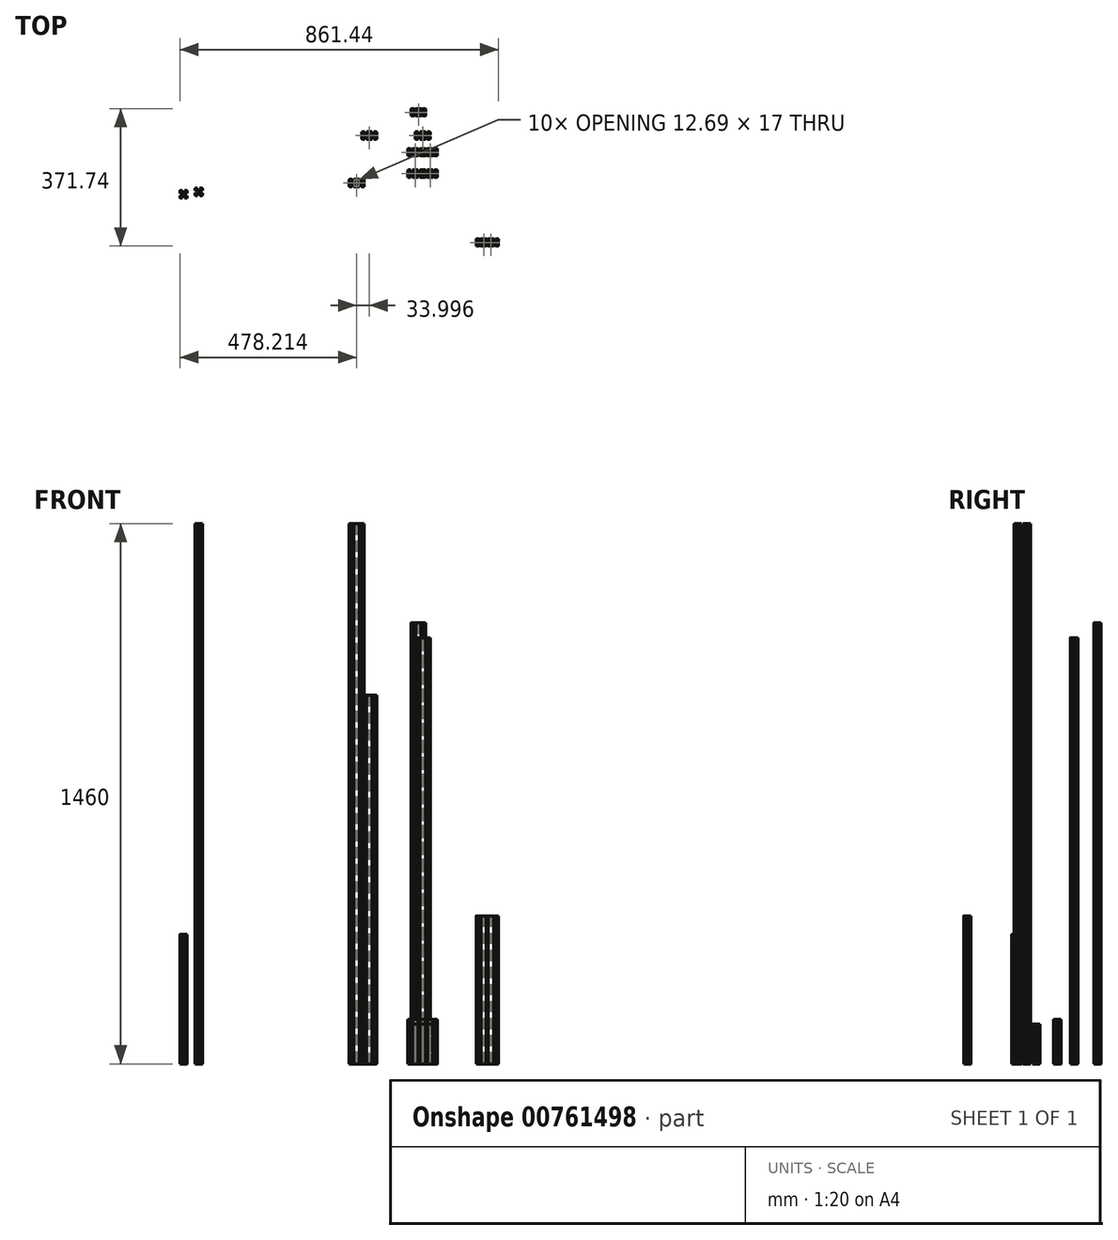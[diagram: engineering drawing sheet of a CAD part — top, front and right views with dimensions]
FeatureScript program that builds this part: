
annotation { "Feature Type Name" : "Feature", "Feature Type Description" : "" }
export const myFeature = defineFeature(function(context is Context, id is Id, definition is map)
    precondition{}
    {
        {
            var Q0;
            Q0=qCreatedBy(makeId("Top.planeOp"),FACE);
            var sketch = newSketch(context, id + "F0", { "sketchPlane" : qUnion([Q0])});
            skLineSegment(sketch, "E0", {"start": v(-5.25, 65.2) * mm, "end": v(-5.25, 60.44) * mm});
            skArc(sketch, "E1", {"start": v(-0.8, 64.75) * mm, "mid": v(-0.24, 65.32) * mm, "end": v(0.52, 65.12) * mm});
            skLineSegment(sketch, "E2", {"start": v(-19.48, 65.12) * mm, "end": v(-19.3, 64.94) * mm});
            skLineSegment(sketch, "E3", {"start": v(1.03, 53.81) * mm, "end": v(1.03, 53.33) * mm});
            skArc(sketch, "E4", {"start": v(-2.4, 64.75) * mm, "mid": v(-1.6, 64.91) * mm, "end": v(-0.8, 64.75) * mm});
            skArc(sketch, "E5", {"start": v(-3.72, 65.12) * mm, "mid": v(-2.96, 65.32) * mm, "end": v(-2.4, 64.75) * mm});
            skLineSegment(sketch, "E6", {"start": v(-3.72, 65.12) * mm, "end": v(-3.9, 64.94) * mm});
            skArc(sketch, "E7", {"start": v(-3.54, 63.62) * mm, "mid": v(-4.1, 64.18) * mm, "end": v(-3.9, 64.94) * mm});
            skArc(sketch, "E8", {"start": v(-3.54, 62.02) * mm, "mid": v(-3.7, 62.82) * mm, "end": v(-3.54, 63.62) * mm});
            skArc(sketch, "E9", {"start": v(-3.9, 60.7) * mm, "mid": v(-4.1, 61.46) * mm, "end": v(-3.54, 62.02) * mm});
            skLineSegment(sketch, "E10", {"start": v(-3.9, 60.7) * mm, "end": v(-3.72, 60.51) * mm});
            skArc(sketch, "E11", {"start": v(-2.4, 60.88) * mm, "mid": v(-2.96, 60.31) * mm, "end": v(-3.72, 60.51) * mm});
            skArc(sketch, "E12", {"start": v(-0.8, 60.88) * mm, "mid": v(-1.6, 60.72) * mm, "end": v(-2.4, 60.88) * mm});
            skArc(sketch, "E13", {"start": v(0.52, 60.51) * mm, "mid": v(-0.24, 60.31) * mm, "end": v(-0.8, 60.88) * mm});
            skLineSegment(sketch, "E14", {"start": v(0.52, 60.51) * mm, "end": v(0.7, 60.7) * mm});
            skArc(sketch, "E15", {"start": v(0.34, 62.02) * mm, "mid": v(0.9, 61.46) * mm, "end": v(0.7, 60.7) * mm});
            skArc(sketch, "E16", {"start": v(0.34, 63.62) * mm, "mid": v(0.5, 62.82) * mm, "end": v(0.34, 62.02) * mm});
            skArc(sketch, "E17", {"start": v(0.7, 64.94) * mm, "mid": v(0.9, 64.18) * mm, "end": v(0.34, 63.62) * mm});
            skLineSegment(sketch, "E18", {"start": v(0.7, 64.94) * mm, "end": v(0.52, 65.12) * mm});
            skArc(sketch, "E19", {"start": v(-19.48, 65.12) * mm, "mid": v(-20.24, 65.32) * mm, "end": v(-20.8, 64.75) * mm});
            skArc(sketch, "E20", {"start": v(-20.8, 64.75) * mm, "mid": v(-21.6, 64.91) * mm, "end": v(-22.4, 64.75) * mm});
            skArc(sketch, "E21", {"start": v(-22.4, 64.75) * mm, "mid": v(-22.96, 65.32) * mm, "end": v(-23.72, 65.12) * mm});
            skLineSegment(sketch, "E22", {"start": v(-23.9, 64.94) * mm, "end": v(-23.72, 65.12) * mm});
            skArc(sketch, "E23", {"start": v(-23.9, 64.94) * mm, "mid": v(-24.1, 64.18) * mm, "end": v(-23.54, 63.62) * mm});
            skArc(sketch, "E24", {"start": v(-23.54, 63.62) * mm, "mid": v(-23.7, 62.82) * mm, "end": v(-23.54, 62.02) * mm});
            skArc(sketch, "E25", {"start": v(-23.54, 62.02) * mm, "mid": v(-24.1, 61.46) * mm, "end": v(-23.9, 60.7) * mm});
            skLineSegment(sketch, "E26", {"start": v(-23.72, 60.51) * mm, "end": v(-23.9, 60.7) * mm});
            skArc(sketch, "E27", {"start": v(-23.72, 60.51) * mm, "mid": v(-22.96, 60.31) * mm, "end": v(-22.4, 60.88) * mm});
            skArc(sketch, "E28", {"start": v(-22.4, 60.88) * mm, "mid": v(-21.6, 60.72) * mm, "end": v(-20.8, 60.88) * mm});
            skArc(sketch, "E29", {"start": v(-20.8, 60.88) * mm, "mid": v(-20.24, 60.31) * mm, "end": v(-19.48, 60.51) * mm});
            skLineSegment(sketch, "E30", {"start": v(-19.3, 60.7) * mm, "end": v(-19.48, 60.51) * mm});
            skArc(sketch, "E31", {"start": v(-19.3, 60.7) * mm, "mid": v(-19.1, 61.46) * mm, "end": v(-19.66, 62.02) * mm});
            skArc(sketch, "E32", {"start": v(-19.66, 62.02) * mm, "mid": v(-19.5, 62.82) * mm, "end": v(-19.66, 63.62) * mm});
            skArc(sketch, "E33", {"start": v(-19.66, 63.62) * mm, "mid": v(-19.1, 64.18) * mm, "end": v(-19.3, 64.94) * mm});
            skArc(sketch, "E34", {"start": v(1.03, 53.81) * mm, "mid": v(1.18, 54.17) * mm, "end": v(1.54, 54.32) * mm});
            skLineSegment(sketch, "E35", {"start": v(1.54, 54.32) * mm, "end": v(3.89, 54.32) * mm});
            skArc(sketch, "E36", {"start": v(4.4, 54.83) * mm, "mid": v(4.25, 54.47) * mm, "end": v(3.89, 54.32) * mm});
            skLineSegment(sketch, "E37", {"start": v(4.4, 55.55) * mm, "end": v(4.4, 54.83) * mm});
            skArc(sketch, "E38", {"start": v(4.25, 55.91) * mm, "mid": v(4.36, 55.75) * mm, "end": v(4.4, 55.55) * mm});
            skLineSegment(sketch, "E39", {"start": v(4.25, 55.91) * mm, "end": v(1.14, 59.02) * mm});
            skArc(sketch, "E40", {"start": v(0.78, 59.16) * mm, "mid": v(0.98, 59.13) * mm, "end": v(1.14, 59.02) * mm});
            skLineSegment(sketch, "E41", {"start": v(0.78, 59.16) * mm, "end": v(-3.98, 59.16) * mm});
            skArc(sketch, "E42", {"start": v(-4.34, 59.02) * mm, "mid": v(-4.18, 59.13) * mm, "end": v(-3.98, 59.16) * mm});
            skLineSegment(sketch, "E43", {"start": v(-4.34, 59.02) * mm, "end": v(-7.45, 55.91) * mm});
            skArc(sketch, "E44", {"start": v(-7.6, 55.55) * mm, "mid": v(-7.56, 55.75) * mm, "end": v(-7.45, 55.91) * mm});
            skLineSegment(sketch, "E45", {"start": v(-7.6, 55.55) * mm, "end": v(-7.6, 54.83) * mm});
            skArc(sketch, "E46", {"start": v(-7.09, 54.32) * mm, "mid": v(-7.45, 54.47) * mm, "end": v(-7.6, 54.83) * mm});
            skLineSegment(sketch, "E47", {"start": v(-7.09, 54.32) * mm, "end": v(-4.74, 54.32) * mm});
            skArc(sketch, "E48", {"start": v(-4.74, 54.32) * mm, "mid": v(-4.38, 54.17) * mm, "end": v(-4.23, 53.81) * mm});
            skLineSegment(sketch, "E49", {"start": v(-4.23, 53.33) * mm, "end": v(-4.23, 53.81) * mm});
            skArc(sketch, "E50", {"start": v(-4.23, 53.33) * mm, "mid": v(-4.38, 52.97) * mm, "end": v(-4.74, 52.82) * mm});
            skLineSegment(sketch, "E51", {"start": v(-18.46, 52.82) * mm, "end": v(-4.74, 52.82) * mm});
            skArc(sketch, "E52", {"start": v(-18.97, 53.33) * mm, "mid": v(-18.82, 52.97) * mm, "end": v(-18.46, 52.82) * mm});
            skLineSegment(sketch, "E53", {"start": v(-18.97, 53.33) * mm, "end": v(-18.97, 53.81) * mm});
            skArc(sketch, "E54", {"start": v(-18.46, 54.32) * mm, "mid": v(-18.82, 54.17) * mm, "end": v(-18.97, 53.81) * mm});
            skLineSegment(sketch, "E55", {"start": v(-16.11, 54.32) * mm, "end": v(-18.46, 54.32) * mm});
            skArc(sketch, "E56", {"start": v(-16.11, 54.32) * mm, "mid": v(-15.75, 54.47) * mm, "end": v(-15.6, 54.83) * mm});
            skLineSegment(sketch, "E57", {"start": v(-15.6, 55.55) * mm, "end": v(-15.6, 54.83) * mm});
            skArc(sketch, "E58", {"start": v(-15.6, 55.55) * mm, "mid": v(-15.64, 55.75) * mm, "end": v(-15.75, 55.91) * mm});
            skLineSegment(sketch, "E59", {"start": v(-18.86, 59.02) * mm, "end": v(-15.75, 55.91) * mm});
            skArc(sketch, "E60", {"start": v(-18.86, 59.02) * mm, "mid": v(-19.02, 59.13) * mm, "end": v(-19.22, 59.16) * mm});
            skLineSegment(sketch, "E61", {"start": v(-23.98, 59.16) * mm, "end": v(-19.22, 59.16) * mm});
            skArc(sketch, "E62", {"start": v(-23.98, 59.16) * mm, "mid": v(-24.18, 59.13) * mm, "end": v(-24.34, 59.02) * mm});
            skLineSegment(sketch, "E63", {"start": v(-27.45, 55.91) * mm, "end": v(-24.34, 59.02) * mm});
            skArc(sketch, "E64", {"start": v(-27.45, 55.91) * mm, "mid": v(-27.56, 55.75) * mm, "end": v(-27.6, 55.55) * mm});
            skLineSegment(sketch, "E65", {"start": v(-27.6, 55.55) * mm, "end": v(-27.6, 54.83) * mm});
            skArc(sketch, "E66", {"start": v(-27.6, 54.83) * mm, "mid": v(-27.45, 54.47) * mm, "end": v(-27.09, 54.32) * mm});
            skLineSegment(sketch, "E67", {"start": v(-24.74, 54.32) * mm, "end": v(-27.09, 54.32) * mm});
            skArc(sketch, "E68", {"start": v(-24.23, 53.81) * mm, "mid": v(-24.38, 54.17) * mm, "end": v(-24.74, 54.32) * mm});
            skLineSegment(sketch, "E69", {"start": v(-24.23, 53.81) * mm, "end": v(-24.23, 53.33) * mm});
            skArc(sketch, "E70", {"start": v(-24.74, 52.82) * mm, "mid": v(-24.38, 52.97) * mm, "end": v(-24.23, 53.33) * mm});
            skLineSegment(sketch, "E71", {"start": v(-30.1, 52.82) * mm, "end": v(-24.74, 52.82) * mm});
            skArc(sketch, "E72", {"start": v(-31.6, 54.32) * mm, "mid": v(-31.16, 53.26) * mm, "end": v(-30.1, 52.82) * mm});
            skLineSegment(sketch, "E73", {"start": v(-31.6, 54.32) * mm, "end": v(-31.6, 59.68) * mm});
            skArc(sketch, "E74", {"start": v(-31.1, 60.19) * mm, "mid": v(-31.45, 60.04) * mm, "end": v(-31.6, 59.68) * mm});
            skLineSegment(sketch, "E75", {"start": v(-31.1, 60.19) * mm, "end": v(-30.6, 60.19) * mm});
            skArc(sketch, "E76", {"start": v(-30.1, 59.68) * mm, "mid": v(-30.25, 60.04) * mm, "end": v(-30.6, 60.19) * mm});
            skLineSegment(sketch, "E77", {"start": v(-30.1, 57.33) * mm, "end": v(-30.1, 59.68) * mm});
            skArc(sketch, "E78", {"start": v(-30.1, 57.33) * mm, "mid": v(-29.95, 56.97) * mm, "end": v(-29.6, 56.82) * mm});
            skLineSegment(sketch, "E79", {"start": v(-28.87, 56.82) * mm, "end": v(-29.6, 56.82) * mm});
            skArc(sketch, "E80", {"start": v(-28.87, 56.82) * mm, "mid": v(-28.67, 56.86) * mm, "end": v(-28.5, 56.97) * mm});
            skLineSegment(sketch, "E81", {"start": v(-25.4, 60.08) * mm, "end": v(-28.5, 56.97) * mm});
            skArc(sketch, "E82", {"start": v(-25.4, 60.08) * mm, "mid": v(-25.3, 60.24) * mm, "end": v(-25.25, 60.44) * mm});
            skLineSegment(sketch, "E83", {"start": v(-25.25, 65.2) * mm, "end": v(-25.25, 60.44) * mm});
            skArc(sketch, "E84", {"start": v(-25.25, 65.2) * mm, "mid": v(-25.3, 65.4) * mm, "end": v(-25.4, 65.56) * mm});
            skLineSegment(sketch, "E85", {"start": v(-25.4, 65.56) * mm, "end": v(-28.5, 68.67) * mm});
            skArc(sketch, "E86", {"start": v(-28.5, 68.67) * mm, "mid": v(-28.67, 68.78) * mm, "end": v(-28.87, 68.81) * mm});
            skLineSegment(sketch, "E87", {"start": v(-28.87, 68.81) * mm, "end": v(-29.6, 68.81) * mm});
            skArc(sketch, "E88", {"start": v(-29.6, 68.81) * mm, "mid": v(-29.95, 68.67) * mm, "end": v(-30.1, 68.3) * mm});
            skLineSegment(sketch, "E89", {"start": v(-30.1, 68.3) * mm, "end": v(-30.1, 65.96) * mm});
            skArc(sketch, "E90", {"start": v(-30.6, 65.45) * mm, "mid": v(-30.25, 65.6) * mm, "end": v(-30.1, 65.96) * mm});
            skLineSegment(sketch, "E91", {"start": v(-30.6, 65.45) * mm, "end": v(-31.1, 65.45) * mm});
            skArc(sketch, "E92", {"start": v(-31.6, 65.96) * mm, "mid": v(-31.45, 65.6) * mm, "end": v(-31.1, 65.45) * mm});
            skLineSegment(sketch, "E93", {"start": v(-31.6, 65.96) * mm, "end": v(-31.6, 71.32) * mm});
            skArc(sketch, "E94", {"start": v(-30.1, 72.82) * mm, "mid": v(-31.16, 72.38) * mm, "end": v(-31.6, 71.32) * mm});
            skLineSegment(sketch, "E95", {"start": v(-30.1, 72.82) * mm, "end": v(-24.74, 72.82) * mm});
            skArc(sketch, "E96", {"start": v(-24.23, 72.31) * mm, "mid": v(-24.38, 72.67) * mm, "end": v(-24.74, 72.82) * mm});
            skLineSegment(sketch, "E97", {"start": v(-24.23, 72.31) * mm, "end": v(-24.23, 71.83) * mm});
            skArc(sketch, "E98", {"start": v(-24.74, 71.32) * mm, "mid": v(-24.38, 71.47) * mm, "end": v(-24.23, 71.83) * mm});
            skLineSegment(sketch, "E99", {"start": v(-24.74, 71.32) * mm, "end": v(-27.09, 71.32) * mm});
            skArc(sketch, "E100", {"start": v(-27.09, 71.32) * mm, "mid": v(-27.45, 71.17) * mm, "end": v(-27.6, 70.81) * mm});
            skLineSegment(sketch, "E101", {"start": v(-27.6, 70.81) * mm, "end": v(-27.6, 70.09) * mm});
            skArc(sketch, "E102", {"start": v(-27.6, 70.09) * mm, "mid": v(-27.56, 69.9) * mm, "end": v(-27.45, 69.73) * mm});
            skLineSegment(sketch, "E103", {"start": v(-27.45, 69.73) * mm, "end": v(-24.34, 66.62) * mm});
            skArc(sketch, "E104", {"start": v(-24.34, 66.62) * mm, "mid": v(-24.18, 66.51) * mm, "end": v(-23.98, 66.47) * mm});
            skLineSegment(sketch, "E105", {"start": v(-23.98, 66.47) * mm, "end": v(-19.22, 66.47) * mm});
            skArc(sketch, "E106", {"start": v(-19.22, 66.47) * mm, "mid": v(-19.02, 66.51) * mm, "end": v(-18.86, 66.62) * mm});
            skLineSegment(sketch, "E107", {"start": v(-18.86, 66.62) * mm, "end": v(-15.75, 69.73) * mm});
            skArc(sketch, "E108", {"start": v(-15.75, 69.73) * mm, "mid": v(-15.64, 69.9) * mm, "end": v(-15.6, 70.09) * mm});
            skLineSegment(sketch, "E109", {"start": v(-15.6, 70.81) * mm, "end": v(-15.6, 70.09) * mm});
            skArc(sketch, "E110", {"start": v(-15.6, 70.81) * mm, "mid": v(-15.75, 71.17) * mm, "end": v(-16.11, 71.32) * mm});
            skLineSegment(sketch, "E111", {"start": v(-16.11, 71.32) * mm, "end": v(-18.46, 71.32) * mm});
            skArc(sketch, "E112", {"start": v(-18.97, 71.83) * mm, "mid": v(-18.82, 71.47) * mm, "end": v(-18.46, 71.32) * mm});
            skLineSegment(sketch, "E113", {"start": v(-18.97, 71.83) * mm, "end": v(-18.97, 72.31) * mm});
            skArc(sketch, "E114", {"start": v(-18.46, 72.82) * mm, "mid": v(-18.82, 72.67) * mm, "end": v(-18.97, 72.31) * mm});
            skLineSegment(sketch, "E115", {"start": v(-4.74, 72.82) * mm, "end": v(-18.46, 72.82) * mm});
            skArc(sketch, "E116", {"start": v(-4.74, 72.82) * mm, "mid": v(-4.38, 72.67) * mm, "end": v(-4.23, 72.31) * mm});
            skLineSegment(sketch, "E117", {"start": v(-4.23, 71.83) * mm, "end": v(-4.23, 72.31) * mm});
            skArc(sketch, "E118", {"start": v(-4.23, 71.83) * mm, "mid": v(-4.38, 71.47) * mm, "end": v(-4.74, 71.32) * mm});
            skLineSegment(sketch, "E119", {"start": v(-7.09, 71.32) * mm, "end": v(-4.74, 71.32) * mm});
            skArc(sketch, "E120", {"start": v(-7.6, 70.81) * mm, "mid": v(-7.45, 71.17) * mm, "end": v(-7.09, 71.32) * mm});
            skLineSegment(sketch, "E121", {"start": v(-7.6, 70.81) * mm, "end": v(-7.6, 70.09) * mm});
            skArc(sketch, "E122", {"start": v(-7.45, 69.73) * mm, "mid": v(-7.56, 69.9) * mm, "end": v(-7.6, 70.09) * mm});
            skLineSegment(sketch, "E123", {"start": v(-4.34, 66.62) * mm, "end": v(-7.45, 69.73) * mm});
            skArc(sketch, "E124", {"start": v(-3.98, 66.47) * mm, "mid": v(-4.18, 66.51) * mm, "end": v(-4.34, 66.62) * mm});
            skLineSegment(sketch, "E125", {"start": v(0.78, 66.47) * mm, "end": v(-3.98, 66.47) * mm});
            skArc(sketch, "E126", {"start": v(1.14, 66.62) * mm, "mid": v(0.98, 66.51) * mm, "end": v(0.78, 66.47) * mm});
            skLineSegment(sketch, "E127", {"start": v(4.25, 69.73) * mm, "end": v(1.14, 66.62) * mm});
            skArc(sketch, "E128", {"start": v(4.4, 70.09) * mm, "mid": v(4.36, 69.9) * mm, "end": v(4.25, 69.73) * mm});
            skLineSegment(sketch, "E129", {"start": v(4.4, 70.81) * mm, "end": v(4.4, 70.09) * mm});
            skArc(sketch, "E130", {"start": v(3.89, 71.32) * mm, "mid": v(4.25, 71.17) * mm, "end": v(4.4, 70.81) * mm});
            skLineSegment(sketch, "E131", {"start": v(1.54, 71.32) * mm, "end": v(3.89, 71.32) * mm});
            skArc(sketch, "E132", {"start": v(1.54, 71.32) * mm, "mid": v(1.18, 71.47) * mm, "end": v(1.03, 71.83) * mm});
            skLineSegment(sketch, "E133", {"start": v(1.03, 72.31) * mm, "end": v(1.03, 71.83) * mm});
            skArc(sketch, "E134", {"start": v(1.03, 72.31) * mm, "mid": v(1.18, 72.67) * mm, "end": v(1.54, 72.82) * mm});
            skLineSegment(sketch, "E135", {"start": v(6.9, 72.82) * mm, "end": v(1.54, 72.82) * mm});
            skArc(sketch, "E136", {"start": v(6.9, 72.82) * mm, "mid": v(7.96, 72.38) * mm, "end": v(8.4, 71.32) * mm});
            skLineSegment(sketch, "E137", {"start": v(8.4, 65.96) * mm, "end": v(8.4, 71.32) * mm});
            skArc(sketch, "E138", {"start": v(8.4, 65.96) * mm, "mid": v(8.25, 65.6) * mm, "end": v(7.9, 65.45) * mm});
            skLineSegment(sketch, "E139", {"start": v(7.4, 65.45) * mm, "end": v(7.9, 65.45) * mm});
            skArc(sketch, "E140", {"start": v(7.4, 65.45) * mm, "mid": v(7.05, 65.6) * mm, "end": v(6.9, 65.96) * mm});
            skLineSegment(sketch, "E141", {"start": v(6.9, 68.3) * mm, "end": v(6.9, 65.96) * mm});
            skArc(sketch, "E142", {"start": v(6.4, 68.81) * mm, "mid": v(6.75, 68.67) * mm, "end": v(6.9, 68.3) * mm});
            skLineSegment(sketch, "E143", {"start": v(5.67, 68.81) * mm, "end": v(6.4, 68.81) * mm});
            skArc(sketch, "E144", {"start": v(5.3, 68.67) * mm, "mid": v(5.47, 68.78) * mm, "end": v(5.67, 68.81) * mm});
            skLineSegment(sketch, "E145", {"start": v(2.2, 65.56) * mm, "end": v(5.3, 68.67) * mm});
            skArc(sketch, "E146", {"start": v(2.06, 65.2) * mm, "mid": v(2.1, 65.4) * mm, "end": v(2.2, 65.56) * mm});
            skLineSegment(sketch, "E147", {"start": v(2.06, 65.2) * mm, "end": v(2.06, 60.44) * mm});
            skArc(sketch, "E148", {"start": v(2.2, 60.08) * mm, "mid": v(2.1, 60.24) * mm, "end": v(2.06, 60.44) * mm});
            skLineSegment(sketch, "E149", {"start": v(2.2, 60.08) * mm, "end": v(5.3, 56.97) * mm});
            skArc(sketch, "E150", {"start": v(5.67, 56.82) * mm, "mid": v(5.47, 56.86) * mm, "end": v(5.3, 56.97) * mm});
            skLineSegment(sketch, "E151", {"start": v(5.67, 56.82) * mm, "end": v(6.4, 56.82) * mm});
            skArc(sketch, "E152", {"start": v(6.9, 57.33) * mm, "mid": v(6.75, 56.97) * mm, "end": v(6.4, 56.82) * mm});
            skLineSegment(sketch, "E153", {"start": v(6.9, 57.33) * mm, "end": v(6.9, 59.68) * mm});
            skArc(sketch, "E154", {"start": v(6.9, 59.68) * mm, "mid": v(7.05, 60.04) * mm, "end": v(7.4, 60.19) * mm});
            skLineSegment(sketch, "E155", {"start": v(7.9, 60.19) * mm, "end": v(7.4, 60.19) * mm});
            skArc(sketch, "E156", {"start": v(7.9, 60.19) * mm, "mid": v(8.25, 60.04) * mm, "end": v(8.4, 59.68) * mm});
            skLineSegment(sketch, "E157", {"start": v(8.4, 54.32) * mm, "end": v(8.4, 59.68) * mm});
            skArc(sketch, "E158", {"start": v(8.4, 54.32) * mm, "mid": v(7.96, 53.26) * mm, "end": v(6.9, 52.82) * mm});
            skLineSegment(sketch, "E159", {"start": v(6.9, 52.82) * mm, "end": v(1.54, 52.82) * mm});
            skArc(sketch, "E160", {"start": v(1.54, 52.82) * mm, "mid": v(1.18, 52.97) * mm, "end": v(1.03, 53.33) * mm});
            skArc(sketch, "E161", {"start": v(-5.25, 65.2) * mm, "mid": v(-5.3, 65.4) * mm, "end": v(-5.4, 65.56) * mm});
            skLineSegment(sketch, "E162", {"start": v(-5.4, 65.56) * mm, "end": v(-8.95, 69.1) * mm});
            skArc(sketch, "E163", {"start": v(-8.95, 69.1) * mm, "mid": v(-9.06, 69.27) * mm, "end": v(-9.1, 69.46) * mm});
            skLineSegment(sketch, "E164", {"start": v(-9.1, 70.81) * mm, "end": v(-9.1, 69.46) * mm});
            skArc(sketch, "E165", {"start": v(-9.6, 71.32) * mm, "mid": v(-9.24, 71.17) * mm, "end": v(-9.1, 70.81) * mm});
            skLineSegment(sketch, "E166", {"start": v(-13.6, 71.32) * mm, "end": v(-9.6, 71.32) * mm});
            skArc(sketch, "E167", {"start": v(-13.6, 71.32) * mm, "mid": v(-13.96, 71.17) * mm, "end": v(-14.1, 70.81) * mm});
            skLineSegment(sketch, "E168", {"start": v(-14.1, 70.81) * mm, "end": v(-14.1, 69.46) * mm});
            skArc(sketch, "E169", {"start": v(-14.25, 69.1) * mm, "mid": v(-14.14, 69.27) * mm, "end": v(-14.1, 69.46) * mm});
            skLineSegment(sketch, "E170", {"start": v(-17.8, 65.56) * mm, "end": v(-14.25, 69.1) * mm});
            skArc(sketch, "E171", {"start": v(-17.8, 65.56) * mm, "mid": v(-17.9, 65.4) * mm, "end": v(-17.94, 65.2) * mm});
            skLineSegment(sketch, "E172", {"start": v(-17.94, 65.2) * mm, "end": v(-17.94, 60.44) * mm});
            skArc(sketch, "E173", {"start": v(-17.94, 60.44) * mm, "mid": v(-17.9, 60.24) * mm, "end": v(-17.8, 60.08) * mm});
            skLineSegment(sketch, "E174", {"start": v(-17.8, 60.08) * mm, "end": v(-14.25, 56.53) * mm});
            skArc(sketch, "E175", {"start": v(-14.1, 56.17) * mm, "mid": v(-14.14, 56.37) * mm, "end": v(-14.25, 56.53) * mm});
            skLineSegment(sketch, "E176", {"start": v(-14.1, 56.17) * mm, "end": v(-14.1, 54.83) * mm});
            skArc(sketch, "E177", {"start": v(-14.1, 54.83) * mm, "mid": v(-13.96, 54.47) * mm, "end": v(-13.6, 54.32) * mm});
            skLineSegment(sketch, "E178", {"start": v(-13.6, 54.32) * mm, "end": v(-9.6, 54.32) * mm});
            skArc(sketch, "E179", {"start": v(-9.1, 54.83) * mm, "mid": v(-9.24, 54.47) * mm, "end": v(-9.6, 54.32) * mm});
            skLineSegment(sketch, "E180", {"start": v(-9.1, 56.17) * mm, "end": v(-9.1, 54.83) * mm});
            skArc(sketch, "E181", {"start": v(-9.1, 56.17) * mm, "mid": v(-9.06, 56.37) * mm, "end": v(-8.95, 56.53) * mm});
            skLineSegment(sketch, "E182", {"start": v(-5.4, 60.08) * mm, "end": v(-8.95, 56.53) * mm});
            skArc(sketch, "E183", {"start": v(-5.25, 60.44) * mm, "mid": v(-5.3, 60.24) * mm, "end": v(-5.4, 60.08) * mm});
            skSolve(sketch);
        }
        {
            var Q0;
            Q0 = qSketchRegion(id + "F0", true);
            extrude(context, id + "F1", {"entities" : qUnion([Q0]), "depth" : 1192 * mm, "offsetDistance" : 25 * mm});
        }
        {
            var Q0;
            Q0=qCreatedBy(makeId("Top.planeOp"),FACE);
            var sketch = newSketch(context, id + "F2", { "sketchPlane" : qUnion([Q0])});
            skLineSegment(sketch, "E184", {"start": v(6.35, 2.38) * mm, "end": v(6.35, -2.38) * mm});
            skArc(sketch, "E185", {"start": v(10.8, 1.94) * mm, "mid": v(11.36, 2.5) * mm, "end": v(12.12, 2.3) * mm});
            skLineSegment(sketch, "E186", {"start": v(-7.88, 2.3) * mm, "end": v(-7.7, 2.12) * mm});
            skLineSegment(sketch, "E187", {"start": v(12.63, -9) * mm, "end": v(12.63, -9.5) * mm});
            skArc(sketch, "E188", {"start": v(9.2, 1.94) * mm, "mid": v(10, 2.1) * mm, "end": v(10.8, 1.94) * mm});
            skArc(sketch, "E189", {"start": v(7.88, 2.3) * mm, "mid": v(8.64, 2.5) * mm, "end": v(9.2, 1.94) * mm});
            skLineSegment(sketch, "E190", {"start": v(7.88, 2.3) * mm, "end": v(7.7, 2.12) * mm});
            skArc(sketch, "E191", {"start": v(8.06, 0.8) * mm, "mid": v(7.5, 1.36) * mm, "end": v(7.7, 2.12) * mm});
            skArc(sketch, "E192", {"start": v(8.06, -0.8) * mm, "mid": v(7.9, 0) * mm, "end": v(8.06, 0.8) * mm});
            skArc(sketch, "E193", {"start": v(7.7, -2.12) * mm, "mid": v(7.5, -1.36) * mm, "end": v(8.06, -0.8) * mm});
            skLineSegment(sketch, "E194", {"start": v(7.7, -2.12) * mm, "end": v(7.88, -2.3) * mm});
            skArc(sketch, "E195", {"start": v(9.2, -1.94) * mm, "mid": v(8.64, -2.5) * mm, "end": v(7.88, -2.3) * mm});
            skArc(sketch, "E196", {"start": v(10.8, -1.94) * mm, "mid": v(10, -2.1) * mm, "end": v(9.2, -1.94) * mm});
            skArc(sketch, "E197", {"start": v(12.12, -2.3) * mm, "mid": v(11.36, -2.5) * mm, "end": v(10.8, -1.94) * mm});
            skLineSegment(sketch, "E198", {"start": v(12.12, -2.3) * mm, "end": v(12.3, -2.12) * mm});
            skArc(sketch, "E199", {"start": v(11.94, -0.8) * mm, "mid": v(12.5, -1.36) * mm, "end": v(12.3, -2.12) * mm});
            skArc(sketch, "E200", {"start": v(11.94, 0.8) * mm, "mid": v(12.1, 0) * mm, "end": v(11.94, -0.8) * mm});
            skArc(sketch, "E201", {"start": v(12.3, 2.12) * mm, "mid": v(12.5, 1.36) * mm, "end": v(11.94, 0.8) * mm});
            skLineSegment(sketch, "E202", {"start": v(12.3, 2.12) * mm, "end": v(12.12, 2.3) * mm});
            skArc(sketch, "E203", {"start": v(-7.88, 2.3) * mm, "mid": v(-8.64, 2.5) * mm, "end": v(-9.2, 1.94) * mm});
            skArc(sketch, "E204", {"start": v(-9.2, 1.94) * mm, "mid": v(-10, 2.1) * mm, "end": v(-10.8, 1.94) * mm});
            skArc(sketch, "E205", {"start": v(-10.8, 1.94) * mm, "mid": v(-11.36, 2.5) * mm, "end": v(-12.12, 2.3) * mm});
            skLineSegment(sketch, "E206", {"start": v(-12.3, 2.12) * mm, "end": v(-12.12, 2.3) * mm});
            skArc(sketch, "E207", {"start": v(-12.3, 2.12) * mm, "mid": v(-12.5, 1.36) * mm, "end": v(-11.94, 0.8) * mm});
            skArc(sketch, "E208", {"start": v(-11.94, 0.8) * mm, "mid": v(-12.1, 0) * mm, "end": v(-11.94, -0.8) * mm});
            skArc(sketch, "E209", {"start": v(-11.94, -0.8) * mm, "mid": v(-12.5, -1.36) * mm, "end": v(-12.3, -2.12) * mm});
            skLineSegment(sketch, "E210", {"start": v(-12.12, -2.3) * mm, "end": v(-12.3, -2.12) * mm});
            skArc(sketch, "E211", {"start": v(-12.12, -2.3) * mm, "mid": v(-11.36, -2.5) * mm, "end": v(-10.8, -1.94) * mm});
            skArc(sketch, "E212", {"start": v(-10.8, -1.94) * mm, "mid": v(-10, -2.1) * mm, "end": v(-9.2, -1.94) * mm});
            skArc(sketch, "E213", {"start": v(-9.2, -1.94) * mm, "mid": v(-8.64, -2.5) * mm, "end": v(-7.88, -2.3) * mm});
            skLineSegment(sketch, "E214", {"start": v(-7.7, -2.12) * mm, "end": v(-7.88, -2.3) * mm});
            skArc(sketch, "E215", {"start": v(-7.7, -2.12) * mm, "mid": v(-7.5, -1.36) * mm, "end": v(-8.06, -0.8) * mm});
            skArc(sketch, "E216", {"start": v(-8.06, -0.8) * mm, "mid": v(-7.9, 0) * mm, "end": v(-8.06, 0.8) * mm});
            skArc(sketch, "E217", {"start": v(-8.06, 0.8) * mm, "mid": v(-7.5, 1.36) * mm, "end": v(-7.7, 2.12) * mm});
            skArc(sketch, "E218", {"start": v(12.63, -9) * mm, "mid": v(12.78, -8.65) * mm, "end": v(13.14, -8.5) * mm});
            skLineSegment(sketch, "E219", {"start": v(13.14, -8.5) * mm, "end": v(15.49, -8.5) * mm});
            skArc(sketch, "E220", {"start": v(16, -8) * mm, "mid": v(15.85, -8.35) * mm, "end": v(15.49, -8.5) * mm});
            skLineSegment(sketch, "E221", {"start": v(16, -7.27) * mm, "end": v(16, -8) * mm});
            skArc(sketch, "E222", {"start": v(15.85, -6.9) * mm, "mid": v(15.96, -7.07) * mm, "end": v(16, -7.27) * mm});
            skLineSegment(sketch, "E223", {"start": v(15.85, -6.9) * mm, "end": v(12.74, -3.8) * mm});
            skArc(sketch, "E224", {"start": v(12.38, -3.66) * mm, "mid": v(12.58, -3.7) * mm, "end": v(12.74, -3.8) * mm});
            skLineSegment(sketch, "E225", {"start": v(12.38, -3.65) * mm, "end": v(7.62, -3.65) * mm});
            skArc(sketch, "E226", {"start": v(7.26, -3.8) * mm, "mid": v(7.42, -3.7) * mm, "end": v(7.62, -3.66) * mm});
            skLineSegment(sketch, "E227", {"start": v(7.26, -3.8) * mm, "end": v(4.15, -6.9) * mm});
            skArc(sketch, "E228", {"start": v(4, -7.27) * mm, "mid": v(4.04, -7.07) * mm, "end": v(4.15, -6.9) * mm});
            skLineSegment(sketch, "E229", {"start": v(4, -7.27) * mm, "end": v(4, -8) * mm});
            skArc(sketch, "E230", {"start": v(4.51, -8.5) * mm, "mid": v(4.15, -8.35) * mm, "end": v(4, -8) * mm});
            skLineSegment(sketch, "E231", {"start": v(4.51, -8.5) * mm, "end": v(6.86, -8.5) * mm});
            skArc(sketch, "E232", {"start": v(6.86, -8.5) * mm, "mid": v(7.22, -8.65) * mm, "end": v(7.37, -9) * mm});
            skLineSegment(sketch, "E233", {"start": v(7.37, -9.5) * mm, "end": v(7.37, -9) * mm});
            skArc(sketch, "E234", {"start": v(7.37, -9.5) * mm, "mid": v(7.22, -9.85) * mm, "end": v(6.86, -10) * mm});
            skLineSegment(sketch, "E235", {"start": v(-6.86, -10) * mm, "end": v(6.86, -10) * mm});
            skArc(sketch, "E236", {"start": v(-7.37, -9.5) * mm, "mid": v(-7.22, -9.85) * mm, "end": v(-6.86, -10) * mm});
            skLineSegment(sketch, "E237", {"start": v(-7.37, -9.5) * mm, "end": v(-7.37, -9) * mm});
            skArc(sketch, "E238", {"start": v(-6.86, -8.5) * mm, "mid": v(-7.22, -8.65) * mm, "end": v(-7.37, -9) * mm});
            skLineSegment(sketch, "E239", {"start": v(-4.51, -8.5) * mm, "end": v(-6.86, -8.5) * mm});
            skArc(sketch, "E240", {"start": v(-4.51, -8.5) * mm, "mid": v(-4.15, -8.35) * mm, "end": v(-4, -8) * mm});
            skLineSegment(sketch, "E241", {"start": v(-4, -7.27) * mm, "end": v(-4, -8) * mm});
            skArc(sketch, "E242", {"start": v(-4, -7.27) * mm, "mid": v(-4.04, -7.07) * mm, "end": v(-4.15, -6.9) * mm});
            skLineSegment(sketch, "E243", {"start": v(-7.26, -3.8) * mm, "end": v(-4.15, -6.9) * mm});
            skArc(sketch, "E244", {"start": v(-7.26, -3.8) * mm, "mid": v(-7.42, -3.7) * mm, "end": v(-7.62, -3.66) * mm});
            skLineSegment(sketch, "E245", {"start": v(-12.38, -3.65) * mm, "end": v(-7.62, -3.65) * mm});
            skArc(sketch, "E246", {"start": v(-12.38, -3.66) * mm, "mid": v(-12.58, -3.7) * mm, "end": v(-12.74, -3.8) * mm});
            skLineSegment(sketch, "E247", {"start": v(-15.85, -6.9) * mm, "end": v(-12.74, -3.8) * mm});
            skArc(sketch, "E248", {"start": v(-15.85, -6.9) * mm, "mid": v(-15.96, -7.07) * mm, "end": v(-16, -7.27) * mm});
            skLineSegment(sketch, "E249", {"start": v(-16, -7.27) * mm, "end": v(-16, -8) * mm});
            skArc(sketch, "E250", {"start": v(-16, -8) * mm, "mid": v(-15.85, -8.35) * mm, "end": v(-15.49, -8.5) * mm});
            skLineSegment(sketch, "E251", {"start": v(-13.14, -8.5) * mm, "end": v(-15.49, -8.5) * mm});
            skArc(sketch, "E252", {"start": v(-12.63, -9) * mm, "mid": v(-12.78, -8.65) * mm, "end": v(-13.14, -8.5) * mm});
            skLineSegment(sketch, "E253", {"start": v(-12.63, -9) * mm, "end": v(-12.63, -9.5) * mm});
            skArc(sketch, "E254", {"start": v(-13.14, -10) * mm, "mid": v(-12.78, -9.85) * mm, "end": v(-12.63, -9.5) * mm});
            skLineSegment(sketch, "E255", {"start": v(-18.5, -10) * mm, "end": v(-13.14, -10) * mm});
            skArc(sketch, "E256", {"start": v(-20, -8.5) * mm, "mid": v(-19.56, -9.56) * mm, "end": v(-18.5, -10) * mm});
            skLineSegment(sketch, "E257", {"start": v(-20, -8.5) * mm, "end": v(-20, -3.14) * mm});
            skArc(sketch, "E258", {"start": v(-19.5, -2.63) * mm, "mid": v(-19.85, -2.78) * mm, "end": v(-20, -3.14) * mm});
            skLineSegment(sketch, "E259", {"start": v(-19.5, -2.63) * mm, "end": v(-19, -2.63) * mm});
            skArc(sketch, "E260", {"start": v(-18.5, -3.14) * mm, "mid": v(-18.65, -2.78) * mm, "end": v(-19, -2.63) * mm});
            skLineSegment(sketch, "E261", {"start": v(-18.5, -5.49) * mm, "end": v(-18.5, -3.14) * mm});
            skArc(sketch, "E262", {"start": v(-18.5, -5.49) * mm, "mid": v(-18.35, -5.85) * mm, "end": v(-18, -6) * mm});
            skLineSegment(sketch, "E263", {"start": v(-17.27, -6) * mm, "end": v(-18, -6) * mm});
            skArc(sketch, "E264", {"start": v(-17.27, -6) * mm, "mid": v(-17.07, -5.96) * mm, "end": v(-16.9, -5.85) * mm});
            skLineSegment(sketch, "E265", {"start": v(-13.8, -2.74) * mm, "end": v(-16.9, -5.85) * mm});
            skArc(sketch, "E266", {"start": v(-13.8, -2.74) * mm, "mid": v(-13.7, -2.58) * mm, "end": v(-13.65, -2.38) * mm});
            skLineSegment(sketch, "E267", {"start": v(-13.65, 2.38) * mm, "end": v(-13.65, -2.38) * mm});
            skArc(sketch, "E268", {"start": v(-13.65, 2.38) * mm, "mid": v(-13.7, 2.58) * mm, "end": v(-13.8, 2.74) * mm});
            skLineSegment(sketch, "E269", {"start": v(-13.8, 2.74) * mm, "end": v(-16.9, 5.85) * mm});
            skArc(sketch, "E270", {"start": v(-16.9, 5.85) * mm, "mid": v(-17.07, 5.96) * mm, "end": v(-17.27, 6) * mm});
            skLineSegment(sketch, "E271", {"start": v(-17.27, 6) * mm, "end": v(-18, 6) * mm});
            skArc(sketch, "E272", {"start": v(-18, 6) * mm, "mid": v(-18.35, 5.85) * mm, "end": v(-18.5, 5.49) * mm});
            skLineSegment(sketch, "E273", {"start": v(-18.5, 5.49) * mm, "end": v(-18.5, 3.14) * mm});
            skArc(sketch, "E274", {"start": v(-19, 2.63) * mm, "mid": v(-18.65, 2.78) * mm, "end": v(-18.5, 3.14) * mm});
            skLineSegment(sketch, "E275", {"start": v(-19, 2.63) * mm, "end": v(-19.5, 2.63) * mm});
            skArc(sketch, "E276", {"start": v(-20, 3.14) * mm, "mid": v(-19.85, 2.78) * mm, "end": v(-19.5, 2.63) * mm});
            skLineSegment(sketch, "E277", {"start": v(-20, 3.14) * mm, "end": v(-20, 8.5) * mm});
            skArc(sketch, "E278", {"start": v(-18.5, 10) * mm, "mid": v(-19.56, 9.56) * mm, "end": v(-20, 8.5) * mm});
            skLineSegment(sketch, "E279", {"start": v(-18.5, 10) * mm, "end": v(-13.14, 10) * mm});
            skArc(sketch, "E280", {"start": v(-12.63, 9.5) * mm, "mid": v(-12.78, 9.85) * mm, "end": v(-13.14, 10) * mm});
            skLineSegment(sketch, "E281", {"start": v(-12.63, 9.5) * mm, "end": v(-12.63, 9) * mm});
            skArc(sketch, "E282", {"start": v(-13.14, 8.5) * mm, "mid": v(-12.78, 8.65) * mm, "end": v(-12.63, 9) * mm});
            skLineSegment(sketch, "E283", {"start": v(-13.14, 8.5) * mm, "end": v(-15.49, 8.5) * mm});
            skArc(sketch, "E284", {"start": v(-15.49, 8.5) * mm, "mid": v(-15.85, 8.35) * mm, "end": v(-16, 8) * mm});
            skLineSegment(sketch, "E285", {"start": v(-16, 8) * mm, "end": v(-16, 7.27) * mm});
            skArc(sketch, "E286", {"start": v(-16, 7.27) * mm, "mid": v(-15.96, 7.07) * mm, "end": v(-15.85, 6.9) * mm});
            skLineSegment(sketch, "E287", {"start": v(-15.85, 6.9) * mm, "end": v(-12.74, 3.8) * mm});
            skArc(sketch, "E288", {"start": v(-12.74, 3.8) * mm, "mid": v(-12.58, 3.7) * mm, "end": v(-12.38, 3.66) * mm});
            skLineSegment(sketch, "E289", {"start": v(-12.38, 3.65) * mm, "end": v(-7.62, 3.65) * mm});
            skArc(sketch, "E290", {"start": v(-7.62, 3.66) * mm, "mid": v(-7.42, 3.7) * mm, "end": v(-7.26, 3.8) * mm});
            skLineSegment(sketch, "E291", {"start": v(-7.26, 3.8) * mm, "end": v(-4.15, 6.9) * mm});
            skArc(sketch, "E292", {"start": v(-4.15, 6.9) * mm, "mid": v(-4.04, 7.07) * mm, "end": v(-4, 7.27) * mm});
            skLineSegment(sketch, "E293", {"start": v(-4, 8) * mm, "end": v(-4, 7.27) * mm});
            skArc(sketch, "E294", {"start": v(-4, 8) * mm, "mid": v(-4.15, 8.35) * mm, "end": v(-4.51, 8.5) * mm});
            skLineSegment(sketch, "E295", {"start": v(-4.51, 8.5) * mm, "end": v(-6.86, 8.5) * mm});
            skArc(sketch, "E296", {"start": v(-7.37, 9) * mm, "mid": v(-7.22, 8.65) * mm, "end": v(-6.86, 8.5) * mm});
            skLineSegment(sketch, "E297", {"start": v(-7.37, 9) * mm, "end": v(-7.37, 9.5) * mm});
            skArc(sketch, "E298", {"start": v(-6.86, 10) * mm, "mid": v(-7.22, 9.85) * mm, "end": v(-7.37, 9.5) * mm});
            skLineSegment(sketch, "E299", {"start": v(6.86, 10) * mm, "end": v(-6.86, 10) * mm});
            skArc(sketch, "E300", {"start": v(6.86, 10) * mm, "mid": v(7.22, 9.85) * mm, "end": v(7.37, 9.5) * mm});
            skLineSegment(sketch, "E301", {"start": v(7.37, 9) * mm, "end": v(7.37, 9.5) * mm});
            skArc(sketch, "E302", {"start": v(7.37, 9) * mm, "mid": v(7.22, 8.65) * mm, "end": v(6.86, 8.5) * mm});
            skLineSegment(sketch, "E303", {"start": v(4.51, 8.5) * mm, "end": v(6.86, 8.5) * mm});
            skArc(sketch, "E304", {"start": v(4, 8) * mm, "mid": v(4.15, 8.35) * mm, "end": v(4.51, 8.5) * mm});
            skLineSegment(sketch, "E305", {"start": v(4, 8) * mm, "end": v(4, 7.27) * mm});
            skArc(sketch, "E306", {"start": v(4.15, 6.9) * mm, "mid": v(4.04, 7.07) * mm, "end": v(4, 7.27) * mm});
            skLineSegment(sketch, "E307", {"start": v(7.26, 3.8) * mm, "end": v(4.15, 6.9) * mm});
            skArc(sketch, "E308", {"start": v(7.62, 3.66) * mm, "mid": v(7.42, 3.7) * mm, "end": v(7.26, 3.8) * mm});
            skLineSegment(sketch, "E309", {"start": v(12.38, 3.65) * mm, "end": v(7.62, 3.65) * mm});
            skArc(sketch, "E310", {"start": v(12.74, 3.8) * mm, "mid": v(12.58, 3.7) * mm, "end": v(12.38, 3.66) * mm});
            skLineSegment(sketch, "E311", {"start": v(15.85, 6.9) * mm, "end": v(12.74, 3.8) * mm});
            skArc(sketch, "E312", {"start": v(16, 7.27) * mm, "mid": v(15.96, 7.07) * mm, "end": v(15.85, 6.9) * mm});
            skLineSegment(sketch, "E313", {"start": v(16, 8) * mm, "end": v(16, 7.27) * mm});
            skArc(sketch, "E314", {"start": v(15.49, 8.5) * mm, "mid": v(15.85, 8.35) * mm, "end": v(16, 8) * mm});
            skLineSegment(sketch, "E315", {"start": v(13.14, 8.5) * mm, "end": v(15.49, 8.5) * mm});
            skArc(sketch, "E316", {"start": v(13.14, 8.5) * mm, "mid": v(12.78, 8.65) * mm, "end": v(12.63, 9) * mm});
            skLineSegment(sketch, "E317", {"start": v(12.63, 9.5) * mm, "end": v(12.63, 9) * mm});
            skArc(sketch, "E318", {"start": v(12.63, 9.5) * mm, "mid": v(12.78, 9.85) * mm, "end": v(13.14, 10) * mm});
            skLineSegment(sketch, "E319", {"start": v(18.5, 10) * mm, "end": v(13.14, 10) * mm});
            skArc(sketch, "E320", {"start": v(18.5, 10) * mm, "mid": v(19.56, 9.56) * mm, "end": v(20, 8.5) * mm});
            skLineSegment(sketch, "E321", {"start": v(20, 3.14) * mm, "end": v(20, 8.5) * mm});
            skArc(sketch, "E322", {"start": v(20, 3.14) * mm, "mid": v(19.85, 2.78) * mm, "end": v(19.5, 2.63) * mm});
            skLineSegment(sketch, "E323", {"start": v(19, 2.63) * mm, "end": v(19.5, 2.63) * mm});
            skArc(sketch, "E324", {"start": v(19, 2.63) * mm, "mid": v(18.65, 2.78) * mm, "end": v(18.5, 3.14) * mm});
            skLineSegment(sketch, "E325", {"start": v(18.5, 5.49) * mm, "end": v(18.5, 3.14) * mm});
            skArc(sketch, "E326", {"start": v(18, 6) * mm, "mid": v(18.35, 5.85) * mm, "end": v(18.5, 5.49) * mm});
            skLineSegment(sketch, "E327", {"start": v(17.27, 6) * mm, "end": v(18, 6) * mm});
            skArc(sketch, "E328", {"start": v(16.9, 5.85) * mm, "mid": v(17.07, 5.96) * mm, "end": v(17.27, 6) * mm});
            skLineSegment(sketch, "E329", {"start": v(13.8, 2.74) * mm, "end": v(16.9, 5.85) * mm});
            skArc(sketch, "E330", {"start": v(13.66, 2.38) * mm, "mid": v(13.7, 2.58) * mm, "end": v(13.8, 2.74) * mm});
            skLineSegment(sketch, "E331", {"start": v(13.66, 2.38) * mm, "end": v(13.66, -2.38) * mm});
            skArc(sketch, "E332", {"start": v(13.8, -2.74) * mm, "mid": v(13.7, -2.58) * mm, "end": v(13.66, -2.38) * mm});
            skLineSegment(sketch, "E333", {"start": v(13.8, -2.74) * mm, "end": v(16.9, -5.85) * mm});
            skArc(sketch, "E334", {"start": v(17.27, -6) * mm, "mid": v(17.07, -5.96) * mm, "end": v(16.9, -5.85) * mm});
            skLineSegment(sketch, "E335", {"start": v(17.27, -6) * mm, "end": v(18, -6) * mm});
            skArc(sketch, "E336", {"start": v(18.5, -5.49) * mm, "mid": v(18.35, -5.85) * mm, "end": v(18, -6) * mm});
            skLineSegment(sketch, "E337", {"start": v(18.5, -5.49) * mm, "end": v(18.5, -3.14) * mm});
            skArc(sketch, "E338", {"start": v(18.5, -3.14) * mm, "mid": v(18.65, -2.78) * mm, "end": v(19, -2.63) * mm});
            skLineSegment(sketch, "E339", {"start": v(19.5, -2.63) * mm, "end": v(19, -2.63) * mm});
            skArc(sketch, "E340", {"start": v(19.5, -2.63) * mm, "mid": v(19.85, -2.78) * mm, "end": v(20, -3.14) * mm});
            skLineSegment(sketch, "E341", {"start": v(20, -8.5) * mm, "end": v(20, -3.14) * mm});
            skArc(sketch, "E342", {"start": v(20, -8.5) * mm, "mid": v(19.56, -9.56) * mm, "end": v(18.5, -10) * mm});
            skLineSegment(sketch, "E343", {"start": v(18.5, -10) * mm, "end": v(13.14, -10) * mm});
            skArc(sketch, "E344", {"start": v(13.14, -10) * mm, "mid": v(12.78, -9.85) * mm, "end": v(12.63, -9.5) * mm});
            skArc(sketch, "E345", {"start": v(6.35, 2.38) * mm, "mid": v(6.3, 2.58) * mm, "end": v(6.2, 2.74) * mm});
            skLineSegment(sketch, "E346", {"start": v(6.2, 2.74) * mm, "end": v(2.65, 6.29) * mm});
            skArc(sketch, "E347", {"start": v(2.65, 6.29) * mm, "mid": v(2.54, 6.45) * mm, "end": v(2.5, 6.64) * mm});
            skLineSegment(sketch, "E348", {"start": v(2.5, 8) * mm, "end": v(2.5, 6.64) * mm});
            skArc(sketch, "E349", {"start": v(2, 8.5) * mm, "mid": v(2.36, 8.35) * mm, "end": v(2.5, 8) * mm});
            skLineSegment(sketch, "E350", {"start": v(-2, 8.5) * mm, "end": v(2, 8.5) * mm});
            skArc(sketch, "E351", {"start": v(-2, 8.5) * mm, "mid": v(-2.36, 8.35) * mm, "end": v(-2.5, 8) * mm});
            skLineSegment(sketch, "E352", {"start": v(-2.5, 8) * mm, "end": v(-2.5, 6.64) * mm});
            skArc(sketch, "E353", {"start": v(-2.65, 6.29) * mm, "mid": v(-2.54, 6.45) * mm, "end": v(-2.5, 6.64) * mm});
            skLineSegment(sketch, "E354", {"start": v(-6.2, 2.74) * mm, "end": v(-2.65, 6.29) * mm});
            skArc(sketch, "E355", {"start": v(-6.2, 2.74) * mm, "mid": v(-6.3, 2.58) * mm, "end": v(-6.34, 2.38) * mm});
            skLineSegment(sketch, "E356", {"start": v(-6.34, 2.38) * mm, "end": v(-6.34, -2.38) * mm});
            skArc(sketch, "E357", {"start": v(-6.34, -2.38) * mm, "mid": v(-6.3, -2.58) * mm, "end": v(-6.2, -2.74) * mm});
            skLineSegment(sketch, "E358", {"start": v(-6.2, -2.74) * mm, "end": v(-2.65, -6.29) * mm});
            skArc(sketch, "E359", {"start": v(-2.5, -6.64) * mm, "mid": v(-2.54, -6.45) * mm, "end": v(-2.65, -6.29) * mm});
            skLineSegment(sketch, "E360", {"start": v(-2.5, -6.64) * mm, "end": v(-2.5, -8) * mm});
            skArc(sketch, "E361", {"start": v(-2.5, -8) * mm, "mid": v(-2.36, -8.35) * mm, "end": v(-2, -8.5) * mm});
            skLineSegment(sketch, "E362", {"start": v(-2, -8.5) * mm, "end": v(2, -8.5) * mm});
            skArc(sketch, "E363", {"start": v(2.5, -8) * mm, "mid": v(2.36, -8.35) * mm, "end": v(2, -8.5) * mm});
            skLineSegment(sketch, "E364", {"start": v(2.5, -6.64) * mm, "end": v(2.5, -8) * mm});
            skArc(sketch, "E365", {"start": v(2.5, -6.64) * mm, "mid": v(2.54, -6.45) * mm, "end": v(2.65, -6.29) * mm});
            skLineSegment(sketch, "E366", {"start": v(6.2, -2.74) * mm, "end": v(2.65, -6.29) * mm});
            skArc(sketch, "E367", {"start": v(6.35, -2.38) * mm, "mid": v(6.3, -2.58) * mm, "end": v(6.2, -2.74) * mm});
            skSolve(sketch);
        }
        {
            var Q0;
            Q0 = qSketchRegion(id + "F2", true);
            extrude(context, id + "F3", {"entities" : qUnion([Q0]), "depth" : 1152 * mm, "offsetDistance" : 25 * mm});
        }
        {
            var Q0;
            Q0=qCreatedBy(makeId("Top.planeOp"),FACE);
            var sketch = newSketch(context, id + "F4", { "sketchPlane" : qUnion([Q0])});
            skLineSegment(sketch, "E368", {"start": v(-13.66, -42.72) * mm, "end": v(-13.66, -47.48) * mm});
            skArc(sketch, "E369", {"start": v(-9.2, -43.16) * mm, "mid": v(-8.64, -42.6) * mm, "end": v(-7.88, -42.8) * mm});
            skLineSegment(sketch, "E370", {"start": v(-27.88, -42.8) * mm, "end": v(-27.7, -42.98) * mm});
            skLineSegment(sketch, "E371", {"start": v(-7.37, -54.1) * mm, "end": v(-7.37, -54.6) * mm});
            skArc(sketch, "E372", {"start": v(-10.8, -43.16) * mm, "mid": v(-10, -43) * mm, "end": v(-9.2, -43.16) * mm});
            skArc(sketch, "E373", {"start": v(-12.12, -42.8) * mm, "mid": v(-11.36, -42.6) * mm, "end": v(-10.8, -43.16) * mm});
            skLineSegment(sketch, "E374", {"start": v(-12.12, -42.8) * mm, "end": v(-12.3, -42.98) * mm});
            skArc(sketch, "E375", {"start": v(-11.94, -44.3) * mm, "mid": v(-12.5, -43.74) * mm, "end": v(-12.3, -42.98) * mm});
            skArc(sketch, "E376", {"start": v(-11.94, -45.9) * mm, "mid": v(-12.1, -45.1) * mm, "end": v(-11.94, -44.3) * mm});
            skArc(sketch, "E377", {"start": v(-12.3, -47.22) * mm, "mid": v(-12.5, -46.46) * mm, "end": v(-11.94, -45.9) * mm});
            skLineSegment(sketch, "E378", {"start": v(-12.3, -47.22) * mm, "end": v(-12.12, -47.4) * mm});
            skArc(sketch, "E379", {"start": v(-10.8, -47.04) * mm, "mid": v(-11.36, -47.6) * mm, "end": v(-12.12, -47.4) * mm});
            skArc(sketch, "E380", {"start": v(-9.2, -47.04) * mm, "mid": v(-10, -47.2) * mm, "end": v(-10.8, -47.04) * mm});
            skArc(sketch, "E381", {"start": v(-7.88, -47.4) * mm, "mid": v(-8.64, -47.6) * mm, "end": v(-9.2, -47.04) * mm});
            skLineSegment(sketch, "E382", {"start": v(-7.88, -47.4) * mm, "end": v(-7.7, -47.22) * mm});
            skArc(sketch, "E383", {"start": v(-8.06, -45.9) * mm, "mid": v(-7.5, -46.46) * mm, "end": v(-7.7, -47.22) * mm});
            skArc(sketch, "E384", {"start": v(-8.06, -44.3) * mm, "mid": v(-7.9, -45.1) * mm, "end": v(-8.06, -45.9) * mm});
            skArc(sketch, "E385", {"start": v(-7.7, -42.98) * mm, "mid": v(-7.5, -43.74) * mm, "end": v(-8.06, -44.3) * mm});
            skLineSegment(sketch, "E386", {"start": v(-7.7, -42.98) * mm, "end": v(-7.88, -42.8) * mm});
            skArc(sketch, "E387", {"start": v(-27.88, -42.8) * mm, "mid": v(-28.64, -42.6) * mm, "end": v(-29.2, -43.16) * mm});
            skArc(sketch, "E388", {"start": v(-29.2, -43.16) * mm, "mid": v(-30, -43) * mm, "end": v(-30.8, -43.16) * mm});
            skArc(sketch, "E389", {"start": v(-30.8, -43.16) * mm, "mid": v(-31.36, -42.6) * mm, "end": v(-32.12, -42.8) * mm});
            skLineSegment(sketch, "E390", {"start": v(-32.3, -42.98) * mm, "end": v(-32.12, -42.8) * mm});
            skArc(sketch, "E391", {"start": v(-32.3, -42.98) * mm, "mid": v(-32.5, -43.74) * mm, "end": v(-31.94, -44.3) * mm});
            skArc(sketch, "E392", {"start": v(-31.94, -44.3) * mm, "mid": v(-32.1, -45.1) * mm, "end": v(-31.94, -45.9) * mm});
            skArc(sketch, "E393", {"start": v(-31.94, -45.9) * mm, "mid": v(-32.5, -46.46) * mm, "end": v(-32.3, -47.22) * mm});
            skLineSegment(sketch, "E394", {"start": v(-32.12, -47.4) * mm, "end": v(-32.3, -47.22) * mm});
            skArc(sketch, "E395", {"start": v(-32.12, -47.4) * mm, "mid": v(-31.36, -47.6) * mm, "end": v(-30.8, -47.04) * mm});
            skArc(sketch, "E396", {"start": v(-30.8, -47.04) * mm, "mid": v(-30, -47.2) * mm, "end": v(-29.2, -47.04) * mm});
            skArc(sketch, "E397", {"start": v(-29.2, -47.04) * mm, "mid": v(-28.64, -47.6) * mm, "end": v(-27.88, -47.4) * mm});
            skLineSegment(sketch, "E398", {"start": v(-27.7, -47.22) * mm, "end": v(-27.88, -47.4) * mm});
            skArc(sketch, "E399", {"start": v(-27.7, -47.22) * mm, "mid": v(-27.5, -46.46) * mm, "end": v(-28.06, -45.9) * mm});
            skArc(sketch, "E400", {"start": v(-28.06, -45.9) * mm, "mid": v(-27.9, -45.1) * mm, "end": v(-28.06, -44.3) * mm});
            skArc(sketch, "E401", {"start": v(-28.06, -44.3) * mm, "mid": v(-27.5, -43.74) * mm, "end": v(-27.7, -42.98) * mm});
            skArc(sketch, "E402", {"start": v(-7.37, -54.1) * mm, "mid": v(-7.22, -53.75) * mm, "end": v(-6.86, -53.6) * mm});
            skLineSegment(sketch, "E403", {"start": v(-6.86, -53.6) * mm, "end": v(-4.51, -53.6) * mm});
            skArc(sketch, "E404", {"start": v(-4, -53.1) * mm, "mid": v(-4.15, -53.45) * mm, "end": v(-4.51, -53.6) * mm});
            skLineSegment(sketch, "E405", {"start": v(-4, -52.37) * mm, "end": v(-4, -53.1) * mm});
            skArc(sketch, "E406", {"start": v(-4.15, -52) * mm, "mid": v(-4.04, -52.17) * mm, "end": v(-4, -52.37) * mm});
            skLineSegment(sketch, "E407", {"start": v(-4.15, -52) * mm, "end": v(-7.26, -48.9) * mm});
            skArc(sketch, "E408", {"start": v(-7.62, -48.76) * mm, "mid": v(-7.42, -48.8) * mm, "end": v(-7.26, -48.9) * mm});
            skLineSegment(sketch, "E409", {"start": v(-7.62, -48.75) * mm, "end": v(-12.38, -48.75) * mm});
            skArc(sketch, "E410", {"start": v(-12.74, -48.9) * mm, "mid": v(-12.58, -48.8) * mm, "end": v(-12.38, -48.76) * mm});
            skLineSegment(sketch, "E411", {"start": v(-12.74, -48.9) * mm, "end": v(-15.85, -52) * mm});
            skArc(sketch, "E412", {"start": v(-16, -52.37) * mm, "mid": v(-15.96, -52.17) * mm, "end": v(-15.85, -52) * mm});
            skLineSegment(sketch, "E413", {"start": v(-16, -52.37) * mm, "end": v(-16, -53.1) * mm});
            skArc(sketch, "E414", {"start": v(-15.49, -53.6) * mm, "mid": v(-15.85, -53.45) * mm, "end": v(-16, -53.1) * mm});
            skLineSegment(sketch, "E415", {"start": v(-15.49, -53.6) * mm, "end": v(-13.14, -53.6) * mm});
            skArc(sketch, "E416", {"start": v(-13.14, -53.6) * mm, "mid": v(-12.78, -53.75) * mm, "end": v(-12.63, -54.1) * mm});
            skLineSegment(sketch, "E417", {"start": v(-12.63, -54.6) * mm, "end": v(-12.63, -54.1) * mm});
            skArc(sketch, "E418", {"start": v(-12.63, -54.6) * mm, "mid": v(-12.78, -54.95) * mm, "end": v(-13.14, -55.1) * mm});
            skLineSegment(sketch, "E419", {"start": v(-26.86, -55.1) * mm, "end": v(-13.14, -55.1) * mm});
            skArc(sketch, "E420", {"start": v(-27.37, -54.6) * mm, "mid": v(-27.22, -54.95) * mm, "end": v(-26.86, -55.1) * mm});
            skLineSegment(sketch, "E421", {"start": v(-27.37, -54.6) * mm, "end": v(-27.37, -54.1) * mm});
            skArc(sketch, "E422", {"start": v(-26.86, -53.6) * mm, "mid": v(-27.22, -53.75) * mm, "end": v(-27.37, -54.1) * mm});
            skLineSegment(sketch, "E423", {"start": v(-24.51, -53.6) * mm, "end": v(-26.86, -53.6) * mm});
            skArc(sketch, "E424", {"start": v(-24.51, -53.6) * mm, "mid": v(-24.15, -53.45) * mm, "end": v(-24, -53.1) * mm});
            skLineSegment(sketch, "E425", {"start": v(-24, -52.37) * mm, "end": v(-24, -53.1) * mm});
            skArc(sketch, "E426", {"start": v(-24, -52.37) * mm, "mid": v(-24.04, -52.17) * mm, "end": v(-24.15, -52) * mm});
            skLineSegment(sketch, "E427", {"start": v(-27.26, -48.9) * mm, "end": v(-24.15, -52) * mm});
            skArc(sketch, "E428", {"start": v(-27.26, -48.9) * mm, "mid": v(-27.42, -48.8) * mm, "end": v(-27.62, -48.76) * mm});
            skLineSegment(sketch, "E429", {"start": v(-32.38, -48.75) * mm, "end": v(-27.62, -48.75) * mm});
            skArc(sketch, "E430", {"start": v(-32.38, -48.76) * mm, "mid": v(-32.58, -48.8) * mm, "end": v(-32.74, -48.9) * mm});
            skLineSegment(sketch, "E431", {"start": v(-35.85, -52) * mm, "end": v(-32.74, -48.9) * mm});
            skArc(sketch, "E432", {"start": v(-35.85, -52) * mm, "mid": v(-35.96, -52.17) * mm, "end": v(-36, -52.37) * mm});
            skLineSegment(sketch, "E433", {"start": v(-36, -52.37) * mm, "end": v(-36, -53.1) * mm});
            skArc(sketch, "E434", {"start": v(-36, -53.1) * mm, "mid": v(-35.85, -53.45) * mm, "end": v(-35.49, -53.6) * mm});
            skLineSegment(sketch, "E435", {"start": v(-33.14, -53.6) * mm, "end": v(-35.49, -53.6) * mm});
            skArc(sketch, "E436", {"start": v(-32.63, -54.1) * mm, "mid": v(-32.78, -53.75) * mm, "end": v(-33.14, -53.6) * mm});
            skLineSegment(sketch, "E437", {"start": v(-32.63, -54.1) * mm, "end": v(-32.63, -54.6) * mm});
            skArc(sketch, "E438", {"start": v(-33.14, -55.1) * mm, "mid": v(-32.78, -54.95) * mm, "end": v(-32.63, -54.6) * mm});
            skLineSegment(sketch, "E439", {"start": v(-38.5, -55.1) * mm, "end": v(-33.14, -55.1) * mm});
            skArc(sketch, "E440", {"start": v(-40, -53.6) * mm, "mid": v(-39.56, -54.66) * mm, "end": v(-38.5, -55.1) * mm});
            skLineSegment(sketch, "E441", {"start": v(-40, -53.6) * mm, "end": v(-40, -48.24) * mm});
            skArc(sketch, "E442", {"start": v(-39.5, -47.73) * mm, "mid": v(-39.85, -47.88) * mm, "end": v(-40, -48.24) * mm});
            skLineSegment(sketch, "E443", {"start": v(-39.5, -47.73) * mm, "end": v(-39, -47.73) * mm});
            skArc(sketch, "E444", {"start": v(-38.5, -48.24) * mm, "mid": v(-38.65, -47.88) * mm, "end": v(-39, -47.73) * mm});
            skLineSegment(sketch, "E445", {"start": v(-38.5, -50.59) * mm, "end": v(-38.5, -48.24) * mm});
            skArc(sketch, "E446", {"start": v(-38.5, -50.59) * mm, "mid": v(-38.35, -50.95) * mm, "end": v(-38, -51.1) * mm});
            skLineSegment(sketch, "E447", {"start": v(-37.27, -51.1) * mm, "end": v(-38, -51.1) * mm});
            skArc(sketch, "E448", {"start": v(-37.27, -51.1) * mm, "mid": v(-37.07, -51.06) * mm, "end": v(-36.9, -50.95) * mm});
            skLineSegment(sketch, "E449", {"start": v(-33.8, -47.84) * mm, "end": v(-36.9, -50.95) * mm});
            skArc(sketch, "E450", {"start": v(-33.8, -47.84) * mm, "mid": v(-33.7, -47.68) * mm, "end": v(-33.66, -47.48) * mm});
            skLineSegment(sketch, "E451", {"start": v(-33.66, -42.72) * mm, "end": v(-33.66, -47.48) * mm});
            skArc(sketch, "E452", {"start": v(-33.66, -42.72) * mm, "mid": v(-33.7, -42.52) * mm, "end": v(-33.8, -42.36) * mm});
            skLineSegment(sketch, "E453", {"start": v(-33.8, -42.36) * mm, "end": v(-36.9, -39.25) * mm});
            skArc(sketch, "E454", {"start": v(-36.9, -39.25) * mm, "mid": v(-37.07, -39.14) * mm, "end": v(-37.27, -39.1) * mm});
            skLineSegment(sketch, "E455", {"start": v(-37.27, -39.1) * mm, "end": v(-38, -39.1) * mm});
            skArc(sketch, "E456", {"start": v(-38, -39.1) * mm, "mid": v(-38.35, -39.25) * mm, "end": v(-38.5, -39.61) * mm});
            skLineSegment(sketch, "E457", {"start": v(-38.5, -39.61) * mm, "end": v(-38.5, -41.96) * mm});
            skArc(sketch, "E458", {"start": v(-39, -42.47) * mm, "mid": v(-38.65, -42.32) * mm, "end": v(-38.5, -41.96) * mm});
            skLineSegment(sketch, "E459", {"start": v(-39, -42.47) * mm, "end": v(-39.5, -42.47) * mm});
            skArc(sketch, "E460", {"start": v(-40, -41.96) * mm, "mid": v(-39.85, -42.32) * mm, "end": v(-39.5, -42.47) * mm});
            skLineSegment(sketch, "E461", {"start": v(-40, -41.96) * mm, "end": v(-40, -36.6) * mm});
            skArc(sketch, "E462", {"start": v(-38.5, -35.1) * mm, "mid": v(-39.56, -35.54) * mm, "end": v(-40, -36.6) * mm});
            skLineSegment(sketch, "E463", {"start": v(-38.5, -35.1) * mm, "end": v(-33.14, -35.1) * mm});
            skArc(sketch, "E464", {"start": v(-32.63, -35.6) * mm, "mid": v(-32.78, -35.25) * mm, "end": v(-33.14, -35.1) * mm});
            skLineSegment(sketch, "E465", {"start": v(-32.63, -35.6) * mm, "end": v(-32.63, -36.1) * mm});
            skArc(sketch, "E466", {"start": v(-33.14, -36.6) * mm, "mid": v(-32.78, -36.45) * mm, "end": v(-32.63, -36.1) * mm});
            skLineSegment(sketch, "E467", {"start": v(-33.14, -36.6) * mm, "end": v(-35.49, -36.6) * mm});
            skArc(sketch, "E468", {"start": v(-35.49, -36.6) * mm, "mid": v(-35.85, -36.75) * mm, "end": v(-36, -37.1) * mm});
            skLineSegment(sketch, "E469", {"start": v(-36, -37.1) * mm, "end": v(-36, -37.83) * mm});
            skArc(sketch, "E470", {"start": v(-36, -37.83) * mm, "mid": v(-35.96, -38.03) * mm, "end": v(-35.85, -38.2) * mm});
            skLineSegment(sketch, "E471", {"start": v(-35.85, -38.2) * mm, "end": v(-32.74, -41.3) * mm});
            skArc(sketch, "E472", {"start": v(-32.74, -41.3) * mm, "mid": v(-32.58, -41.4) * mm, "end": v(-32.38, -41.44) * mm});
            skLineSegment(sketch, "E473", {"start": v(-32.38, -41.44) * mm, "end": v(-27.62, -41.44) * mm});
            skArc(sketch, "E474", {"start": v(-27.62, -41.44) * mm, "mid": v(-27.42, -41.4) * mm, "end": v(-27.26, -41.3) * mm});
            skLineSegment(sketch, "E475", {"start": v(-27.26, -41.3) * mm, "end": v(-24.15, -38.2) * mm});
            skArc(sketch, "E476", {"start": v(-24.15, -38.2) * mm, "mid": v(-24.04, -38.03) * mm, "end": v(-24, -37.83) * mm});
            skLineSegment(sketch, "E477", {"start": v(-24, -37.1) * mm, "end": v(-24, -37.83) * mm});
            skArc(sketch, "E478", {"start": v(-24, -37.1) * mm, "mid": v(-24.15, -36.75) * mm, "end": v(-24.51, -36.6) * mm});
            skLineSegment(sketch, "E479", {"start": v(-24.51, -36.6) * mm, "end": v(-26.86, -36.6) * mm});
            skArc(sketch, "E480", {"start": v(-27.37, -36.1) * mm, "mid": v(-27.22, -36.45) * mm, "end": v(-26.86, -36.6) * mm});
            skLineSegment(sketch, "E481", {"start": v(-27.37, -36.1) * mm, "end": v(-27.37, -35.6) * mm});
            skArc(sketch, "E482", {"start": v(-26.86, -35.1) * mm, "mid": v(-27.22, -35.25) * mm, "end": v(-27.37, -35.6) * mm});
            skLineSegment(sketch, "E483", {"start": v(-13.14, -35.1) * mm, "end": v(-26.86, -35.1) * mm});
            skArc(sketch, "E484", {"start": v(-13.14, -35.1) * mm, "mid": v(-12.78, -35.25) * mm, "end": v(-12.63, -35.6) * mm});
            skLineSegment(sketch, "E485", {"start": v(-12.63, -36.1) * mm, "end": v(-12.63, -35.6) * mm});
            skArc(sketch, "E486", {"start": v(-12.63, -36.1) * mm, "mid": v(-12.78, -36.45) * mm, "end": v(-13.14, -36.6) * mm});
            skLineSegment(sketch, "E487", {"start": v(-15.49, -36.6) * mm, "end": v(-13.14, -36.6) * mm});
            skArc(sketch, "E488", {"start": v(-16, -37.1) * mm, "mid": v(-15.85, -36.75) * mm, "end": v(-15.49, -36.6) * mm});
            skLineSegment(sketch, "E489", {"start": v(-16, -37.1) * mm, "end": v(-16, -37.83) * mm});
            skArc(sketch, "E490", {"start": v(-15.85, -38.2) * mm, "mid": v(-15.96, -38.03) * mm, "end": v(-16, -37.83) * mm});
            skLineSegment(sketch, "E491", {"start": v(-12.74, -41.3) * mm, "end": v(-15.85, -38.2) * mm});
            skArc(sketch, "E492", {"start": v(-12.38, -41.44) * mm, "mid": v(-12.58, -41.4) * mm, "end": v(-12.74, -41.3) * mm});
            skLineSegment(sketch, "E493", {"start": v(-7.62, -41.44) * mm, "end": v(-12.38, -41.44) * mm});
            skArc(sketch, "E494", {"start": v(-7.26, -41.3) * mm, "mid": v(-7.42, -41.4) * mm, "end": v(-7.62, -41.44) * mm});
            skLineSegment(sketch, "E495", {"start": v(-4.15, -38.2) * mm, "end": v(-7.26, -41.3) * mm});
            skArc(sketch, "E496", {"start": v(-4, -37.83) * mm, "mid": v(-4.04, -38.03) * mm, "end": v(-4.15, -38.2) * mm});
            skLineSegment(sketch, "E497", {"start": v(-4, -37.1) * mm, "end": v(-4, -37.83) * mm});
            skArc(sketch, "E498", {"start": v(-4.51, -36.6) * mm, "mid": v(-4.15, -36.75) * mm, "end": v(-4, -37.1) * mm});
            skLineSegment(sketch, "E499", {"start": v(-6.86, -36.6) * mm, "end": v(-4.51, -36.6) * mm});
            skArc(sketch, "E500", {"start": v(-6.86, -36.6) * mm, "mid": v(-7.22, -36.45) * mm, "end": v(-7.37, -36.1) * mm});
            skLineSegment(sketch, "E501", {"start": v(-7.37, -35.6) * mm, "end": v(-7.37, -36.1) * mm});
            skArc(sketch, "E502", {"start": v(-7.37, -35.6) * mm, "mid": v(-7.22, -35.25) * mm, "end": v(-6.86, -35.1) * mm});
            skLineSegment(sketch, "E503", {"start": v(1.5, -35.1) * mm, "end": v(-6.86, -35.1) * mm});
            skArc(sketch, "E504", {"start": v(-1, -42.47) * mm, "mid": v(-1.35, -42.32) * mm, "end": v(-1.5, -41.96) * mm});
            skLineSegment(sketch, "E505", {"start": v(-1.5, -39.61) * mm, "end": v(-1.5, -41.96) * mm});
            skArc(sketch, "E506", {"start": v(-2, -39.1) * mm, "mid": v(-1.65, -39.25) * mm, "end": v(-1.5, -39.61) * mm});
            skLineSegment(sketch, "E507", {"start": v(-2.73, -39.1) * mm, "end": v(-2, -39.1) * mm});
            skArc(sketch, "E508", {"start": v(-3.1, -39.25) * mm, "mid": v(-2.93, -39.14) * mm, "end": v(-2.73, -39.1) * mm});
            skLineSegment(sketch, "E509", {"start": v(-6.2, -42.36) * mm, "end": v(-3.1, -39.25) * mm});
            skArc(sketch, "E510", {"start": v(-6.35, -42.72) * mm, "mid": v(-6.3, -42.52) * mm, "end": v(-6.2, -42.36) * mm});
            skLineSegment(sketch, "E511", {"start": v(-6.35, -42.72) * mm, "end": v(-6.35, -47.48) * mm});
            skArc(sketch, "E512", {"start": v(-6.2, -47.84) * mm, "mid": v(-6.3, -47.68) * mm, "end": v(-6.35, -47.48) * mm});
            skLineSegment(sketch, "E513", {"start": v(-6.2, -47.84) * mm, "end": v(-3.1, -50.95) * mm});
            skArc(sketch, "E514", {"start": v(-2.73, -51.1) * mm, "mid": v(-2.93, -51.06) * mm, "end": v(-3.1, -50.95) * mm});
            skLineSegment(sketch, "E515", {"start": v(-2.73, -51.1) * mm, "end": v(-2, -51.1) * mm});
            skArc(sketch, "E516", {"start": v(-1.5, -50.59) * mm, "mid": v(-1.65, -50.95) * mm, "end": v(-2, -51.1) * mm});
            skLineSegment(sketch, "E517", {"start": v(-1.5, -50.59) * mm, "end": v(-1.5, -48.24) * mm});
            skArc(sketch, "E518", {"start": v(-1.5, -48.24) * mm, "mid": v(-1.35, -47.88) * mm, "end": v(-1, -47.73) * mm});
            skLineSegment(sketch, "E519", {"start": v(-0.5, -47.73) * mm, "end": v(-1, -47.73) * mm});
            skLineSegment(sketch, "E520", {"start": v(-1.5, -55.1) * mm, "end": v(-6.86, -55.1) * mm});
            skArc(sketch, "E521", {"start": v(-6.86, -55.1) * mm, "mid": v(-7.22, -54.95) * mm, "end": v(-7.37, -54.6) * mm});
            skArc(sketch, "E522", {"start": v(-13.66, -42.72) * mm, "mid": v(-13.7, -42.52) * mm, "end": v(-13.8, -42.36) * mm});
            skLineSegment(sketch, "E523", {"start": v(-13.8, -42.36) * mm, "end": v(-17.35, -38.81) * mm});
            skArc(sketch, "E524", {"start": v(-17.35, -38.81) * mm, "mid": v(-17.46, -38.65) * mm, "end": v(-17.5, -38.46) * mm});
            skLineSegment(sketch, "E525", {"start": v(-17.5, -37.1) * mm, "end": v(-17.5, -38.46) * mm});
            skArc(sketch, "E526", {"start": v(-18, -36.6) * mm, "mid": v(-17.64, -36.75) * mm, "end": v(-17.5, -37.1) * mm});
            skLineSegment(sketch, "E527", {"start": v(-22, -36.6) * mm, "end": v(-18, -36.6) * mm});
            skArc(sketch, "E528", {"start": v(-22, -36.6) * mm, "mid": v(-22.36, -36.75) * mm, "end": v(-22.5, -37.1) * mm});
            skLineSegment(sketch, "E529", {"start": v(-22.5, -37.1) * mm, "end": v(-22.5, -38.46) * mm});
            skArc(sketch, "E530", {"start": v(-22.65, -38.81) * mm, "mid": v(-22.54, -38.65) * mm, "end": v(-22.5, -38.46) * mm});
            skLineSegment(sketch, "E531", {"start": v(-26.2, -42.36) * mm, "end": v(-22.65, -38.81) * mm});
            skArc(sketch, "E532", {"start": v(-26.2, -42.36) * mm, "mid": v(-26.3, -42.52) * mm, "end": v(-26.35, -42.72) * mm});
            skLineSegment(sketch, "E533", {"start": v(-26.35, -42.72) * mm, "end": v(-26.35, -47.48) * mm});
            skArc(sketch, "E534", {"start": v(-26.35, -47.48) * mm, "mid": v(-26.3, -47.68) * mm, "end": v(-26.2, -47.84) * mm});
            skLineSegment(sketch, "E535", {"start": v(-26.2, -47.84) * mm, "end": v(-22.65, -51.39) * mm});
            skArc(sketch, "E536", {"start": v(-22.5, -51.74) * mm, "mid": v(-22.54, -51.55) * mm, "end": v(-22.65, -51.39) * mm});
            skLineSegment(sketch, "E537", {"start": v(-22.5, -51.74) * mm, "end": v(-22.5, -53.1) * mm});
            skArc(sketch, "E538", {"start": v(-22.5, -53.1) * mm, "mid": v(-22.36, -53.45) * mm, "end": v(-22, -53.6) * mm});
            skLineSegment(sketch, "E539", {"start": v(-22, -53.6) * mm, "end": v(-18, -53.6) * mm});
            skArc(sketch, "E540", {"start": v(-17.5, -53.1) * mm, "mid": v(-17.64, -53.45) * mm, "end": v(-18, -53.6) * mm});
            skLineSegment(sketch, "E541", {"start": v(-17.5, -51.74) * mm, "end": v(-17.5, -53.1) * mm});
            skArc(sketch, "E542", {"start": v(-17.5, -51.74) * mm, "mid": v(-17.46, -51.55) * mm, "end": v(-17.35, -51.39) * mm});
            skLineSegment(sketch, "E543", {"start": v(-13.8, -47.84) * mm, "end": v(-17.35, -51.39) * mm});
            skArc(sketch, "E544", {"start": v(-13.66, -47.48) * mm, "mid": v(-13.7, -47.68) * mm, "end": v(-13.8, -47.84) * mm});
            skLineSegment(sketch, "E545", {"start": v(13.66, -42.72) * mm, "end": v(13.66, -47.48) * mm});
            skArc(sketch, "E546", {"start": v(7.88, -42.8) * mm, "mid": v(8.64, -42.6) * mm, "end": v(9.2, -43.16) * mm});
            skLineSegment(sketch, "E547", {"start": v(27.88, -42.8) * mm, "end": v(27.7, -42.98) * mm});
            skLineSegment(sketch, "E548", {"start": v(7.37, -54.1) * mm, "end": v(7.37, -54.6) * mm});
            skArc(sketch, "E549", {"start": v(9.2, -43.16) * mm, "mid": v(10, -43) * mm, "end": v(10.8, -43.16) * mm});
            skArc(sketch, "E550", {"start": v(10.8, -43.16) * mm, "mid": v(11.36, -42.6) * mm, "end": v(12.12, -42.8) * mm});
            skLineSegment(sketch, "E551", {"start": v(12.12, -42.8) * mm, "end": v(12.3, -42.98) * mm});
            skArc(sketch, "E552", {"start": v(12.3, -42.98) * mm, "mid": v(12.5, -43.74) * mm, "end": v(11.94, -44.3) * mm});
            skArc(sketch, "E553", {"start": v(11.94, -44.3) * mm, "mid": v(12.1, -45.1) * mm, "end": v(11.94, -45.9) * mm});
            skArc(sketch, "E554", {"start": v(11.94, -45.9) * mm, "mid": v(12.5, -46.46) * mm, "end": v(12.3, -47.22) * mm});
            skLineSegment(sketch, "E555", {"start": v(12.3, -47.22) * mm, "end": v(12.12, -47.4) * mm});
            skArc(sketch, "E556", {"start": v(12.12, -47.4) * mm, "mid": v(11.36, -47.6) * mm, "end": v(10.8, -47.04) * mm});
            skArc(sketch, "E557", {"start": v(10.8, -47.04) * mm, "mid": v(10, -47.2) * mm, "end": v(9.2, -47.04) * mm});
            skArc(sketch, "E558", {"start": v(9.2, -47.04) * mm, "mid": v(8.64, -47.6) * mm, "end": v(7.88, -47.4) * mm});
            skLineSegment(sketch, "E559", {"start": v(7.88, -47.4) * mm, "end": v(7.7, -47.22) * mm});
            skArc(sketch, "E560", {"start": v(7.7, -47.22) * mm, "mid": v(7.5, -46.46) * mm, "end": v(8.06, -45.9) * mm});
            skArc(sketch, "E561", {"start": v(8.06, -45.9) * mm, "mid": v(7.9, -45.1) * mm, "end": v(8.06, -44.3) * mm});
            skArc(sketch, "E562", {"start": v(8.06, -44.3) * mm, "mid": v(7.5, -43.74) * mm, "end": v(7.7, -42.98) * mm});
            skLineSegment(sketch, "E563", {"start": v(7.7, -42.98) * mm, "end": v(7.88, -42.8) * mm});
            skArc(sketch, "E564", {"start": v(29.2, -43.16) * mm, "mid": v(28.64, -42.6) * mm, "end": v(27.88, -42.8) * mm});
            skArc(sketch, "E565", {"start": v(30.8, -43.16) * mm, "mid": v(30, -43) * mm, "end": v(29.2, -43.16) * mm});
            skArc(sketch, "E566", {"start": v(32.12, -42.8) * mm, "mid": v(31.36, -42.6) * mm, "end": v(30.8, -43.16) * mm});
            skLineSegment(sketch, "E567", {"start": v(32.3, -42.98) * mm, "end": v(32.12, -42.8) * mm});
            skArc(sketch, "E568", {"start": v(31.94, -44.3) * mm, "mid": v(32.5, -43.74) * mm, "end": v(32.3, -42.98) * mm});
            skArc(sketch, "E569", {"start": v(31.94, -45.9) * mm, "mid": v(32.1, -45.1) * mm, "end": v(31.94, -44.3) * mm});
            skArc(sketch, "E570", {"start": v(32.3, -47.22) * mm, "mid": v(32.5, -46.46) * mm, "end": v(31.94, -45.9) * mm});
            skLineSegment(sketch, "E571", {"start": v(32.12, -47.4) * mm, "end": v(32.3, -47.22) * mm});
            skArc(sketch, "E572", {"start": v(30.8, -47.04) * mm, "mid": v(31.36, -47.6) * mm, "end": v(32.12, -47.4) * mm});
            skArc(sketch, "E573", {"start": v(29.2, -47.04) * mm, "mid": v(30, -47.2) * mm, "end": v(30.8, -47.04) * mm});
            skArc(sketch, "E574", {"start": v(27.88, -47.4) * mm, "mid": v(28.64, -47.6) * mm, "end": v(29.2, -47.04) * mm});
            skLineSegment(sketch, "E575", {"start": v(27.7, -47.22) * mm, "end": v(27.88, -47.4) * mm});
            skArc(sketch, "E576", {"start": v(28.06, -45.9) * mm, "mid": v(27.5, -46.46) * mm, "end": v(27.7, -47.22) * mm});
            skArc(sketch, "E577", {"start": v(28.06, -44.3) * mm, "mid": v(27.9, -45.1) * mm, "end": v(28.06, -45.9) * mm});
            skArc(sketch, "E578", {"start": v(27.7, -42.98) * mm, "mid": v(27.5, -43.74) * mm, "end": v(28.06, -44.3) * mm});
            skArc(sketch, "E579", {"start": v(6.86, -53.6) * mm, "mid": v(7.22, -53.75) * mm, "end": v(7.37, -54.1) * mm});
            skLineSegment(sketch, "E580", {"start": v(6.86, -53.6) * mm, "end": v(4.51, -53.6) * mm});
            skArc(sketch, "E581", {"start": v(4.51, -53.6) * mm, "mid": v(4.15, -53.45) * mm, "end": v(4, -53.1) * mm});
            skLineSegment(sketch, "E582", {"start": v(4, -52.37) * mm, "end": v(4, -53.1) * mm});
            skArc(sketch, "E583", {"start": v(4, -52.37) * mm, "mid": v(4.04, -52.17) * mm, "end": v(4.15, -52) * mm});
            skLineSegment(sketch, "E584", {"start": v(4.15, -52) * mm, "end": v(7.26, -48.9) * mm});
            skArc(sketch, "E585", {"start": v(7.26, -48.9) * mm, "mid": v(7.42, -48.8) * mm, "end": v(7.62, -48.76) * mm});
            skLineSegment(sketch, "E586", {"start": v(7.62, -48.75) * mm, "end": v(12.38, -48.75) * mm});
            skArc(sketch, "E587", {"start": v(12.38, -48.76) * mm, "mid": v(12.58, -48.8) * mm, "end": v(12.74, -48.9) * mm});
            skLineSegment(sketch, "E588", {"start": v(12.74, -48.9) * mm, "end": v(15.85, -52) * mm});
            skArc(sketch, "E589", {"start": v(15.85, -52) * mm, "mid": v(15.96, -52.17) * mm, "end": v(16, -52.37) * mm});
            skLineSegment(sketch, "E590", {"start": v(16, -52.37) * mm, "end": v(16, -53.1) * mm});
            skArc(sketch, "E591", {"start": v(16, -53.1) * mm, "mid": v(15.85, -53.45) * mm, "end": v(15.49, -53.6) * mm});
            skLineSegment(sketch, "E592", {"start": v(15.49, -53.6) * mm, "end": v(13.14, -53.6) * mm});
            skArc(sketch, "E593", {"start": v(12.63, -54.1) * mm, "mid": v(12.78, -53.75) * mm, "end": v(13.14, -53.6) * mm});
            skLineSegment(sketch, "E594", {"start": v(12.63, -54.6) * mm, "end": v(12.63, -54.1) * mm});
            skArc(sketch, "E595", {"start": v(13.14, -55.1) * mm, "mid": v(12.78, -54.95) * mm, "end": v(12.63, -54.6) * mm});
            skLineSegment(sketch, "E596", {"start": v(26.86, -55.1) * mm, "end": v(13.14, -55.1) * mm});
            skArc(sketch, "E597", {"start": v(26.86, -55.1) * mm, "mid": v(27.22, -54.95) * mm, "end": v(27.37, -54.6) * mm});
            skLineSegment(sketch, "E598", {"start": v(27.37, -54.6) * mm, "end": v(27.37, -54.1) * mm});
            skArc(sketch, "E599", {"start": v(27.37, -54.1) * mm, "mid": v(27.22, -53.75) * mm, "end": v(26.86, -53.6) * mm});
            skLineSegment(sketch, "E600", {"start": v(24.51, -53.6) * mm, "end": v(26.86, -53.6) * mm});
            skArc(sketch, "E601", {"start": v(24, -53.1) * mm, "mid": v(24.15, -53.45) * mm, "end": v(24.51, -53.6) * mm});
            skLineSegment(sketch, "E602", {"start": v(24, -52.37) * mm, "end": v(24, -53.1) * mm});
            skArc(sketch, "E603", {"start": v(24.15, -52) * mm, "mid": v(24.04, -52.17) * mm, "end": v(24, -52.37) * mm});
            skLineSegment(sketch, "E604", {"start": v(27.26, -48.9) * mm, "end": v(24.15, -52) * mm});
            skArc(sketch, "E605", {"start": v(27.62, -48.76) * mm, "mid": v(27.42, -48.8) * mm, "end": v(27.26, -48.9) * mm});
            skLineSegment(sketch, "E606", {"start": v(32.38, -48.75) * mm, "end": v(27.62, -48.75) * mm});
            skArc(sketch, "E607", {"start": v(32.74, -48.9) * mm, "mid": v(32.58, -48.8) * mm, "end": v(32.38, -48.76) * mm});
            skLineSegment(sketch, "E608", {"start": v(35.85, -52) * mm, "end": v(32.74, -48.9) * mm});
            skArc(sketch, "E609", {"start": v(36, -52.37) * mm, "mid": v(35.96, -52.17) * mm, "end": v(35.85, -52) * mm});
            skLineSegment(sketch, "E610", {"start": v(36, -52.37) * mm, "end": v(36, -53.1) * mm});
            skArc(sketch, "E611", {"start": v(35.49, -53.6) * mm, "mid": v(35.85, -53.45) * mm, "end": v(36, -53.1) * mm});
            skLineSegment(sketch, "E612", {"start": v(33.14, -53.6) * mm, "end": v(35.49, -53.6) * mm});
            skArc(sketch, "E613", {"start": v(33.14, -53.6) * mm, "mid": v(32.78, -53.75) * mm, "end": v(32.63, -54.1) * mm});
            skLineSegment(sketch, "E614", {"start": v(32.63, -54.1) * mm, "end": v(32.63, -54.6) * mm});
            skArc(sketch, "E615", {"start": v(32.63, -54.6) * mm, "mid": v(32.78, -54.95) * mm, "end": v(33.14, -55.1) * mm});
            skLineSegment(sketch, "E616", {"start": v(38.5, -55.1) * mm, "end": v(33.14, -55.1) * mm});
            skArc(sketch, "E617", {"start": v(38.5, -55.1) * mm, "mid": v(39.56, -54.66) * mm, "end": v(40, -53.6) * mm});
            skLineSegment(sketch, "E618", {"start": v(40, -53.6) * mm, "end": v(40, -48.24) * mm});
            skArc(sketch, "E619", {"start": v(40, -48.24) * mm, "mid": v(39.85, -47.88) * mm, "end": v(39.5, -47.73) * mm});
            skLineSegment(sketch, "E620", {"start": v(39.5, -47.73) * mm, "end": v(39, -47.73) * mm});
            skArc(sketch, "E621", {"start": v(39, -47.73) * mm, "mid": v(38.65, -47.88) * mm, "end": v(38.5, -48.24) * mm});
            skLineSegment(sketch, "E622", {"start": v(38.5, -50.59) * mm, "end": v(38.5, -48.24) * mm});
            skArc(sketch, "E623", {"start": v(38, -51.1) * mm, "mid": v(38.35, -50.95) * mm, "end": v(38.5, -50.59) * mm});
            skLineSegment(sketch, "E624", {"start": v(37.27, -51.1) * mm, "end": v(38, -51.1) * mm});
            skArc(sketch, "E625", {"start": v(36.9, -50.95) * mm, "mid": v(37.07, -51.06) * mm, "end": v(37.27, -51.1) * mm});
            skLineSegment(sketch, "E626", {"start": v(33.8, -47.84) * mm, "end": v(36.9, -50.95) * mm});
            skArc(sketch, "E627", {"start": v(33.66, -47.48) * mm, "mid": v(33.7, -47.68) * mm, "end": v(33.8, -47.84) * mm});
            skLineSegment(sketch, "E628", {"start": v(33.66, -42.72) * mm, "end": v(33.66, -47.48) * mm});
            skArc(sketch, "E629", {"start": v(33.8, -42.36) * mm, "mid": v(33.7, -42.52) * mm, "end": v(33.66, -42.72) * mm});
            skLineSegment(sketch, "E630", {"start": v(33.8, -42.36) * mm, "end": v(36.9, -39.25) * mm});
            skArc(sketch, "E631", {"start": v(37.27, -39.1) * mm, "mid": v(37.07, -39.14) * mm, "end": v(36.9, -39.25) * mm});
            skLineSegment(sketch, "E632", {"start": v(37.27, -39.1) * mm, "end": v(38, -39.1) * mm});
            skArc(sketch, "E633", {"start": v(38.5, -39.61) * mm, "mid": v(38.35, -39.25) * mm, "end": v(38, -39.1) * mm});
            skLineSegment(sketch, "E634", {"start": v(38.5, -39.61) * mm, "end": v(38.5, -41.96) * mm});
            skArc(sketch, "E635", {"start": v(38.5, -41.96) * mm, "mid": v(38.65, -42.32) * mm, "end": v(39, -42.47) * mm});
            skLineSegment(sketch, "E636", {"start": v(39, -42.47) * mm, "end": v(39.5, -42.47) * mm});
            skArc(sketch, "E637", {"start": v(39.5, -42.47) * mm, "mid": v(39.85, -42.32) * mm, "end": v(40, -41.96) * mm});
            skLineSegment(sketch, "E638", {"start": v(40, -41.96) * mm, "end": v(40, -36.6) * mm});
            skArc(sketch, "E639", {"start": v(40, -36.6) * mm, "mid": v(39.56, -35.54) * mm, "end": v(38.5, -35.1) * mm});
            skLineSegment(sketch, "E640", {"start": v(38.5, -35.1) * mm, "end": v(33.14, -35.1) * mm});
            skArc(sketch, "E641", {"start": v(33.14, -35.1) * mm, "mid": v(32.78, -35.25) * mm, "end": v(32.63, -35.6) * mm});
            skLineSegment(sketch, "E642", {"start": v(32.63, -35.6) * mm, "end": v(32.63, -36.1) * mm});
            skArc(sketch, "E643", {"start": v(32.63, -36.1) * mm, "mid": v(32.78, -36.45) * mm, "end": v(33.14, -36.6) * mm});
            skLineSegment(sketch, "E644", {"start": v(33.14, -36.6) * mm, "end": v(35.49, -36.6) * mm});
            skArc(sketch, "E645", {"start": v(36, -37.1) * mm, "mid": v(35.85, -36.75) * mm, "end": v(35.49, -36.6) * mm});
            skLineSegment(sketch, "E646", {"start": v(36, -37.1) * mm, "end": v(36, -37.83) * mm});
            skArc(sketch, "E647", {"start": v(35.85, -38.2) * mm, "mid": v(35.96, -38.03) * mm, "end": v(36, -37.83) * mm});
            skLineSegment(sketch, "E648", {"start": v(35.85, -38.2) * mm, "end": v(32.74, -41.3) * mm});
            skArc(sketch, "E649", {"start": v(32.38, -41.44) * mm, "mid": v(32.58, -41.4) * mm, "end": v(32.74, -41.3) * mm});
            skLineSegment(sketch, "E650", {"start": v(32.38, -41.44) * mm, "end": v(27.62, -41.44) * mm});
            skArc(sketch, "E651", {"start": v(27.26, -41.3) * mm, "mid": v(27.42, -41.4) * mm, "end": v(27.62, -41.44) * mm});
            skLineSegment(sketch, "E652", {"start": v(27.26, -41.3) * mm, "end": v(24.15, -38.2) * mm});
            skArc(sketch, "E653", {"start": v(24, -37.83) * mm, "mid": v(24.04, -38.03) * mm, "end": v(24.15, -38.2) * mm});
            skLineSegment(sketch, "E654", {"start": v(24, -37.1) * mm, "end": v(24, -37.83) * mm});
            skArc(sketch, "E655", {"start": v(24.51, -36.6) * mm, "mid": v(24.15, -36.75) * mm, "end": v(24, -37.1) * mm});
            skLineSegment(sketch, "E656", {"start": v(24.51, -36.6) * mm, "end": v(26.86, -36.6) * mm});
            skArc(sketch, "E657", {"start": v(26.86, -36.6) * mm, "mid": v(27.22, -36.45) * mm, "end": v(27.37, -36.1) * mm});
            skLineSegment(sketch, "E658", {"start": v(27.37, -36.1) * mm, "end": v(27.37, -35.6) * mm});
            skArc(sketch, "E659", {"start": v(27.37, -35.6) * mm, "mid": v(27.22, -35.25) * mm, "end": v(26.86, -35.1) * mm});
            skLineSegment(sketch, "E660", {"start": v(13.14, -35.1) * mm, "end": v(26.86, -35.1) * mm});
            skArc(sketch, "E661", {"start": v(12.63, -35.6) * mm, "mid": v(12.78, -35.25) * mm, "end": v(13.14, -35.1) * mm});
            skLineSegment(sketch, "E662", {"start": v(12.63, -36.1) * mm, "end": v(12.63, -35.6) * mm});
            skArc(sketch, "E663", {"start": v(13.14, -36.6) * mm, "mid": v(12.78, -36.45) * mm, "end": v(12.63, -36.1) * mm});
            skLineSegment(sketch, "E664", {"start": v(15.49, -36.6) * mm, "end": v(13.14, -36.6) * mm});
            skArc(sketch, "E665", {"start": v(15.49, -36.6) * mm, "mid": v(15.85, -36.75) * mm, "end": v(16, -37.1) * mm});
            skLineSegment(sketch, "E666", {"start": v(16, -37.1) * mm, "end": v(16, -37.83) * mm});
            skArc(sketch, "E667", {"start": v(16, -37.83) * mm, "mid": v(15.96, -38.03) * mm, "end": v(15.85, -38.2) * mm});
            skLineSegment(sketch, "E668", {"start": v(12.74, -41.3) * mm, "end": v(15.85, -38.2) * mm});
            skArc(sketch, "E669", {"start": v(12.74, -41.3) * mm, "mid": v(12.58, -41.4) * mm, "end": v(12.38, -41.44) * mm});
            skLineSegment(sketch, "E670", {"start": v(7.62, -41.44) * mm, "end": v(12.38, -41.44) * mm});
            skArc(sketch, "E671", {"start": v(7.62, -41.44) * mm, "mid": v(7.42, -41.4) * mm, "end": v(7.26, -41.3) * mm});
            skLineSegment(sketch, "E672", {"start": v(4.15, -38.2) * mm, "end": v(7.26, -41.3) * mm});
            skArc(sketch, "E673", {"start": v(4.15, -38.2) * mm, "mid": v(4.04, -38.03) * mm, "end": v(4, -37.83) * mm});
            skLineSegment(sketch, "E674", {"start": v(4, -37.1) * mm, "end": v(4, -37.83) * mm});
            skArc(sketch, "E675", {"start": v(4, -37.1) * mm, "mid": v(4.15, -36.75) * mm, "end": v(4.51, -36.6) * mm});
            skLineSegment(sketch, "E676", {"start": v(6.86, -36.6) * mm, "end": v(4.51, -36.6) * mm});
            skArc(sketch, "E677", {"start": v(7.37, -36.1) * mm, "mid": v(7.22, -36.45) * mm, "end": v(6.86, -36.6) * mm});
            skLineSegment(sketch, "E678", {"start": v(7.37, -35.6) * mm, "end": v(7.37, -36.1) * mm});
            skArc(sketch, "E679", {"start": v(6.86, -35.1) * mm, "mid": v(7.22, -35.25) * mm, "end": v(7.37, -35.6) * mm});
            skLineSegment(sketch, "E680", {"start": v(1.5, -35.1) * mm, "end": v(6.86, -35.1) * mm});
            skArc(sketch, "E681", {"start": v(1.5, -41.96) * mm, "mid": v(1.35, -42.32) * mm, "end": v(1, -42.47) * mm});
            skLineSegment(sketch, "E682", {"start": v(1.5, -39.61) * mm, "end": v(1.5, -41.96) * mm});
            skArc(sketch, "E683", {"start": v(1.5, -39.61) * mm, "mid": v(1.65, -39.25) * mm, "end": v(2, -39.1) * mm});
            skLineSegment(sketch, "E684", {"start": v(2.73, -39.1) * mm, "end": v(2, -39.1) * mm});
            skArc(sketch, "E685", {"start": v(2.73, -39.1) * mm, "mid": v(2.93, -39.14) * mm, "end": v(3.1, -39.25) * mm});
            skLineSegment(sketch, "E686", {"start": v(6.2, -42.36) * mm, "end": v(3.1, -39.25) * mm});
            skArc(sketch, "E687", {"start": v(6.2, -42.36) * mm, "mid": v(6.3, -42.52) * mm, "end": v(6.34, -42.72) * mm});
            skLineSegment(sketch, "E688", {"start": v(6.34, -42.72) * mm, "end": v(6.34, -47.48) * mm});
            skArc(sketch, "E689", {"start": v(6.34, -47.48) * mm, "mid": v(6.3, -47.68) * mm, "end": v(6.2, -47.84) * mm});
            skLineSegment(sketch, "E690", {"start": v(6.2, -47.84) * mm, "end": v(3.1, -50.95) * mm});
            skArc(sketch, "E691", {"start": v(3.1, -50.95) * mm, "mid": v(2.93, -51.06) * mm, "end": v(2.73, -51.1) * mm});
            skLineSegment(sketch, "E692", {"start": v(2.73, -51.1) * mm, "end": v(2, -51.1) * mm});
            skArc(sketch, "E693", {"start": v(2, -51.1) * mm, "mid": v(1.65, -50.95) * mm, "end": v(1.5, -50.59) * mm});
            skLineSegment(sketch, "E694", {"start": v(1.5, -50.59) * mm, "end": v(1.5, -48.24) * mm});
            skArc(sketch, "E695", {"start": v(1, -47.73) * mm, "mid": v(1.35, -47.88) * mm, "end": v(1.5, -48.24) * mm});
            skLineSegment(sketch, "E696", {"start": v(0.5, -47.73) * mm, "end": v(1, -47.73) * mm});
            skLineSegment(sketch, "E697", {"start": v(-1.5, -55.1) * mm, "end": v(6.86, -55.1) * mm});
            skArc(sketch, "E698", {"start": v(7.37, -54.6) * mm, "mid": v(7.22, -54.95) * mm, "end": v(6.86, -55.1) * mm});
            skArc(sketch, "E699", {"start": v(13.8, -42.36) * mm, "mid": v(13.7, -42.52) * mm, "end": v(13.66, -42.72) * mm});
            skLineSegment(sketch, "E700", {"start": v(13.8, -42.36) * mm, "end": v(17.35, -38.81) * mm});
            skArc(sketch, "E701", {"start": v(17.5, -38.46) * mm, "mid": v(17.46, -38.65) * mm, "end": v(17.35, -38.81) * mm});
            skLineSegment(sketch, "E702", {"start": v(17.5, -37.1) * mm, "end": v(17.5, -38.46) * mm});
            skArc(sketch, "E703", {"start": v(17.5, -37.1) * mm, "mid": v(17.64, -36.75) * mm, "end": v(18, -36.6) * mm});
            skLineSegment(sketch, "E704", {"start": v(22, -36.6) * mm, "end": v(18, -36.6) * mm});
            skArc(sketch, "E705", {"start": v(22.5, -37.1) * mm, "mid": v(22.36, -36.75) * mm, "end": v(22, -36.6) * mm});
            skLineSegment(sketch, "E706", {"start": v(22.5, -37.1) * mm, "end": v(22.5, -38.46) * mm});
            skArc(sketch, "E707", {"start": v(22.5, -38.46) * mm, "mid": v(22.54, -38.65) * mm, "end": v(22.65, -38.81) * mm});
            skLineSegment(sketch, "E708", {"start": v(26.2, -42.36) * mm, "end": v(22.65, -38.81) * mm});
            skArc(sketch, "E709", {"start": v(26.34, -42.72) * mm, "mid": v(26.3, -42.52) * mm, "end": v(26.2, -42.36) * mm});
            skLineSegment(sketch, "E710", {"start": v(26.35, -42.72) * mm, "end": v(26.35, -47.48) * mm});
            skArc(sketch, "E711", {"start": v(26.2, -47.84) * mm, "mid": v(26.3, -47.68) * mm, "end": v(26.34, -47.48) * mm});
            skLineSegment(sketch, "E712", {"start": v(26.2, -47.84) * mm, "end": v(22.65, -51.39) * mm});
            skArc(sketch, "E713", {"start": v(22.65, -51.39) * mm, "mid": v(22.54, -51.55) * mm, "end": v(22.5, -51.74) * mm});
            skLineSegment(sketch, "E714", {"start": v(22.5, -51.74) * mm, "end": v(22.5, -53.1) * mm});
            skArc(sketch, "E715", {"start": v(22, -53.6) * mm, "mid": v(22.36, -53.45) * mm, "end": v(22.5, -53.1) * mm});
            skLineSegment(sketch, "E716", {"start": v(22, -53.6) * mm, "end": v(18, -53.6) * mm});
            skArc(sketch, "E717", {"start": v(18, -53.6) * mm, "mid": v(17.64, -53.45) * mm, "end": v(17.5, -53.1) * mm});
            skLineSegment(sketch, "E718", {"start": v(17.5, -51.74) * mm, "end": v(17.5, -53.1) * mm});
            skArc(sketch, "E719", {"start": v(17.35, -51.39) * mm, "mid": v(17.46, -51.55) * mm, "end": v(17.5, -51.74) * mm});
            skLineSegment(sketch, "E720", {"start": v(13.8, -47.84) * mm, "end": v(17.35, -51.39) * mm});
            skArc(sketch, "E721", {"start": v(13.8, -47.84) * mm, "mid": v(13.7, -47.68) * mm, "end": v(13.66, -47.48) * mm});
            skLineSegment(sketch, "E722", {"start": v(0.5, -47.73) * mm, "end": v(-0.5, -47.73) * mm});
            skLineSegment(sketch, "E723", {"start": v(1, -42.47) * mm, "end": v(-1, -42.47) * mm});
            skSolve(sketch);
        }
        {
            var Q0;
            Q0 = qSketchRegion(id + "F4", true);
            extrude(context, id + "F5", {"entities" : qUnion([Q0]), "depth" : 120 * mm, "offsetDistance" : 25 * mm});
        }
        {
            var Q0;
            Q0=qCreatedBy(makeId("Top.planeOp"),FACE);
            var sketch = newSketch(context, id + "F6", { "sketchPlane" : qUnion([Q0])});
            skLineSegment(sketch, "E724", {"start": v(-172.15, -125.87) * mm, "end": v(-172.15, -130.63) * mm});
            skArc(sketch, "E725", {"start": v(-167.7, -126.32) * mm, "mid": v(-167.14, -125.74) * mm, "end": v(-166.37, -125.95) * mm});
            skLineSegment(sketch, "E726", {"start": v(-186.37, -125.95) * mm, "end": v(-186.2, -126.13) * mm});
            skLineSegment(sketch, "E727", {"start": v(-165.87, -137.26) * mm, "end": v(-165.87, -137.74) * mm});
            skArc(sketch, "E728", {"start": v(-169.3, -126.32) * mm, "mid": v(-168.5, -126.15) * mm, "end": v(-167.7, -126.32) * mm});
            skArc(sketch, "E729", {"start": v(-170.62, -125.95) * mm, "mid": v(-169.85, -125.74) * mm, "end": v(-169.3, -126.32) * mm});
            skLineSegment(sketch, "E730", {"start": v(-170.62, -125.95) * mm, "end": v(-170.8, -126.13) * mm});
            skArc(sketch, "E731", {"start": v(-170.43, -127.45) * mm, "mid": v(-171, -126.9) * mm, "end": v(-170.8, -126.13) * mm});
            skArc(sketch, "E732", {"start": v(-170.43, -129.05) * mm, "mid": v(-170.6, -128.25) * mm, "end": v(-170.43, -127.45) * mm});
            skArc(sketch, "E733", {"start": v(-170.8, -130.38) * mm, "mid": v(-171, -129.6) * mm, "end": v(-170.43, -129.05) * mm});
            skLineSegment(sketch, "E734", {"start": v(-170.8, -130.38) * mm, "end": v(-170.62, -130.55) * mm});
            skArc(sketch, "E735", {"start": v(-169.3, -130.19) * mm, "mid": v(-169.85, -130.76) * mm, "end": v(-170.62, -130.55) * mm});
            skArc(sketch, "E736", {"start": v(-167.7, -130.19) * mm, "mid": v(-168.5, -130.35) * mm, "end": v(-169.3, -130.19) * mm});
            skArc(sketch, "E737", {"start": v(-166.37, -130.55) * mm, "mid": v(-167.14, -130.76) * mm, "end": v(-167.7, -130.19) * mm});
            skLineSegment(sketch, "E738", {"start": v(-166.37, -130.55) * mm, "end": v(-166.2, -130.38) * mm});
            skArc(sketch, "E739", {"start": v(-166.56, -129.05) * mm, "mid": v(-166, -129.6) * mm, "end": v(-166.2, -130.38) * mm});
            skArc(sketch, "E740", {"start": v(-166.56, -127.45) * mm, "mid": v(-166.4, -128.25) * mm, "end": v(-166.56, -129.05) * mm});
            skArc(sketch, "E741", {"start": v(-166.2, -126.13) * mm, "mid": v(-166, -126.9) * mm, "end": v(-166.56, -127.45) * mm});
            skLineSegment(sketch, "E742", {"start": v(-166.2, -126.13) * mm, "end": v(-166.37, -125.95) * mm});
            skArc(sketch, "E743", {"start": v(-186.37, -125.95) * mm, "mid": v(-187.14, -125.74) * mm, "end": v(-187.7, -126.32) * mm});
            skArc(sketch, "E744", {"start": v(-187.7, -126.32) * mm, "mid": v(-188.5, -126.15) * mm, "end": v(-189.3, -126.32) * mm});
            skArc(sketch, "E745", {"start": v(-189.3, -126.32) * mm, "mid": v(-189.85, -125.74) * mm, "end": v(-190.62, -125.95) * mm});
            skLineSegment(sketch, "E746", {"start": v(-190.8, -126.13) * mm, "end": v(-190.62, -125.95) * mm});
            skArc(sketch, "E747", {"start": v(-190.8, -126.13) * mm, "mid": v(-191, -126.9) * mm, "end": v(-190.43, -127.45) * mm});
            skArc(sketch, "E748", {"start": v(-190.43, -127.45) * mm, "mid": v(-190.6, -128.25) * mm, "end": v(-190.43, -129.05) * mm});
            skArc(sketch, "E749", {"start": v(-190.43, -129.05) * mm, "mid": v(-191, -129.6) * mm, "end": v(-190.8, -130.38) * mm});
            skLineSegment(sketch, "E750", {"start": v(-190.62, -130.55) * mm, "end": v(-190.8, -130.38) * mm});
            skArc(sketch, "E751", {"start": v(-190.62, -130.55) * mm, "mid": v(-189.85, -130.76) * mm, "end": v(-189.3, -130.19) * mm});
            skArc(sketch, "E752", {"start": v(-189.3, -130.19) * mm, "mid": v(-188.5, -130.35) * mm, "end": v(-187.7, -130.19) * mm});
            skArc(sketch, "E753", {"start": v(-187.7, -130.19) * mm, "mid": v(-187.14, -130.76) * mm, "end": v(-186.37, -130.55) * mm});
            skLineSegment(sketch, "E754", {"start": v(-186.2, -130.38) * mm, "end": v(-186.37, -130.55) * mm});
            skArc(sketch, "E755", {"start": v(-186.2, -130.38) * mm, "mid": v(-186, -129.6) * mm, "end": v(-186.56, -129.05) * mm});
            skArc(sketch, "E756", {"start": v(-186.56, -129.05) * mm, "mid": v(-186.4, -128.25) * mm, "end": v(-186.56, -127.45) * mm});
            skArc(sketch, "E757", {"start": v(-186.56, -127.45) * mm, "mid": v(-186, -126.9) * mm, "end": v(-186.2, -126.13) * mm});
            skArc(sketch, "E758", {"start": v(-165.87, -137.26) * mm, "mid": v(-165.72, -136.9) * mm, "end": v(-165.36, -136.75) * mm});
            skLineSegment(sketch, "E759", {"start": v(-165.36, -136.75) * mm, "end": v(-163, -136.75) * mm});
            skArc(sketch, "E760", {"start": v(-162.5, -136.24) * mm, "mid": v(-162.65, -136.6) * mm, "end": v(-163, -136.75) * mm});
            skLineSegment(sketch, "E761", {"start": v(-162.5, -135.52) * mm, "end": v(-162.5, -136.24) * mm});
            skArc(sketch, "E762", {"start": v(-162.65, -135.16) * mm, "mid": v(-162.54, -135.32) * mm, "end": v(-162.5, -135.52) * mm});
            skLineSegment(sketch, "E763", {"start": v(-162.65, -135.16) * mm, "end": v(-165.75, -132.05) * mm});
            skArc(sketch, "E764", {"start": v(-166.11, -131.9) * mm, "mid": v(-165.92, -131.94) * mm, "end": v(-165.75, -132.05) * mm});
            skLineSegment(sketch, "E765", {"start": v(-166.11, -131.9) * mm, "end": v(-170.88, -131.9) * mm});
            skArc(sketch, "E766", {"start": v(-171.24, -132.05) * mm, "mid": v(-171.07, -131.94) * mm, "end": v(-170.88, -131.9) * mm});
            skLineSegment(sketch, "E767", {"start": v(-171.24, -132.05) * mm, "end": v(-174.34, -135.16) * mm});
            skArc(sketch, "E768", {"start": v(-174.5, -135.52) * mm, "mid": v(-174.45, -135.32) * mm, "end": v(-174.34, -135.16) * mm});
            skLineSegment(sketch, "E769", {"start": v(-174.5, -135.52) * mm, "end": v(-174.5, -136.24) * mm});
            skArc(sketch, "E770", {"start": v(-173.98, -136.75) * mm, "mid": v(-174.34, -136.6) * mm, "end": v(-174.5, -136.24) * mm});
            skLineSegment(sketch, "E771", {"start": v(-173.98, -136.75) * mm, "end": v(-171.63, -136.75) * mm});
            skArc(sketch, "E772", {"start": v(-171.63, -136.75) * mm, "mid": v(-171.27, -136.9) * mm, "end": v(-171.13, -137.26) * mm});
            skLineSegment(sketch, "E773", {"start": v(-171.13, -137.74) * mm, "end": v(-171.13, -137.26) * mm});
            skArc(sketch, "E774", {"start": v(-171.13, -137.74) * mm, "mid": v(-171.27, -138.1) * mm, "end": v(-171.63, -138.25) * mm});
            skLineSegment(sketch, "E775", {"start": v(-185.36, -138.25) * mm, "end": v(-171.63, -138.25) * mm});
            skArc(sketch, "E776", {"start": v(-185.87, -137.74) * mm, "mid": v(-185.72, -138.1) * mm, "end": v(-185.36, -138.25) * mm});
            skLineSegment(sketch, "E777", {"start": v(-185.87, -137.74) * mm, "end": v(-185.87, -137.26) * mm});
            skArc(sketch, "E778", {"start": v(-185.36, -136.75) * mm, "mid": v(-185.72, -136.9) * mm, "end": v(-185.87, -137.26) * mm});
            skLineSegment(sketch, "E779", {"start": v(-183, -136.75) * mm, "end": v(-185.36, -136.75) * mm});
            skArc(sketch, "E780", {"start": v(-183, -136.75) * mm, "mid": v(-182.65, -136.6) * mm, "end": v(-182.5, -136.24) * mm});
            skLineSegment(sketch, "E781", {"start": v(-182.5, -135.52) * mm, "end": v(-182.5, -136.24) * mm});
            skArc(sketch, "E782", {"start": v(-182.5, -135.52) * mm, "mid": v(-182.54, -135.32) * mm, "end": v(-182.65, -135.16) * mm});
            skLineSegment(sketch, "E783", {"start": v(-185.75, -132.05) * mm, "end": v(-182.65, -135.16) * mm});
            skArc(sketch, "E784", {"start": v(-185.75, -132.05) * mm, "mid": v(-185.92, -131.94) * mm, "end": v(-186.11, -131.9) * mm});
            skLineSegment(sketch, "E785", {"start": v(-190.88, -131.9) * mm, "end": v(-186.11, -131.9) * mm});
            skArc(sketch, "E786", {"start": v(-190.88, -131.9) * mm, "mid": v(-191.07, -131.94) * mm, "end": v(-191.24, -132.05) * mm});
            skLineSegment(sketch, "E787", {"start": v(-194.34, -135.16) * mm, "end": v(-191.24, -132.05) * mm});
            skArc(sketch, "E788", {"start": v(-194.34, -135.16) * mm, "mid": v(-194.45, -135.32) * mm, "end": v(-194.5, -135.52) * mm});
            skLineSegment(sketch, "E789", {"start": v(-194.5, -135.52) * mm, "end": v(-194.5, -136.24) * mm});
            skArc(sketch, "E790", {"start": v(-194.5, -136.24) * mm, "mid": v(-194.34, -136.6) * mm, "end": v(-193.98, -136.75) * mm});
            skLineSegment(sketch, "E791", {"start": v(-191.63, -136.75) * mm, "end": v(-193.98, -136.75) * mm});
            skArc(sketch, "E792", {"start": v(-191.13, -137.26) * mm, "mid": v(-191.27, -136.9) * mm, "end": v(-191.63, -136.75) * mm});
            skLineSegment(sketch, "E793", {"start": v(-191.13, -137.26) * mm, "end": v(-191.13, -137.74) * mm});
            skArc(sketch, "E794", {"start": v(-191.63, -138.25) * mm, "mid": v(-191.27, -138.1) * mm, "end": v(-191.13, -137.74) * mm});
            skLineSegment(sketch, "E795", {"start": v(-197, -138.25) * mm, "end": v(-191.63, -138.25) * mm});
            skArc(sketch, "E796", {"start": v(-198.5, -136.75) * mm, "mid": v(-198.06, -137.81) * mm, "end": v(-197, -138.25) * mm});
            skLineSegment(sketch, "E797", {"start": v(-198.5, -136.75) * mm, "end": v(-198.5, -131.39) * mm});
            skArc(sketch, "E798", {"start": v(-197.99, -130.88) * mm, "mid": v(-198.35, -131.03) * mm, "end": v(-198.5, -131.39) * mm});
            skLineSegment(sketch, "E799", {"start": v(-197.99, -130.88) * mm, "end": v(-197.5, -130.88) * mm});
            skArc(sketch, "E800", {"start": v(-197, -131.39) * mm, "mid": v(-197.14, -131.03) * mm, "end": v(-197.5, -130.88) * mm});
            skLineSegment(sketch, "E801", {"start": v(-197, -133.74) * mm, "end": v(-197, -131.39) * mm});
            skArc(sketch, "E802", {"start": v(-197, -133.74) * mm, "mid": v(-196.85, -134.1) * mm, "end": v(-196.49, -134.25) * mm});
            skLineSegment(sketch, "E803", {"start": v(-195.76, -134.25) * mm, "end": v(-196.49, -134.25) * mm});
            skArc(sketch, "E804", {"start": v(-195.76, -134.25) * mm, "mid": v(-195.57, -134.2) * mm, "end": v(-195.4, -134.1) * mm});
            skLineSegment(sketch, "E805", {"start": v(-192.3, -131) * mm, "end": v(-195.4, -134.1) * mm});
            skArc(sketch, "E806", {"start": v(-192.3, -131) * mm, "mid": v(-192.19, -130.83) * mm, "end": v(-192.15, -130.63) * mm});
            skLineSegment(sketch, "E807", {"start": v(-192.15, -125.87) * mm, "end": v(-192.15, -130.63) * mm});
            skArc(sketch, "E808", {"start": v(-192.15, -125.87) * mm, "mid": v(-192.19, -125.67) * mm, "end": v(-192.3, -125.5) * mm});
            skLineSegment(sketch, "E809", {"start": v(-192.3, -125.5) * mm, "end": v(-195.4, -122.4) * mm});
            skArc(sketch, "E810", {"start": v(-195.4, -122.4) * mm, "mid": v(-195.57, -122.3) * mm, "end": v(-195.76, -122.26) * mm});
            skLineSegment(sketch, "E811", {"start": v(-195.76, -122.26) * mm, "end": v(-196.49, -122.26) * mm});
            skArc(sketch, "E812", {"start": v(-196.49, -122.26) * mm, "mid": v(-196.85, -122.4) * mm, "end": v(-197, -122.76) * mm});
            skLineSegment(sketch, "E813", {"start": v(-197, -122.76) * mm, "end": v(-197, -125.11) * mm});
            skArc(sketch, "E814", {"start": v(-197.5, -125.62) * mm, "mid": v(-197.14, -125.47) * mm, "end": v(-197, -125.11) * mm});
            skLineSegment(sketch, "E815", {"start": v(-197.5, -125.62) * mm, "end": v(-197.99, -125.62) * mm});
            skArc(sketch, "E816", {"start": v(-198.5, -125.11) * mm, "mid": v(-198.35, -125.47) * mm, "end": v(-197.99, -125.62) * mm});
            skLineSegment(sketch, "E817", {"start": v(-198.5, -125.11) * mm, "end": v(-198.5, -119.75) * mm});
            skArc(sketch, "E818", {"start": v(-197, -118.25) * mm, "mid": v(-198.06, -118.69) * mm, "end": v(-198.5, -119.75) * mm});
            skLineSegment(sketch, "E819", {"start": v(-197, -118.25) * mm, "end": v(-191.63, -118.25) * mm});
            skArc(sketch, "E820", {"start": v(-191.13, -118.76) * mm, "mid": v(-191.27, -118.4) * mm, "end": v(-191.63, -118.25) * mm});
            skLineSegment(sketch, "E821", {"start": v(-191.13, -118.76) * mm, "end": v(-191.13, -119.24) * mm});
            skArc(sketch, "E822", {"start": v(-191.63, -119.75) * mm, "mid": v(-191.27, -119.6) * mm, "end": v(-191.13, -119.24) * mm});
            skLineSegment(sketch, "E823", {"start": v(-191.63, -119.75) * mm, "end": v(-193.98, -119.75) * mm});
            skArc(sketch, "E824", {"start": v(-193.98, -119.75) * mm, "mid": v(-194.34, -119.9) * mm, "end": v(-194.5, -120.26) * mm});
            skLineSegment(sketch, "E825", {"start": v(-194.5, -120.26) * mm, "end": v(-194.5, -120.98) * mm});
            skArc(sketch, "E826", {"start": v(-194.5, -120.98) * mm, "mid": v(-194.45, -121.18) * mm, "end": v(-194.34, -121.34) * mm});
            skLineSegment(sketch, "E827", {"start": v(-194.34, -121.34) * mm, "end": v(-191.24, -124.45) * mm});
            skArc(sketch, "E828", {"start": v(-191.24, -124.45) * mm, "mid": v(-191.07, -124.56) * mm, "end": v(-190.88, -124.6) * mm});
            skLineSegment(sketch, "E829", {"start": v(-190.88, -124.6) * mm, "end": v(-186.11, -124.6) * mm});
            skArc(sketch, "E830", {"start": v(-186.11, -124.6) * mm, "mid": v(-185.92, -124.56) * mm, "end": v(-185.75, -124.45) * mm});
            skLineSegment(sketch, "E831", {"start": v(-185.75, -124.45) * mm, "end": v(-182.65, -121.34) * mm});
            skArc(sketch, "E832", {"start": v(-182.65, -121.34) * mm, "mid": v(-182.54, -121.18) * mm, "end": v(-182.5, -120.98) * mm});
            skLineSegment(sketch, "E833", {"start": v(-182.5, -120.26) * mm, "end": v(-182.5, -120.98) * mm});
            skArc(sketch, "E834", {"start": v(-182.5, -120.26) * mm, "mid": v(-182.65, -119.9) * mm, "end": v(-183, -119.75) * mm});
            skLineSegment(sketch, "E835", {"start": v(-183, -119.75) * mm, "end": v(-185.36, -119.75) * mm});
            skArc(sketch, "E836", {"start": v(-185.87, -119.24) * mm, "mid": v(-185.72, -119.6) * mm, "end": v(-185.36, -119.75) * mm});
            skLineSegment(sketch, "E837", {"start": v(-185.87, -119.24) * mm, "end": v(-185.87, -118.76) * mm});
            skArc(sketch, "E838", {"start": v(-185.36, -118.25) * mm, "mid": v(-185.72, -118.4) * mm, "end": v(-185.87, -118.76) * mm});
            skLineSegment(sketch, "E839", {"start": v(-171.63, -118.25) * mm, "end": v(-185.36, -118.25) * mm});
            skArc(sketch, "E840", {"start": v(-171.63, -118.25) * mm, "mid": v(-171.27, -118.4) * mm, "end": v(-171.13, -118.76) * mm});
            skLineSegment(sketch, "E841", {"start": v(-171.13, -119.24) * mm, "end": v(-171.13, -118.76) * mm});
            skArc(sketch, "E842", {"start": v(-171.13, -119.24) * mm, "mid": v(-171.27, -119.6) * mm, "end": v(-171.63, -119.75) * mm});
            skLineSegment(sketch, "E843", {"start": v(-173.98, -119.75) * mm, "end": v(-171.63, -119.75) * mm});
            skArc(sketch, "E844", {"start": v(-174.5, -120.26) * mm, "mid": v(-174.34, -119.9) * mm, "end": v(-173.98, -119.75) * mm});
            skLineSegment(sketch, "E845", {"start": v(-174.5, -120.26) * mm, "end": v(-174.5, -120.98) * mm});
            skArc(sketch, "E846", {"start": v(-174.34, -121.34) * mm, "mid": v(-174.45, -121.18) * mm, "end": v(-174.5, -120.98) * mm});
            skLineSegment(sketch, "E847", {"start": v(-171.24, -124.45) * mm, "end": v(-174.34, -121.34) * mm});
            skArc(sketch, "E848", {"start": v(-170.88, -124.6) * mm, "mid": v(-171.07, -124.56) * mm, "end": v(-171.24, -124.45) * mm});
            skLineSegment(sketch, "E849", {"start": v(-166.11, -124.6) * mm, "end": v(-170.88, -124.6) * mm});
            skArc(sketch, "E850", {"start": v(-165.75, -124.45) * mm, "mid": v(-165.92, -124.56) * mm, "end": v(-166.11, -124.6) * mm});
            skLineSegment(sketch, "E851", {"start": v(-162.65, -121.34) * mm, "end": v(-165.75, -124.45) * mm});
            skArc(sketch, "E852", {"start": v(-162.5, -120.98) * mm, "mid": v(-162.54, -121.18) * mm, "end": v(-162.65, -121.34) * mm});
            skLineSegment(sketch, "E853", {"start": v(-162.5, -120.26) * mm, "end": v(-162.5, -120.98) * mm});
            skArc(sketch, "E854", {"start": v(-163, -119.75) * mm, "mid": v(-162.65, -119.9) * mm, "end": v(-162.5, -120.26) * mm});
            skLineSegment(sketch, "E855", {"start": v(-165.36, -119.75) * mm, "end": v(-163, -119.75) * mm});
            skArc(sketch, "E856", {"start": v(-165.36, -119.75) * mm, "mid": v(-165.72, -119.6) * mm, "end": v(-165.87, -119.24) * mm});
            skLineSegment(sketch, "E857", {"start": v(-165.87, -118.76) * mm, "end": v(-165.87, -119.24) * mm});
            skArc(sketch, "E858", {"start": v(-165.87, -118.76) * mm, "mid": v(-165.72, -118.4) * mm, "end": v(-165.36, -118.25) * mm});
            skLineSegment(sketch, "E859", {"start": v(-160, -118.25) * mm, "end": v(-165.36, -118.25) * mm});
            skArc(sketch, "E860", {"start": v(-160, -118.25) * mm, "mid": v(-158.94, -118.69) * mm, "end": v(-158.5, -119.75) * mm});
            skLineSegment(sketch, "E861", {"start": v(-158.5, -125.11) * mm, "end": v(-158.5, -119.75) * mm});
            skArc(sketch, "E862", {"start": v(-158.5, -125.11) * mm, "mid": v(-158.64, -125.47) * mm, "end": v(-159, -125.62) * mm});
            skLineSegment(sketch, "E863", {"start": v(-159.49, -125.62) * mm, "end": v(-159, -125.62) * mm});
            skArc(sketch, "E864", {"start": v(-159.49, -125.62) * mm, "mid": v(-159.85, -125.47) * mm, "end": v(-160, -125.11) * mm});
            skLineSegment(sketch, "E865", {"start": v(-160, -122.76) * mm, "end": v(-160, -125.11) * mm});
            skArc(sketch, "E866", {"start": v(-160.5, -122.26) * mm, "mid": v(-160.14, -122.4) * mm, "end": v(-160, -122.76) * mm});
            skLineSegment(sketch, "E867", {"start": v(-161.23, -122.26) * mm, "end": v(-160.5, -122.26) * mm});
            skArc(sketch, "E868", {"start": v(-161.59, -122.4) * mm, "mid": v(-161.42, -122.3) * mm, "end": v(-161.23, -122.26) * mm});
            skLineSegment(sketch, "E869", {"start": v(-164.7, -125.5) * mm, "end": v(-161.59, -122.4) * mm});
            skArc(sketch, "E870", {"start": v(-164.84, -125.87) * mm, "mid": v(-164.8, -125.67) * mm, "end": v(-164.7, -125.5) * mm});
            skLineSegment(sketch, "E871", {"start": v(-164.84, -125.87) * mm, "end": v(-164.84, -130.63) * mm});
            skArc(sketch, "E872", {"start": v(-164.7, -131) * mm, "mid": v(-164.8, -130.83) * mm, "end": v(-164.84, -130.63) * mm});
            skLineSegment(sketch, "E873", {"start": v(-164.7, -131) * mm, "end": v(-161.59, -134.1) * mm});
            skArc(sketch, "E874", {"start": v(-161.23, -134.25) * mm, "mid": v(-161.42, -134.2) * mm, "end": v(-161.59, -134.1) * mm});
            skLineSegment(sketch, "E875", {"start": v(-161.23, -134.25) * mm, "end": v(-160.5, -134.25) * mm});
            skArc(sketch, "E876", {"start": v(-160, -133.74) * mm, "mid": v(-160.14, -134.1) * mm, "end": v(-160.5, -134.25) * mm});
            skLineSegment(sketch, "E877", {"start": v(-160, -133.74) * mm, "end": v(-160, -131.39) * mm});
            skArc(sketch, "E878", {"start": v(-160, -131.39) * mm, "mid": v(-159.85, -131.03) * mm, "end": v(-159.49, -130.88) * mm});
            skLineSegment(sketch, "E879", {"start": v(-159, -130.88) * mm, "end": v(-159.49, -130.88) * mm});
            skArc(sketch, "E880", {"start": v(-159, -130.88) * mm, "mid": v(-158.64, -131.03) * mm, "end": v(-158.5, -131.39) * mm});
            skLineSegment(sketch, "E881", {"start": v(-158.5, -136.75) * mm, "end": v(-158.5, -131.39) * mm});
            skArc(sketch, "E882", {"start": v(-158.5, -136.75) * mm, "mid": v(-158.94, -137.81) * mm, "end": v(-160, -138.25) * mm});
            skLineSegment(sketch, "E883", {"start": v(-160, -138.25) * mm, "end": v(-165.36, -138.25) * mm});
            skArc(sketch, "E884", {"start": v(-165.36, -138.25) * mm, "mid": v(-165.72, -138.1) * mm, "end": v(-165.87, -137.74) * mm});
            skArc(sketch, "E885", {"start": v(-172.15, -125.87) * mm, "mid": v(-172.19, -125.67) * mm, "end": v(-172.3, -125.5) * mm});
            skLineSegment(sketch, "E886", {"start": v(-172.3, -125.5) * mm, "end": v(-175.84, -121.96) * mm});
            skArc(sketch, "E887", {"start": v(-175.84, -121.96) * mm, "mid": v(-175.95, -121.8) * mm, "end": v(-176, -121.6) * mm});
            skLineSegment(sketch, "E888", {"start": v(-176, -120.26) * mm, "end": v(-176, -121.6) * mm});
            skArc(sketch, "E889", {"start": v(-176.5, -119.75) * mm, "mid": v(-176.14, -119.9) * mm, "end": v(-176, -120.26) * mm});
            skLineSegment(sketch, "E890", {"start": v(-180.5, -119.75) * mm, "end": v(-176.5, -119.75) * mm});
            skArc(sketch, "E891", {"start": v(-180.5, -119.75) * mm, "mid": v(-180.85, -119.9) * mm, "end": v(-181, -120.26) * mm});
            skLineSegment(sketch, "E892", {"start": v(-181, -120.26) * mm, "end": v(-181, -121.6) * mm});
            skArc(sketch, "E893", {"start": v(-181.15, -121.96) * mm, "mid": v(-181.04, -121.8) * mm, "end": v(-181, -121.6) * mm});
            skLineSegment(sketch, "E894", {"start": v(-184.7, -125.5) * mm, "end": v(-181.15, -121.96) * mm});
            skArc(sketch, "E895", {"start": v(-184.7, -125.5) * mm, "mid": v(-184.8, -125.67) * mm, "end": v(-184.84, -125.87) * mm});
            skLineSegment(sketch, "E896", {"start": v(-184.84, -125.87) * mm, "end": v(-184.84, -130.63) * mm});
            skArc(sketch, "E897", {"start": v(-184.84, -130.63) * mm, "mid": v(-184.8, -130.83) * mm, "end": v(-184.7, -131) * mm});
            skLineSegment(sketch, "E898", {"start": v(-184.7, -131) * mm, "end": v(-181.15, -134.54) * mm});
            skArc(sketch, "E899", {"start": v(-181, -134.9) * mm, "mid": v(-181.04, -134.7) * mm, "end": v(-181.15, -134.54) * mm});
            skLineSegment(sketch, "E900", {"start": v(-181, -134.9) * mm, "end": v(-181, -136.24) * mm});
            skArc(sketch, "E901", {"start": v(-181, -136.24) * mm, "mid": v(-180.85, -136.6) * mm, "end": v(-180.5, -136.75) * mm});
            skLineSegment(sketch, "E902", {"start": v(-180.5, -136.75) * mm, "end": v(-176.5, -136.75) * mm});
            skArc(sketch, "E903", {"start": v(-176, -136.24) * mm, "mid": v(-176.14, -136.6) * mm, "end": v(-176.5, -136.75) * mm});
            skLineSegment(sketch, "E904", {"start": v(-176, -134.9) * mm, "end": v(-176, -136.24) * mm});
            skArc(sketch, "E905", {"start": v(-176, -134.9) * mm, "mid": v(-175.95, -134.7) * mm, "end": v(-175.84, -134.54) * mm});
            skLineSegment(sketch, "E906", {"start": v(-172.3, -131) * mm, "end": v(-175.84, -134.54) * mm});
            skArc(sketch, "E907", {"start": v(-172.15, -130.63) * mm, "mid": v(-172.19, -130.83) * mm, "end": v(-172.3, -131) * mm});
            skSolve(sketch);
        }
        {
            var Q0;
            Q0 = qSketchRegion(id + "F6", true);
            extrude(context, id + "F7", {"entities" : qUnion([Q0]), "depth" : (1500 - 40) * mm, "offsetDistance" : 25 * mm});
        }
        {
            var Q0;
            Q0=qCreatedBy(makeId("Top.planeOp"),FACE);
            var sketch = newSketch(context, id + "F8", { "sketchPlane" : qUnion([Q0])});
            skLineSegment(sketch, "E908", {"start": v(-13.66, -100.62) * mm, "end": v(-13.66, -105.38) * mm});
            skArc(sketch, "E909", {"start": v(-9.2, -101.06) * mm, "mid": v(-8.64, -100.5) * mm, "end": v(-7.88, -100.7) * mm});
            skLineSegment(sketch, "E910", {"start": v(-27.88, -100.7) * mm, "end": v(-27.7, -100.88) * mm});
            skLineSegment(sketch, "E911", {"start": v(-7.37, -112) * mm, "end": v(-7.37, -112.5) * mm});
            skArc(sketch, "E912", {"start": v(-10.8, -101.06) * mm, "mid": v(-10, -100.9) * mm, "end": v(-9.2, -101.06) * mm});
            skArc(sketch, "E913", {"start": v(-12.12, -100.7) * mm, "mid": v(-11.36, -100.5) * mm, "end": v(-10.8, -101.06) * mm});
            skLineSegment(sketch, "E914", {"start": v(-12.12, -100.7) * mm, "end": v(-12.3, -100.88) * mm});
            skArc(sketch, "E915", {"start": v(-11.94, -102.2) * mm, "mid": v(-12.5, -101.64) * mm, "end": v(-12.3, -100.88) * mm});
            skArc(sketch, "E916", {"start": v(-11.94, -103.8) * mm, "mid": v(-12.1, -103) * mm, "end": v(-11.94, -102.2) * mm});
            skArc(sketch, "E917", {"start": v(-12.3, -105.12) * mm, "mid": v(-12.5, -104.36) * mm, "end": v(-11.94, -103.8) * mm});
            skLineSegment(sketch, "E918", {"start": v(-12.3, -105.12) * mm, "end": v(-12.12, -105.3) * mm});
            skArc(sketch, "E919", {"start": v(-10.8, -104.94) * mm, "mid": v(-11.36, -105.5) * mm, "end": v(-12.12, -105.3) * mm});
            skArc(sketch, "E920", {"start": v(-9.2, -104.94) * mm, "mid": v(-10, -105.1) * mm, "end": v(-10.8, -104.94) * mm});
            skArc(sketch, "E921", {"start": v(-7.88, -105.3) * mm, "mid": v(-8.64, -105.5) * mm, "end": v(-9.2, -104.94) * mm});
            skLineSegment(sketch, "E922", {"start": v(-7.88, -105.3) * mm, "end": v(-7.7, -105.12) * mm});
            skArc(sketch, "E923", {"start": v(-8.06, -103.8) * mm, "mid": v(-7.5, -104.36) * mm, "end": v(-7.7, -105.12) * mm});
            skArc(sketch, "E924", {"start": v(-8.06, -102.2) * mm, "mid": v(-7.9, -103) * mm, "end": v(-8.06, -103.8) * mm});
            skArc(sketch, "E925", {"start": v(-7.7, -100.88) * mm, "mid": v(-7.5, -101.64) * mm, "end": v(-8.06, -102.2) * mm});
            skLineSegment(sketch, "E926", {"start": v(-7.7, -100.88) * mm, "end": v(-7.88, -100.7) * mm});
            skArc(sketch, "E927", {"start": v(-27.88, -100.7) * mm, "mid": v(-28.64, -100.5) * mm, "end": v(-29.2, -101.06) * mm});
            skArc(sketch, "E928", {"start": v(-29.2, -101.06) * mm, "mid": v(-30, -100.9) * mm, "end": v(-30.8, -101.06) * mm});
            skArc(sketch, "E929", {"start": v(-30.8, -101.06) * mm, "mid": v(-31.36, -100.5) * mm, "end": v(-32.12, -100.7) * mm});
            skLineSegment(sketch, "E930", {"start": v(-32.3, -100.88) * mm, "end": v(-32.12, -100.7) * mm});
            skArc(sketch, "E931", {"start": v(-32.3, -100.88) * mm, "mid": v(-32.5, -101.64) * mm, "end": v(-31.94, -102.2) * mm});
            skArc(sketch, "E932", {"start": v(-31.94, -102.2) * mm, "mid": v(-32.1, -103) * mm, "end": v(-31.94, -103.8) * mm});
            skArc(sketch, "E933", {"start": v(-31.94, -103.8) * mm, "mid": v(-32.5, -104.36) * mm, "end": v(-32.3, -105.12) * mm});
            skLineSegment(sketch, "E934", {"start": v(-32.12, -105.3) * mm, "end": v(-32.3, -105.12) * mm});
            skArc(sketch, "E935", {"start": v(-32.12, -105.3) * mm, "mid": v(-31.36, -105.5) * mm, "end": v(-30.8, -104.94) * mm});
            skArc(sketch, "E936", {"start": v(-30.8, -104.94) * mm, "mid": v(-30, -105.1) * mm, "end": v(-29.2, -104.94) * mm});
            skArc(sketch, "E937", {"start": v(-29.2, -104.94) * mm, "mid": v(-28.64, -105.5) * mm, "end": v(-27.88, -105.3) * mm});
            skLineSegment(sketch, "E938", {"start": v(-27.7, -105.12) * mm, "end": v(-27.88, -105.3) * mm});
            skArc(sketch, "E939", {"start": v(-27.7, -105.12) * mm, "mid": v(-27.5, -104.36) * mm, "end": v(-28.06, -103.8) * mm});
            skArc(sketch, "E940", {"start": v(-28.06, -103.8) * mm, "mid": v(-27.9, -103) * mm, "end": v(-28.06, -102.2) * mm});
            skArc(sketch, "E941", {"start": v(-28.06, -102.2) * mm, "mid": v(-27.5, -101.64) * mm, "end": v(-27.7, -100.88) * mm});
            skArc(sketch, "E942", {"start": v(-7.37, -112) * mm, "mid": v(-7.22, -111.65) * mm, "end": v(-6.86, -111.5) * mm});
            skLineSegment(sketch, "E943", {"start": v(-6.86, -111.5) * mm, "end": v(-4.51, -111.5) * mm});
            skArc(sketch, "E944", {"start": v(-4, -111) * mm, "mid": v(-4.15, -111.35) * mm, "end": v(-4.51, -111.5) * mm});
            skLineSegment(sketch, "E945", {"start": v(-4, -110.27) * mm, "end": v(-4, -111) * mm});
            skArc(sketch, "E946", {"start": v(-4.15, -109.9) * mm, "mid": v(-4.04, -110.07) * mm, "end": v(-4, -110.27) * mm});
            skLineSegment(sketch, "E947", {"start": v(-4.15, -109.9) * mm, "end": v(-7.26, -106.8) * mm});
            skArc(sketch, "E948", {"start": v(-7.62, -106.66) * mm, "mid": v(-7.42, -106.7) * mm, "end": v(-7.26, -106.8) * mm});
            skLineSegment(sketch, "E949", {"start": v(-7.62, -106.65) * mm, "end": v(-12.38, -106.65) * mm});
            skArc(sketch, "E950", {"start": v(-12.74, -106.8) * mm, "mid": v(-12.58, -106.7) * mm, "end": v(-12.38, -106.66) * mm});
            skLineSegment(sketch, "E951", {"start": v(-12.74, -106.8) * mm, "end": v(-15.85, -109.9) * mm});
            skArc(sketch, "E952", {"start": v(-16, -110.27) * mm, "mid": v(-15.96, -110.07) * mm, "end": v(-15.85, -109.9) * mm});
            skLineSegment(sketch, "E953", {"start": v(-16, -110.27) * mm, "end": v(-16, -111) * mm});
            skArc(sketch, "E954", {"start": v(-15.49, -111.5) * mm, "mid": v(-15.85, -111.35) * mm, "end": v(-16, -111) * mm});
            skLineSegment(sketch, "E955", {"start": v(-15.49, -111.5) * mm, "end": v(-13.14, -111.5) * mm});
            skArc(sketch, "E956", {"start": v(-13.14, -111.5) * mm, "mid": v(-12.78, -111.65) * mm, "end": v(-12.63, -112) * mm});
            skLineSegment(sketch, "E957", {"start": v(-12.63, -112.5) * mm, "end": v(-12.63, -112) * mm});
            skArc(sketch, "E958", {"start": v(-12.63, -112.5) * mm, "mid": v(-12.78, -112.85) * mm, "end": v(-13.14, -113) * mm});
            skLineSegment(sketch, "E959", {"start": v(-26.86, -113) * mm, "end": v(-13.14, -113) * mm});
            skArc(sketch, "E960", {"start": v(-27.37, -112.5) * mm, "mid": v(-27.22, -112.85) * mm, "end": v(-26.86, -113) * mm});
            skLineSegment(sketch, "E961", {"start": v(-27.37, -112.5) * mm, "end": v(-27.37, -112) * mm});
            skArc(sketch, "E962", {"start": v(-26.86, -111.5) * mm, "mid": v(-27.22, -111.65) * mm, "end": v(-27.37, -112) * mm});
            skLineSegment(sketch, "E963", {"start": v(-24.51, -111.5) * mm, "end": v(-26.86, -111.5) * mm});
            skArc(sketch, "E964", {"start": v(-24.51, -111.5) * mm, "mid": v(-24.15, -111.35) * mm, "end": v(-24, -111) * mm});
            skLineSegment(sketch, "E965", {"start": v(-24, -110.27) * mm, "end": v(-24, -111) * mm});
            skArc(sketch, "E966", {"start": v(-24, -110.27) * mm, "mid": v(-24.04, -110.07) * mm, "end": v(-24.15, -109.9) * mm});
            skLineSegment(sketch, "E967", {"start": v(-27.26, -106.8) * mm, "end": v(-24.15, -109.9) * mm});
            skArc(sketch, "E968", {"start": v(-27.26, -106.8) * mm, "mid": v(-27.42, -106.7) * mm, "end": v(-27.62, -106.66) * mm});
            skLineSegment(sketch, "E969", {"start": v(-32.38, -106.65) * mm, "end": v(-27.62, -106.65) * mm});
            skArc(sketch, "E970", {"start": v(-32.38, -106.66) * mm, "mid": v(-32.58, -106.7) * mm, "end": v(-32.74, -106.8) * mm});
            skLineSegment(sketch, "E971", {"start": v(-35.85, -109.9) * mm, "end": v(-32.74, -106.8) * mm});
            skArc(sketch, "E972", {"start": v(-35.85, -109.9) * mm, "mid": v(-35.96, -110.07) * mm, "end": v(-36, -110.27) * mm});
            skLineSegment(sketch, "E973", {"start": v(-36, -110.27) * mm, "end": v(-36, -111) * mm});
            skArc(sketch, "E974", {"start": v(-36, -111) * mm, "mid": v(-35.85, -111.35) * mm, "end": v(-35.49, -111.5) * mm});
            skLineSegment(sketch, "E975", {"start": v(-33.14, -111.5) * mm, "end": v(-35.49, -111.5) * mm});
            skArc(sketch, "E976", {"start": v(-32.63, -112) * mm, "mid": v(-32.78, -111.65) * mm, "end": v(-33.14, -111.5) * mm});
            skLineSegment(sketch, "E977", {"start": v(-32.63, -112) * mm, "end": v(-32.63, -112.5) * mm});
            skArc(sketch, "E978", {"start": v(-33.14, -113) * mm, "mid": v(-32.78, -112.85) * mm, "end": v(-32.63, -112.5) * mm});
            skLineSegment(sketch, "E979", {"start": v(-38.5, -113) * mm, "end": v(-33.14, -113) * mm});
            skArc(sketch, "E980", {"start": v(-40, -111.5) * mm, "mid": v(-39.56, -112.56) * mm, "end": v(-38.5, -113) * mm});
            skLineSegment(sketch, "E981", {"start": v(-40, -111.5) * mm, "end": v(-40, -106.14) * mm});
            skArc(sketch, "E982", {"start": v(-39.5, -105.63) * mm, "mid": v(-39.85, -105.78) * mm, "end": v(-40, -106.14) * mm});
            skLineSegment(sketch, "E983", {"start": v(-39.5, -105.63) * mm, "end": v(-39, -105.63) * mm});
            skArc(sketch, "E984", {"start": v(-38.5, -106.14) * mm, "mid": v(-38.65, -105.78) * mm, "end": v(-39, -105.63) * mm});
            skLineSegment(sketch, "E985", {"start": v(-38.5, -108.49) * mm, "end": v(-38.5, -106.14) * mm});
            skArc(sketch, "E986", {"start": v(-38.5, -108.49) * mm, "mid": v(-38.35, -108.85) * mm, "end": v(-38, -109) * mm});
            skLineSegment(sketch, "E987", {"start": v(-37.27, -109) * mm, "end": v(-38, -109) * mm});
            skArc(sketch, "E988", {"start": v(-37.27, -109) * mm, "mid": v(-37.07, -108.96) * mm, "end": v(-36.9, -108.85) * mm});
            skLineSegment(sketch, "E989", {"start": v(-33.8, -105.74) * mm, "end": v(-36.9, -108.85) * mm});
            skArc(sketch, "E990", {"start": v(-33.8, -105.74) * mm, "mid": v(-33.7, -105.58) * mm, "end": v(-33.66, -105.38) * mm});
            skLineSegment(sketch, "E991", {"start": v(-33.66, -100.62) * mm, "end": v(-33.66, -105.38) * mm});
            skArc(sketch, "E992", {"start": v(-33.66, -100.62) * mm, "mid": v(-33.7, -100.42) * mm, "end": v(-33.8, -100.26) * mm});
            skLineSegment(sketch, "E993", {"start": v(-33.8, -100.26) * mm, "end": v(-36.9, -97.15) * mm});
            skArc(sketch, "E994", {"start": v(-36.9, -97.15) * mm, "mid": v(-37.07, -97.04) * mm, "end": v(-37.27, -97) * mm});
            skLineSegment(sketch, "E995", {"start": v(-37.27, -97) * mm, "end": v(-38, -97) * mm});
            skArc(sketch, "E996", {"start": v(-38, -97) * mm, "mid": v(-38.35, -97.15) * mm, "end": v(-38.5, -97.51) * mm});
            skLineSegment(sketch, "E997", {"start": v(-38.5, -97.51) * mm, "end": v(-38.5, -99.86) * mm});
            skArc(sketch, "E998", {"start": v(-39, -100.37) * mm, "mid": v(-38.65, -100.22) * mm, "end": v(-38.5, -99.86) * mm});
            skLineSegment(sketch, "E999", {"start": v(-39, -100.37) * mm, "end": v(-39.5, -100.37) * mm});
            skArc(sketch, "E1000", {"start": v(-40, -99.86) * mm, "mid": v(-39.85, -100.22) * mm, "end": v(-39.5, -100.37) * mm});
            skLineSegment(sketch, "E1001", {"start": v(-40, -99.86) * mm, "end": v(-40, -94.5) * mm});
            skArc(sketch, "E1002", {"start": v(-38.5, -93) * mm, "mid": v(-39.56, -93.44) * mm, "end": v(-40, -94.5) * mm});
            skLineSegment(sketch, "E1003", {"start": v(-38.5, -93) * mm, "end": v(-33.14, -93) * mm});
            skArc(sketch, "E1004", {"start": v(-32.63, -93.5) * mm, "mid": v(-32.78, -93.15) * mm, "end": v(-33.14, -93) * mm});
            skLineSegment(sketch, "E1005", {"start": v(-32.63, -93.5) * mm, "end": v(-32.63, -94) * mm});
            skArc(sketch, "E1006", {"start": v(-33.14, -94.5) * mm, "mid": v(-32.78, -94.35) * mm, "end": v(-32.63, -94) * mm});
            skLineSegment(sketch, "E1007", {"start": v(-33.14, -94.5) * mm, "end": v(-35.49, -94.5) * mm});
            skArc(sketch, "E1008", {"start": v(-35.49, -94.5) * mm, "mid": v(-35.85, -94.65) * mm, "end": v(-36, -95) * mm});
            skLineSegment(sketch, "E1009", {"start": v(-36, -95) * mm, "end": v(-36, -95.73) * mm});
            skArc(sketch, "E1010", {"start": v(-36, -95.73) * mm, "mid": v(-35.96, -95.93) * mm, "end": v(-35.85, -96.1) * mm});
            skLineSegment(sketch, "E1011", {"start": v(-35.85, -96.1) * mm, "end": v(-32.74, -99.2) * mm});
            skArc(sketch, "E1012", {"start": v(-32.74, -99.2) * mm, "mid": v(-32.58, -99.3) * mm, "end": v(-32.38, -99.34) * mm});
            skLineSegment(sketch, "E1013", {"start": v(-32.38, -99.34) * mm, "end": v(-27.62, -99.34) * mm});
            skArc(sketch, "E1014", {"start": v(-27.62, -99.34) * mm, "mid": v(-27.42, -99.3) * mm, "end": v(-27.26, -99.2) * mm});
            skLineSegment(sketch, "E1015", {"start": v(-27.26, -99.2) * mm, "end": v(-24.15, -96.1) * mm});
            skArc(sketch, "E1016", {"start": v(-24.15, -96.1) * mm, "mid": v(-24.04, -95.93) * mm, "end": v(-24, -95.73) * mm});
            skLineSegment(sketch, "E1017", {"start": v(-24, -95) * mm, "end": v(-24, -95.73) * mm});
            skArc(sketch, "E1018", {"start": v(-24, -95) * mm, "mid": v(-24.15, -94.65) * mm, "end": v(-24.51, -94.5) * mm});
            skLineSegment(sketch, "E1019", {"start": v(-24.51, -94.5) * mm, "end": v(-26.86, -94.5) * mm});
            skArc(sketch, "E1020", {"start": v(-27.37, -94) * mm, "mid": v(-27.22, -94.35) * mm, "end": v(-26.86, -94.5) * mm});
            skLineSegment(sketch, "E1021", {"start": v(-27.37, -94) * mm, "end": v(-27.37, -93.5) * mm});
            skArc(sketch, "E1022", {"start": v(-26.86, -93) * mm, "mid": v(-27.22, -93.15) * mm, "end": v(-27.37, -93.5) * mm});
            skLineSegment(sketch, "E1023", {"start": v(-13.14, -93) * mm, "end": v(-26.86, -93) * mm});
            skArc(sketch, "E1024", {"start": v(-13.14, -93) * mm, "mid": v(-12.78, -93.15) * mm, "end": v(-12.63, -93.5) * mm});
            skLineSegment(sketch, "E1025", {"start": v(-12.63, -94) * mm, "end": v(-12.63, -93.5) * mm});
            skArc(sketch, "E1026", {"start": v(-12.63, -94) * mm, "mid": v(-12.78, -94.35) * mm, "end": v(-13.14, -94.5) * mm});
            skLineSegment(sketch, "E1027", {"start": v(-15.49, -94.5) * mm, "end": v(-13.14, -94.5) * mm});
            skArc(sketch, "E1028", {"start": v(-16, -95) * mm, "mid": v(-15.85, -94.65) * mm, "end": v(-15.49, -94.5) * mm});
            skLineSegment(sketch, "E1029", {"start": v(-16, -95) * mm, "end": v(-16, -95.73) * mm});
            skArc(sketch, "E1030", {"start": v(-15.85, -96.1) * mm, "mid": v(-15.96, -95.93) * mm, "end": v(-16, -95.73) * mm});
            skLineSegment(sketch, "E1031", {"start": v(-12.74, -99.2) * mm, "end": v(-15.85, -96.1) * mm});
            skArc(sketch, "E1032", {"start": v(-12.38, -99.34) * mm, "mid": v(-12.58, -99.3) * mm, "end": v(-12.74, -99.2) * mm});
            skLineSegment(sketch, "E1033", {"start": v(-7.62, -99.34) * mm, "end": v(-12.38, -99.34) * mm});
            skArc(sketch, "E1034", {"start": v(-7.26, -99.2) * mm, "mid": v(-7.42, -99.3) * mm, "end": v(-7.62, -99.34) * mm});
            skLineSegment(sketch, "E1035", {"start": v(-4.15, -96.1) * mm, "end": v(-7.26, -99.2) * mm});
            skArc(sketch, "E1036", {"start": v(-4, -95.73) * mm, "mid": v(-4.04, -95.93) * mm, "end": v(-4.15, -96.1) * mm});
            skLineSegment(sketch, "E1037", {"start": v(-4, -95) * mm, "end": v(-4, -95.73) * mm});
            skArc(sketch, "E1038", {"start": v(-4.51, -94.5) * mm, "mid": v(-4.15, -94.65) * mm, "end": v(-4, -95) * mm});
            skLineSegment(sketch, "E1039", {"start": v(-6.86, -94.5) * mm, "end": v(-4.51, -94.5) * mm});
            skArc(sketch, "E1040", {"start": v(-6.86, -94.5) * mm, "mid": v(-7.22, -94.35) * mm, "end": v(-7.37, -94) * mm});
            skLineSegment(sketch, "E1041", {"start": v(-7.37, -93.5) * mm, "end": v(-7.37, -94) * mm});
            skArc(sketch, "E1042", {"start": v(-7.37, -93.5) * mm, "mid": v(-7.22, -93.15) * mm, "end": v(-6.86, -93) * mm});
            skLineSegment(sketch, "E1043", {"start": v(1.5, -93) * mm, "end": v(-6.86, -93) * mm});
            skArc(sketch, "E1044", {"start": v(-1, -100.37) * mm, "mid": v(-1.35, -100.22) * mm, "end": v(-1.5, -99.86) * mm});
            skLineSegment(sketch, "E1045", {"start": v(-1.5, -97.51) * mm, "end": v(-1.5, -99.86) * mm});
            skArc(sketch, "E1046", {"start": v(-2, -97) * mm, "mid": v(-1.65, -97.15) * mm, "end": v(-1.5, -97.51) * mm});
            skLineSegment(sketch, "E1047", {"start": v(-2.73, -97) * mm, "end": v(-2, -97) * mm});
            skArc(sketch, "E1048", {"start": v(-3.1, -97.15) * mm, "mid": v(-2.93, -97.04) * mm, "end": v(-2.73, -97) * mm});
            skLineSegment(sketch, "E1049", {"start": v(-6.2, -100.26) * mm, "end": v(-3.1, -97.15) * mm});
            skArc(sketch, "E1050", {"start": v(-6.35, -100.62) * mm, "mid": v(-6.3, -100.42) * mm, "end": v(-6.2, -100.26) * mm});
            skLineSegment(sketch, "E1051", {"start": v(-6.35, -100.62) * mm, "end": v(-6.35, -105.38) * mm});
            skArc(sketch, "E1052", {"start": v(-6.2, -105.74) * mm, "mid": v(-6.3, -105.58) * mm, "end": v(-6.35, -105.38) * mm});
            skLineSegment(sketch, "E1053", {"start": v(-6.2, -105.74) * mm, "end": v(-3.1, -108.85) * mm});
            skArc(sketch, "E1054", {"start": v(-2.73, -109) * mm, "mid": v(-2.93, -108.96) * mm, "end": v(-3.1, -108.85) * mm});
            skLineSegment(sketch, "E1055", {"start": v(-2.73, -109) * mm, "end": v(-2, -109) * mm});
            skArc(sketch, "E1056", {"start": v(-1.5, -108.49) * mm, "mid": v(-1.65, -108.85) * mm, "end": v(-2, -109) * mm});
            skLineSegment(sketch, "E1057", {"start": v(-1.5, -108.49) * mm, "end": v(-1.5, -106.14) * mm});
            skArc(sketch, "E1058", {"start": v(-1.5, -106.14) * mm, "mid": v(-1.35, -105.78) * mm, "end": v(-1, -105.63) * mm});
            skLineSegment(sketch, "E1059", {"start": v(-0.5, -105.63) * mm, "end": v(-1, -105.63) * mm});
            skLineSegment(sketch, "E1060", {"start": v(-1.5, -113) * mm, "end": v(-6.86, -113) * mm});
            skArc(sketch, "E1061", {"start": v(-6.86, -113) * mm, "mid": v(-7.22, -112.85) * mm, "end": v(-7.37, -112.5) * mm});
            skArc(sketch, "E1062", {"start": v(-13.66, -100.62) * mm, "mid": v(-13.7, -100.42) * mm, "end": v(-13.8, -100.26) * mm});
            skLineSegment(sketch, "E1063", {"start": v(-13.8, -100.26) * mm, "end": v(-17.35, -96.71) * mm});
            skArc(sketch, "E1064", {"start": v(-17.35, -96.71) * mm, "mid": v(-17.46, -96.55) * mm, "end": v(-17.5, -96.36) * mm});
            skLineSegment(sketch, "E1065", {"start": v(-17.5, -95) * mm, "end": v(-17.5, -96.36) * mm});
            skArc(sketch, "E1066", {"start": v(-18, -94.5) * mm, "mid": v(-17.64, -94.65) * mm, "end": v(-17.5, -95) * mm});
            skLineSegment(sketch, "E1067", {"start": v(-22, -94.5) * mm, "end": v(-18, -94.5) * mm});
            skArc(sketch, "E1068", {"start": v(-22, -94.5) * mm, "mid": v(-22.36, -94.65) * mm, "end": v(-22.5, -95) * mm});
            skLineSegment(sketch, "E1069", {"start": v(-22.5, -95) * mm, "end": v(-22.5, -96.36) * mm});
            skArc(sketch, "E1070", {"start": v(-22.65, -96.71) * mm, "mid": v(-22.54, -96.55) * mm, "end": v(-22.5, -96.36) * mm});
            skLineSegment(sketch, "E1071", {"start": v(-26.2, -100.26) * mm, "end": v(-22.65, -96.71) * mm});
            skArc(sketch, "E1072", {"start": v(-26.2, -100.26) * mm, "mid": v(-26.3, -100.42) * mm, "end": v(-26.35, -100.62) * mm});
            skLineSegment(sketch, "E1073", {"start": v(-26.35, -100.62) * mm, "end": v(-26.35, -105.38) * mm});
            skArc(sketch, "E1074", {"start": v(-26.35, -105.38) * mm, "mid": v(-26.3, -105.58) * mm, "end": v(-26.2, -105.74) * mm});
            skLineSegment(sketch, "E1075", {"start": v(-26.2, -105.74) * mm, "end": v(-22.65, -109.29) * mm});
            skArc(sketch, "E1076", {"start": v(-22.5, -109.64) * mm, "mid": v(-22.54, -109.45) * mm, "end": v(-22.65, -109.29) * mm});
            skLineSegment(sketch, "E1077", {"start": v(-22.5, -109.64) * mm, "end": v(-22.5, -111) * mm});
            skArc(sketch, "E1078", {"start": v(-22.5, -111) * mm, "mid": v(-22.36, -111.35) * mm, "end": v(-22, -111.5) * mm});
            skLineSegment(sketch, "E1079", {"start": v(-22, -111.5) * mm, "end": v(-18, -111.5) * mm});
            skArc(sketch, "E1080", {"start": v(-17.5, -111) * mm, "mid": v(-17.64, -111.35) * mm, "end": v(-18, -111.5) * mm});
            skLineSegment(sketch, "E1081", {"start": v(-17.5, -109.64) * mm, "end": v(-17.5, -111) * mm});
            skArc(sketch, "E1082", {"start": v(-17.5, -109.64) * mm, "mid": v(-17.46, -109.45) * mm, "end": v(-17.35, -109.29) * mm});
            skLineSegment(sketch, "E1083", {"start": v(-13.8, -105.74) * mm, "end": v(-17.35, -109.29) * mm});
            skArc(sketch, "E1084", {"start": v(-13.66, -105.38) * mm, "mid": v(-13.7, -105.58) * mm, "end": v(-13.8, -105.74) * mm});
            skLineSegment(sketch, "E1085", {"start": v(13.66, -100.62) * mm, "end": v(13.66, -105.38) * mm});
            skArc(sketch, "E1086", {"start": v(7.88, -100.7) * mm, "mid": v(8.64, -100.5) * mm, "end": v(9.2, -101.06) * mm});
            skLineSegment(sketch, "E1087", {"start": v(27.88, -100.7) * mm, "end": v(27.7, -100.88) * mm});
            skLineSegment(sketch, "E1088", {"start": v(7.37, -112) * mm, "end": v(7.37, -112.5) * mm});
            skArc(sketch, "E1089", {"start": v(9.2, -101.06) * mm, "mid": v(10, -100.9) * mm, "end": v(10.8, -101.06) * mm});
            skArc(sketch, "E1090", {"start": v(10.8, -101.06) * mm, "mid": v(11.36, -100.5) * mm, "end": v(12.12, -100.7) * mm});
            skLineSegment(sketch, "E1091", {"start": v(12.12, -100.7) * mm, "end": v(12.3, -100.88) * mm});
            skArc(sketch, "E1092", {"start": v(12.3, -100.88) * mm, "mid": v(12.5, -101.64) * mm, "end": v(11.94, -102.2) * mm});
            skArc(sketch, "E1093", {"start": v(11.94, -102.2) * mm, "mid": v(12.1, -103) * mm, "end": v(11.94, -103.8) * mm});
            skArc(sketch, "E1094", {"start": v(11.94, -103.8) * mm, "mid": v(12.5, -104.36) * mm, "end": v(12.3, -105.12) * mm});
            skLineSegment(sketch, "E1095", {"start": v(12.3, -105.12) * mm, "end": v(12.12, -105.3) * mm});
            skArc(sketch, "E1096", {"start": v(12.12, -105.3) * mm, "mid": v(11.36, -105.5) * mm, "end": v(10.8, -104.94) * mm});
            skArc(sketch, "E1097", {"start": v(10.8, -104.94) * mm, "mid": v(10, -105.1) * mm, "end": v(9.2, -104.94) * mm});
            skArc(sketch, "E1098", {"start": v(9.2, -104.94) * mm, "mid": v(8.64, -105.5) * mm, "end": v(7.88, -105.3) * mm});
            skLineSegment(sketch, "E1099", {"start": v(7.88, -105.3) * mm, "end": v(7.7, -105.12) * mm});
            skArc(sketch, "E1100", {"start": v(7.7, -105.12) * mm, "mid": v(7.5, -104.36) * mm, "end": v(8.06, -103.8) * mm});
            skArc(sketch, "E1101", {"start": v(8.06, -103.8) * mm, "mid": v(7.9, -103) * mm, "end": v(8.06, -102.2) * mm});
            skArc(sketch, "E1102", {"start": v(8.06, -102.2) * mm, "mid": v(7.5, -101.64) * mm, "end": v(7.7, -100.88) * mm});
            skLineSegment(sketch, "E1103", {"start": v(7.7, -100.88) * mm, "end": v(7.88, -100.7) * mm});
            skArc(sketch, "E1104", {"start": v(29.2, -101.06) * mm, "mid": v(28.64, -100.5) * mm, "end": v(27.88, -100.7) * mm});
            skArc(sketch, "E1105", {"start": v(30.8, -101.06) * mm, "mid": v(30, -100.9) * mm, "end": v(29.2, -101.06) * mm});
            skArc(sketch, "E1106", {"start": v(32.12, -100.7) * mm, "mid": v(31.36, -100.5) * mm, "end": v(30.8, -101.06) * mm});
            skLineSegment(sketch, "E1107", {"start": v(32.3, -100.88) * mm, "end": v(32.12, -100.7) * mm});
            skArc(sketch, "E1108", {"start": v(31.94, -102.2) * mm, "mid": v(32.5, -101.64) * mm, "end": v(32.3, -100.88) * mm});
            skArc(sketch, "E1109", {"start": v(31.94, -103.8) * mm, "mid": v(32.1, -103) * mm, "end": v(31.94, -102.2) * mm});
            skArc(sketch, "E1110", {"start": v(32.3, -105.12) * mm, "mid": v(32.5, -104.36) * mm, "end": v(31.94, -103.8) * mm});
            skLineSegment(sketch, "E1111", {"start": v(32.12, -105.3) * mm, "end": v(32.3, -105.12) * mm});
            skArc(sketch, "E1112", {"start": v(30.8, -104.94) * mm, "mid": v(31.36, -105.5) * mm, "end": v(32.12, -105.3) * mm});
            skArc(sketch, "E1113", {"start": v(29.2, -104.94) * mm, "mid": v(30, -105.1) * mm, "end": v(30.8, -104.94) * mm});
            skArc(sketch, "E1114", {"start": v(27.88, -105.3) * mm, "mid": v(28.64, -105.5) * mm, "end": v(29.2, -104.94) * mm});
            skLineSegment(sketch, "E1115", {"start": v(27.7, -105.12) * mm, "end": v(27.88, -105.3) * mm});
            skArc(sketch, "E1116", {"start": v(28.06, -103.8) * mm, "mid": v(27.5, -104.36) * mm, "end": v(27.7, -105.12) * mm});
            skArc(sketch, "E1117", {"start": v(28.06, -102.2) * mm, "mid": v(27.9, -103) * mm, "end": v(28.06, -103.8) * mm});
            skArc(sketch, "E1118", {"start": v(27.7, -100.88) * mm, "mid": v(27.5, -101.64) * mm, "end": v(28.06, -102.2) * mm});
            skArc(sketch, "E1119", {"start": v(6.86, -111.5) * mm, "mid": v(7.22, -111.65) * mm, "end": v(7.37, -112) * mm});
            skLineSegment(sketch, "E1120", {"start": v(6.86, -111.5) * mm, "end": v(4.51, -111.5) * mm});
            skArc(sketch, "E1121", {"start": v(4.51, -111.5) * mm, "mid": v(4.15, -111.35) * mm, "end": v(4, -111) * mm});
            skLineSegment(sketch, "E1122", {"start": v(4, -110.27) * mm, "end": v(4, -111) * mm});
            skArc(sketch, "E1123", {"start": v(4, -110.27) * mm, "mid": v(4.04, -110.07) * mm, "end": v(4.15, -109.9) * mm});
            skLineSegment(sketch, "E1124", {"start": v(4.15, -109.9) * mm, "end": v(7.26, -106.8) * mm});
            skArc(sketch, "E1125", {"start": v(7.26, -106.8) * mm, "mid": v(7.42, -106.7) * mm, "end": v(7.62, -106.66) * mm});
            skLineSegment(sketch, "E1126", {"start": v(7.62, -106.65) * mm, "end": v(12.38, -106.65) * mm});
            skArc(sketch, "E1127", {"start": v(12.38, -106.66) * mm, "mid": v(12.58, -106.7) * mm, "end": v(12.74, -106.8) * mm});
            skLineSegment(sketch, "E1128", {"start": v(12.74, -106.8) * mm, "end": v(15.85, -109.9) * mm});
            skArc(sketch, "E1129", {"start": v(15.85, -109.9) * mm, "mid": v(15.96, -110.07) * mm, "end": v(16, -110.27) * mm});
            skLineSegment(sketch, "E1130", {"start": v(16, -110.27) * mm, "end": v(16, -111) * mm});
            skArc(sketch, "E1131", {"start": v(16, -111) * mm, "mid": v(15.85, -111.35) * mm, "end": v(15.49, -111.5) * mm});
            skLineSegment(sketch, "E1132", {"start": v(15.49, -111.5) * mm, "end": v(13.14, -111.5) * mm});
            skArc(sketch, "E1133", {"start": v(12.63, -112) * mm, "mid": v(12.78, -111.65) * mm, "end": v(13.14, -111.5) * mm});
            skLineSegment(sketch, "E1134", {"start": v(12.63, -112.5) * mm, "end": v(12.63, -112) * mm});
            skArc(sketch, "E1135", {"start": v(13.14, -113) * mm, "mid": v(12.78, -112.85) * mm, "end": v(12.63, -112.5) * mm});
            skLineSegment(sketch, "E1136", {"start": v(26.86, -113) * mm, "end": v(13.14, -113) * mm});
            skArc(sketch, "E1137", {"start": v(26.86, -113) * mm, "mid": v(27.22, -112.85) * mm, "end": v(27.37, -112.5) * mm});
            skLineSegment(sketch, "E1138", {"start": v(27.37, -112.5) * mm, "end": v(27.37, -112) * mm});
            skArc(sketch, "E1139", {"start": v(27.37, -112) * mm, "mid": v(27.22, -111.65) * mm, "end": v(26.86, -111.5) * mm});
            skLineSegment(sketch, "E1140", {"start": v(24.51, -111.5) * mm, "end": v(26.86, -111.5) * mm});
            skArc(sketch, "E1141", {"start": v(24, -111) * mm, "mid": v(24.15, -111.35) * mm, "end": v(24.51, -111.5) * mm});
            skLineSegment(sketch, "E1142", {"start": v(24, -110.27) * mm, "end": v(24, -111) * mm});
            skArc(sketch, "E1143", {"start": v(24.15, -109.9) * mm, "mid": v(24.04, -110.07) * mm, "end": v(24, -110.27) * mm});
            skLineSegment(sketch, "E1144", {"start": v(27.26, -106.8) * mm, "end": v(24.15, -109.9) * mm});
            skArc(sketch, "E1145", {"start": v(27.62, -106.66) * mm, "mid": v(27.42, -106.7) * mm, "end": v(27.26, -106.8) * mm});
            skLineSegment(sketch, "E1146", {"start": v(32.38, -106.65) * mm, "end": v(27.62, -106.65) * mm});
            skArc(sketch, "E1147", {"start": v(32.74, -106.8) * mm, "mid": v(32.58, -106.7) * mm, "end": v(32.38, -106.66) * mm});
            skLineSegment(sketch, "E1148", {"start": v(35.85, -109.9) * mm, "end": v(32.74, -106.8) * mm});
            skArc(sketch, "E1149", {"start": v(36, -110.27) * mm, "mid": v(35.96, -110.07) * mm, "end": v(35.85, -109.9) * mm});
            skLineSegment(sketch, "E1150", {"start": v(36, -110.27) * mm, "end": v(36, -111) * mm});
            skArc(sketch, "E1151", {"start": v(35.49, -111.5) * mm, "mid": v(35.85, -111.35) * mm, "end": v(36, -111) * mm});
            skLineSegment(sketch, "E1152", {"start": v(33.14, -111.5) * mm, "end": v(35.49, -111.5) * mm});
            skArc(sketch, "E1153", {"start": v(33.14, -111.5) * mm, "mid": v(32.78, -111.65) * mm, "end": v(32.63, -112) * mm});
            skLineSegment(sketch, "E1154", {"start": v(32.63, -112) * mm, "end": v(32.63, -112.5) * mm});
            skArc(sketch, "E1155", {"start": v(32.63, -112.5) * mm, "mid": v(32.78, -112.85) * mm, "end": v(33.14, -113) * mm});
            skLineSegment(sketch, "E1156", {"start": v(38.5, -113) * mm, "end": v(33.14, -113) * mm});
            skArc(sketch, "E1157", {"start": v(38.5, -113) * mm, "mid": v(39.56, -112.56) * mm, "end": v(40, -111.5) * mm});
            skLineSegment(sketch, "E1158", {"start": v(40, -111.5) * mm, "end": v(40, -106.14) * mm});
            skArc(sketch, "E1159", {"start": v(40, -106.14) * mm, "mid": v(39.85, -105.78) * mm, "end": v(39.5, -105.63) * mm});
            skLineSegment(sketch, "E1160", {"start": v(39.5, -105.63) * mm, "end": v(39, -105.63) * mm});
            skArc(sketch, "E1161", {"start": v(39, -105.63) * mm, "mid": v(38.65, -105.78) * mm, "end": v(38.5, -106.14) * mm});
            skLineSegment(sketch, "E1162", {"start": v(38.5, -108.49) * mm, "end": v(38.5, -106.14) * mm});
            skArc(sketch, "E1163", {"start": v(38, -109) * mm, "mid": v(38.35, -108.85) * mm, "end": v(38.5, -108.49) * mm});
            skLineSegment(sketch, "E1164", {"start": v(37.27, -109) * mm, "end": v(38, -109) * mm});
            skArc(sketch, "E1165", {"start": v(36.9, -108.85) * mm, "mid": v(37.07, -108.96) * mm, "end": v(37.27, -109) * mm});
            skLineSegment(sketch, "E1166", {"start": v(33.8, -105.74) * mm, "end": v(36.9, -108.85) * mm});
            skArc(sketch, "E1167", {"start": v(33.66, -105.38) * mm, "mid": v(33.7, -105.58) * mm, "end": v(33.8, -105.74) * mm});
            skLineSegment(sketch, "E1168", {"start": v(33.66, -100.62) * mm, "end": v(33.66, -105.38) * mm});
            skArc(sketch, "E1169", {"start": v(33.8, -100.26) * mm, "mid": v(33.7, -100.42) * mm, "end": v(33.66, -100.62) * mm});
            skLineSegment(sketch, "E1170", {"start": v(33.8, -100.26) * mm, "end": v(36.9, -97.15) * mm});
            skArc(sketch, "E1171", {"start": v(37.27, -97) * mm, "mid": v(37.07, -97.04) * mm, "end": v(36.9, -97.15) * mm});
            skLineSegment(sketch, "E1172", {"start": v(37.27, -97) * mm, "end": v(38, -97) * mm});
            skArc(sketch, "E1173", {"start": v(38.5, -97.51) * mm, "mid": v(38.35, -97.15) * mm, "end": v(38, -97) * mm});
            skLineSegment(sketch, "E1174", {"start": v(38.5, -97.51) * mm, "end": v(38.5, -99.86) * mm});
            skArc(sketch, "E1175", {"start": v(38.5, -99.86) * mm, "mid": v(38.65, -100.22) * mm, "end": v(39, -100.37) * mm});
            skLineSegment(sketch, "E1176", {"start": v(39, -100.37) * mm, "end": v(39.5, -100.37) * mm});
            skArc(sketch, "E1177", {"start": v(39.5, -100.37) * mm, "mid": v(39.85, -100.22) * mm, "end": v(40, -99.86) * mm});
            skLineSegment(sketch, "E1178", {"start": v(40, -99.86) * mm, "end": v(40, -94.5) * mm});
            skArc(sketch, "E1179", {"start": v(40, -94.5) * mm, "mid": v(39.56, -93.44) * mm, "end": v(38.5, -93) * mm});
            skLineSegment(sketch, "E1180", {"start": v(38.5, -93) * mm, "end": v(33.14, -93) * mm});
            skArc(sketch, "E1181", {"start": v(33.14, -93) * mm, "mid": v(32.78, -93.15) * mm, "end": v(32.63, -93.5) * mm});
            skLineSegment(sketch, "E1182", {"start": v(32.63, -93.5) * mm, "end": v(32.63, -94) * mm});
            skArc(sketch, "E1183", {"start": v(32.63, -94) * mm, "mid": v(32.78, -94.35) * mm, "end": v(33.14, -94.5) * mm});
            skLineSegment(sketch, "E1184", {"start": v(33.14, -94.5) * mm, "end": v(35.49, -94.5) * mm});
            skArc(sketch, "E1185", {"start": v(36, -95) * mm, "mid": v(35.85, -94.65) * mm, "end": v(35.49, -94.5) * mm});
            skLineSegment(sketch, "E1186", {"start": v(36, -95) * mm, "end": v(36, -95.73) * mm});
            skArc(sketch, "E1187", {"start": v(35.85, -96.1) * mm, "mid": v(35.96, -95.93) * mm, "end": v(36, -95.73) * mm});
            skLineSegment(sketch, "E1188", {"start": v(35.85, -96.1) * mm, "end": v(32.74, -99.2) * mm});
            skArc(sketch, "E1189", {"start": v(32.38, -99.34) * mm, "mid": v(32.58, -99.3) * mm, "end": v(32.74, -99.2) * mm});
            skLineSegment(sketch, "E1190", {"start": v(32.38, -99.34) * mm, "end": v(27.62, -99.34) * mm});
            skArc(sketch, "E1191", {"start": v(27.26, -99.2) * mm, "mid": v(27.42, -99.3) * mm, "end": v(27.62, -99.34) * mm});
            skLineSegment(sketch, "E1192", {"start": v(27.26, -99.2) * mm, "end": v(24.15, -96.1) * mm});
            skArc(sketch, "E1193", {"start": v(24, -95.73) * mm, "mid": v(24.04, -95.93) * mm, "end": v(24.15, -96.1) * mm});
            skLineSegment(sketch, "E1194", {"start": v(24, -95) * mm, "end": v(24, -95.73) * mm});
            skArc(sketch, "E1195", {"start": v(24.51, -94.5) * mm, "mid": v(24.15, -94.65) * mm, "end": v(24, -95) * mm});
            skLineSegment(sketch, "E1196", {"start": v(24.51, -94.5) * mm, "end": v(26.86, -94.5) * mm});
            skArc(sketch, "E1197", {"start": v(26.86, -94.5) * mm, "mid": v(27.22, -94.35) * mm, "end": v(27.37, -94) * mm});
            skLineSegment(sketch, "E1198", {"start": v(27.37, -94) * mm, "end": v(27.37, -93.5) * mm});
            skArc(sketch, "E1199", {"start": v(27.37, -93.5) * mm, "mid": v(27.22, -93.15) * mm, "end": v(26.86, -93) * mm});
            skLineSegment(sketch, "E1200", {"start": v(13.14, -93) * mm, "end": v(26.86, -93) * mm});
            skArc(sketch, "E1201", {"start": v(12.63, -93.5) * mm, "mid": v(12.78, -93.15) * mm, "end": v(13.14, -93) * mm});
            skLineSegment(sketch, "E1202", {"start": v(12.63, -94) * mm, "end": v(12.63, -93.5) * mm});
            skArc(sketch, "E1203", {"start": v(13.14, -94.5) * mm, "mid": v(12.78, -94.35) * mm, "end": v(12.63, -94) * mm});
            skLineSegment(sketch, "E1204", {"start": v(15.49, -94.5) * mm, "end": v(13.14, -94.5) * mm});
            skArc(sketch, "E1205", {"start": v(15.49, -94.5) * mm, "mid": v(15.85, -94.65) * mm, "end": v(16, -95) * mm});
            skLineSegment(sketch, "E1206", {"start": v(16, -95) * mm, "end": v(16, -95.73) * mm});
            skArc(sketch, "E1207", {"start": v(16, -95.73) * mm, "mid": v(15.96, -95.93) * mm, "end": v(15.85, -96.1) * mm});
            skLineSegment(sketch, "E1208", {"start": v(12.74, -99.2) * mm, "end": v(15.85, -96.1) * mm});
            skArc(sketch, "E1209", {"start": v(12.74, -99.2) * mm, "mid": v(12.58, -99.3) * mm, "end": v(12.38, -99.34) * mm});
            skLineSegment(sketch, "E1210", {"start": v(7.62, -99.34) * mm, "end": v(12.38, -99.34) * mm});
            skArc(sketch, "E1211", {"start": v(7.62, -99.34) * mm, "mid": v(7.42, -99.3) * mm, "end": v(7.26, -99.2) * mm});
            skLineSegment(sketch, "E1212", {"start": v(4.15, -96.1) * mm, "end": v(7.26, -99.2) * mm});
            skArc(sketch, "E1213", {"start": v(4.15, -96.1) * mm, "mid": v(4.04, -95.93) * mm, "end": v(4, -95.73) * mm});
            skLineSegment(sketch, "E1214", {"start": v(4, -95) * mm, "end": v(4, -95.73) * mm});
            skArc(sketch, "E1215", {"start": v(4, -95) * mm, "mid": v(4.15, -94.65) * mm, "end": v(4.51, -94.5) * mm});
            skLineSegment(sketch, "E1216", {"start": v(6.86, -94.5) * mm, "end": v(4.51, -94.5) * mm});
            skArc(sketch, "E1217", {"start": v(7.37, -94) * mm, "mid": v(7.22, -94.35) * mm, "end": v(6.86, -94.5) * mm});
            skLineSegment(sketch, "E1218", {"start": v(7.37, -93.5) * mm, "end": v(7.37, -94) * mm});
            skArc(sketch, "E1219", {"start": v(6.86, -93) * mm, "mid": v(7.22, -93.15) * mm, "end": v(7.37, -93.5) * mm});
            skLineSegment(sketch, "E1220", {"start": v(1.5, -93) * mm, "end": v(6.86, -93) * mm});
            skArc(sketch, "E1221", {"start": v(1.5, -99.86) * mm, "mid": v(1.35, -100.22) * mm, "end": v(1, -100.37) * mm});
            skLineSegment(sketch, "E1222", {"start": v(1.5, -97.51) * mm, "end": v(1.5, -99.86) * mm});
            skArc(sketch, "E1223", {"start": v(1.5, -97.51) * mm, "mid": v(1.65, -97.15) * mm, "end": v(2, -97) * mm});
            skLineSegment(sketch, "E1224", {"start": v(2.73, -97) * mm, "end": v(2, -97) * mm});
            skArc(sketch, "E1225", {"start": v(2.73, -97) * mm, "mid": v(2.93, -97.04) * mm, "end": v(3.1, -97.15) * mm});
            skLineSegment(sketch, "E1226", {"start": v(6.2, -100.26) * mm, "end": v(3.1, -97.15) * mm});
            skArc(sketch, "E1227", {"start": v(6.2, -100.26) * mm, "mid": v(6.3, -100.42) * mm, "end": v(6.34, -100.62) * mm});
            skLineSegment(sketch, "E1228", {"start": v(6.34, -100.62) * mm, "end": v(6.34, -105.38) * mm});
            skArc(sketch, "E1229", {"start": v(6.34, -105.38) * mm, "mid": v(6.3, -105.58) * mm, "end": v(6.2, -105.74) * mm});
            skLineSegment(sketch, "E1230", {"start": v(6.2, -105.74) * mm, "end": v(3.1, -108.85) * mm});
            skArc(sketch, "E1231", {"start": v(3.1, -108.85) * mm, "mid": v(2.93, -108.96) * mm, "end": v(2.73, -109) * mm});
            skLineSegment(sketch, "E1232", {"start": v(2.73, -109) * mm, "end": v(2, -109) * mm});
            skArc(sketch, "E1233", {"start": v(2, -109) * mm, "mid": v(1.65, -108.85) * mm, "end": v(1.5, -108.49) * mm});
            skLineSegment(sketch, "E1234", {"start": v(1.5, -108.49) * mm, "end": v(1.5, -106.14) * mm});
            skArc(sketch, "E1235", {"start": v(1, -105.63) * mm, "mid": v(1.35, -105.78) * mm, "end": v(1.5, -106.14) * mm});
            skLineSegment(sketch, "E1236", {"start": v(0.5, -105.63) * mm, "end": v(1, -105.63) * mm});
            skLineSegment(sketch, "E1237", {"start": v(-1.5, -113) * mm, "end": v(6.86, -113) * mm});
            skArc(sketch, "E1238", {"start": v(7.37, -112.5) * mm, "mid": v(7.22, -112.85) * mm, "end": v(6.86, -113) * mm});
            skArc(sketch, "E1239", {"start": v(13.8, -100.26) * mm, "mid": v(13.7, -100.42) * mm, "end": v(13.66, -100.62) * mm});
            skLineSegment(sketch, "E1240", {"start": v(13.8, -100.26) * mm, "end": v(17.35, -96.71) * mm});
            skArc(sketch, "E1241", {"start": v(17.5, -96.36) * mm, "mid": v(17.46, -96.55) * mm, "end": v(17.35, -96.71) * mm});
            skLineSegment(sketch, "E1242", {"start": v(17.5, -95) * mm, "end": v(17.5, -96.36) * mm});
            skArc(sketch, "E1243", {"start": v(17.5, -95) * mm, "mid": v(17.64, -94.65) * mm, "end": v(18, -94.5) * mm});
            skLineSegment(sketch, "E1244", {"start": v(22, -94.5) * mm, "end": v(18, -94.5) * mm});
            skArc(sketch, "E1245", {"start": v(22.5, -95) * mm, "mid": v(22.36, -94.65) * mm, "end": v(22, -94.5) * mm});
            skLineSegment(sketch, "E1246", {"start": v(22.5, -95) * mm, "end": v(22.5, -96.36) * mm});
            skArc(sketch, "E1247", {"start": v(22.5, -96.36) * mm, "mid": v(22.54, -96.55) * mm, "end": v(22.65, -96.71) * mm});
            skLineSegment(sketch, "E1248", {"start": v(26.2, -100.26) * mm, "end": v(22.65, -96.71) * mm});
            skArc(sketch, "E1249", {"start": v(26.34, -100.62) * mm, "mid": v(26.3, -100.42) * mm, "end": v(26.2, -100.26) * mm});
            skLineSegment(sketch, "E1250", {"start": v(26.35, -100.62) * mm, "end": v(26.35, -105.38) * mm});
            skArc(sketch, "E1251", {"start": v(26.2, -105.74) * mm, "mid": v(26.3, -105.58) * mm, "end": v(26.34, -105.38) * mm});
            skLineSegment(sketch, "E1252", {"start": v(26.2, -105.74) * mm, "end": v(22.65, -109.29) * mm});
            skArc(sketch, "E1253", {"start": v(22.65, -109.29) * mm, "mid": v(22.54, -109.45) * mm, "end": v(22.5, -109.64) * mm});
            skLineSegment(sketch, "E1254", {"start": v(22.5, -109.64) * mm, "end": v(22.5, -111) * mm});
            skArc(sketch, "E1255", {"start": v(22, -111.5) * mm, "mid": v(22.36, -111.35) * mm, "end": v(22.5, -111) * mm});
            skLineSegment(sketch, "E1256", {"start": v(22, -111.5) * mm, "end": v(18, -111.5) * mm});
            skArc(sketch, "E1257", {"start": v(18, -111.5) * mm, "mid": v(17.64, -111.35) * mm, "end": v(17.5, -111) * mm});
            skLineSegment(sketch, "E1258", {"start": v(17.5, -109.64) * mm, "end": v(17.5, -111) * mm});
            skArc(sketch, "E1259", {"start": v(17.35, -109.29) * mm, "mid": v(17.46, -109.45) * mm, "end": v(17.5, -109.64) * mm});
            skLineSegment(sketch, "E1260", {"start": v(13.8, -105.74) * mm, "end": v(17.35, -109.29) * mm});
            skArc(sketch, "E1261", {"start": v(13.8, -105.74) * mm, "mid": v(13.7, -105.58) * mm, "end": v(13.66, -105.38) * mm});
            skLineSegment(sketch, "E1262", {"start": v(0.5, -105.63) * mm, "end": v(-0.5, -105.63) * mm});
            skLineSegment(sketch, "E1263", {"start": v(1, -100.37) * mm, "end": v(-1, -100.37) * mm});
            skSolve(sketch);
        }
        {
            var Q0;
            Q0 = qSketchRegion(id + "F8", true);
            extrude(context, id + "F9", {"entities" : qUnion([Q0]), "depth" : 108 * mm, "offsetDistance" : 25 * mm});
        }
        {
            var Q0;
            Q0=qCreatedBy(makeId("Top.planeOp"),FACE);
            var sketch = newSketch(context, id + "F10", { "sketchPlane" : qUnion([Q0])});
            skLineSegment(sketch, "E1264", {"start": v(171.08, -286.53) * mm, "end": v(171.08, -291.3) * mm});
            skLineSegment(sketch, "E1265", {"start": v(156.86, -286.61) * mm, "end": v(157.04, -286.8) * mm});
            skArc(sketch, "E1266", {"start": v(173.93, -286.98) * mm, "mid": v(174.32, -286.86) * mm, "end": v(174.73, -286.82) * mm});
            skArc(sketch, "E1267", {"start": v(172.6, -286.61) * mm, "mid": v(173.37, -286.4) * mm, "end": v(173.93, -286.98) * mm});
            skLineSegment(sketch, "E1268", {"start": v(172.6, -286.61) * mm, "end": v(172.43, -286.8) * mm});
            skArc(sketch, "E1269", {"start": v(172.8, -288.11) * mm, "mid": v(172.23, -287.56) * mm, "end": v(172.43, -286.8) * mm});
            skArc(sketch, "E1270", {"start": v(172.8, -289.72) * mm, "mid": v(172.64, -288.92) * mm, "end": v(172.8, -288.11) * mm});
            skArc(sketch, "E1271", {"start": v(172.43, -291.04) * mm, "mid": v(172.23, -290.27) * mm, "end": v(172.8, -289.72) * mm});
            skLineSegment(sketch, "E1272", {"start": v(172.43, -291.04) * mm, "end": v(172.6, -291.22) * mm});
            skArc(sketch, "E1273", {"start": v(173.93, -290.85) * mm, "mid": v(173.37, -291.42) * mm, "end": v(172.6, -291.22) * mm});
            skArc(sketch, "E1274", {"start": v(174.73, -291.01) * mm, "mid": v(174.32, -290.97) * mm, "end": v(173.93, -290.85) * mm});
            skArc(sketch, "E1275", {"start": v(156.86, -286.61) * mm, "mid": v(156.09, -286.4) * mm, "end": v(155.54, -286.98) * mm});
            skArc(sketch, "E1276", {"start": v(155.54, -286.98) * mm, "mid": v(154.73, -286.82) * mm, "end": v(153.93, -286.98) * mm});
            skArc(sketch, "E1277", {"start": v(153.93, -286.98) * mm, "mid": v(153.37, -286.4) * mm, "end": v(152.6, -286.61) * mm});
            skLineSegment(sketch, "E1278", {"start": v(152.43, -286.8) * mm, "end": v(152.6, -286.61) * mm});
            skArc(sketch, "E1279", {"start": v(152.43, -286.8) * mm, "mid": v(152.23, -287.56) * mm, "end": v(152.8, -288.11) * mm});
            skArc(sketch, "E1280", {"start": v(152.8, -288.11) * mm, "mid": v(152.64, -288.92) * mm, "end": v(152.8, -289.72) * mm});
            skArc(sketch, "E1281", {"start": v(152.8, -289.72) * mm, "mid": v(152.23, -290.27) * mm, "end": v(152.43, -291.04) * mm});
            skLineSegment(sketch, "E1282", {"start": v(152.6, -291.22) * mm, "end": v(152.43, -291.04) * mm});
            skArc(sketch, "E1283", {"start": v(152.6, -291.22) * mm, "mid": v(153.37, -291.42) * mm, "end": v(153.93, -290.85) * mm});
            skArc(sketch, "E1284", {"start": v(153.93, -290.85) * mm, "mid": v(154.73, -291.01) * mm, "end": v(155.54, -290.85) * mm});
            skArc(sketch, "E1285", {"start": v(155.54, -290.85) * mm, "mid": v(156.09, -291.42) * mm, "end": v(156.86, -291.22) * mm});
            skLineSegment(sketch, "E1286", {"start": v(157.04, -291.04) * mm, "end": v(156.86, -291.22) * mm});
            skArc(sketch, "E1287", {"start": v(157.04, -291.04) * mm, "mid": v(157.24, -290.27) * mm, "end": v(156.67, -289.72) * mm});
            skArc(sketch, "E1288", {"start": v(156.67, -289.72) * mm, "mid": v(156.83, -288.92) * mm, "end": v(156.67, -288.11) * mm});
            skArc(sketch, "E1289", {"start": v(156.67, -288.11) * mm, "mid": v(157.24, -287.56) * mm, "end": v(157.04, -286.8) * mm});
            skLineSegment(sketch, "E1290", {"start": v(174.73, -292.57) * mm, "end": v(172.35, -292.57) * mm});
            skArc(sketch, "E1291", {"start": v(171.99, -292.72) * mm, "mid": v(172.15, -292.6) * mm, "end": v(172.35, -292.57) * mm});
            skLineSegment(sketch, "E1292", {"start": v(171.99, -292.72) * mm, "end": v(168.88, -295.82) * mm});
            skArc(sketch, "E1293", {"start": v(168.74, -296.18) * mm, "mid": v(168.77, -295.99) * mm, "end": v(168.88, -295.82) * mm});
            skLineSegment(sketch, "E1294", {"start": v(168.74, -296.18) * mm, "end": v(168.74, -296.9) * mm});
            skArc(sketch, "E1295", {"start": v(169.24, -297.42) * mm, "mid": v(168.88, -297.27) * mm, "end": v(168.74, -296.9) * mm});
            skLineSegment(sketch, "E1296", {"start": v(169.24, -297.42) * mm, "end": v(171.6, -297.42) * mm});
            skArc(sketch, "E1297", {"start": v(171.6, -297.42) * mm, "mid": v(171.95, -297.56) * mm, "end": v(172.1, -297.92) * mm});
            skLineSegment(sketch, "E1298", {"start": v(172.1, -298.4) * mm, "end": v(172.1, -297.92) * mm});
            skArc(sketch, "E1299", {"start": v(172.1, -298.4) * mm, "mid": v(171.95, -298.77) * mm, "end": v(171.6, -298.92) * mm});
            skLineSegment(sketch, "E1300", {"start": v(157.87, -298.92) * mm, "end": v(171.6, -298.92) * mm});
            skArc(sketch, "E1301", {"start": v(157.36, -298.4) * mm, "mid": v(157.5, -298.77) * mm, "end": v(157.87, -298.92) * mm});
            skLineSegment(sketch, "E1302", {"start": v(157.36, -298.4) * mm, "end": v(157.36, -297.92) * mm});
            skArc(sketch, "E1303", {"start": v(157.87, -297.42) * mm, "mid": v(157.5, -297.56) * mm, "end": v(157.36, -297.92) * mm});
            skLineSegment(sketch, "E1304", {"start": v(160.22, -297.42) * mm, "end": v(157.87, -297.42) * mm});
            skArc(sketch, "E1305", {"start": v(160.22, -297.42) * mm, "mid": v(160.58, -297.27) * mm, "end": v(160.73, -296.9) * mm});
            skLineSegment(sketch, "E1306", {"start": v(160.73, -296.18) * mm, "end": v(160.73, -296.9) * mm});
            skArc(sketch, "E1307", {"start": v(160.73, -296.18) * mm, "mid": v(160.69, -295.99) * mm, "end": v(160.58, -295.82) * mm});
            skLineSegment(sketch, "E1308", {"start": v(157.47, -292.72) * mm, "end": v(160.58, -295.82) * mm});
            skArc(sketch, "E1309", {"start": v(157.47, -292.72) * mm, "mid": v(157.3, -292.6) * mm, "end": v(157.12, -292.57) * mm});
            skLineSegment(sketch, "E1310", {"start": v(152.35, -292.57) * mm, "end": v(157.12, -292.57) * mm});
            skArc(sketch, "E1311", {"start": v(152.35, -292.57) * mm, "mid": v(152.15, -292.6) * mm, "end": v(151.99, -292.72) * mm});
            skLineSegment(sketch, "E1312", {"start": v(148.88, -295.82) * mm, "end": v(151.99, -292.72) * mm});
            skArc(sketch, "E1313", {"start": v(148.88, -295.82) * mm, "mid": v(148.77, -295.99) * mm, "end": v(148.74, -296.18) * mm});
            skLineSegment(sketch, "E1314", {"start": v(148.74, -296.18) * mm, "end": v(148.74, -296.9) * mm});
            skArc(sketch, "E1315", {"start": v(148.74, -296.9) * mm, "mid": v(148.88, -297.27) * mm, "end": v(149.24, -297.42) * mm});
            skLineSegment(sketch, "E1316", {"start": v(151.6, -297.42) * mm, "end": v(149.24, -297.42) * mm});
            skArc(sketch, "E1317", {"start": v(152.1, -297.92) * mm, "mid": v(151.95, -297.56) * mm, "end": v(151.6, -297.42) * mm});
            skLineSegment(sketch, "E1318", {"start": v(152.1, -297.92) * mm, "end": v(152.1, -298.4) * mm});
            skArc(sketch, "E1319", {"start": v(151.6, -298.92) * mm, "mid": v(151.95, -298.77) * mm, "end": v(152.1, -298.4) * mm});
            skLineSegment(sketch, "E1320", {"start": v(146.23, -298.92) * mm, "end": v(151.6, -298.92) * mm});
            skArc(sketch, "E1321", {"start": v(144.73, -297.42) * mm, "mid": v(145.17, -298.48) * mm, "end": v(146.23, -298.92) * mm});
            skLineSegment(sketch, "E1322", {"start": v(144.73, -297.42) * mm, "end": v(144.73, -292.05) * mm});
            skArc(sketch, "E1323", {"start": v(145.24, -291.55) * mm, "mid": v(144.88, -291.7) * mm, "end": v(144.73, -292.05) * mm});
            skLineSegment(sketch, "E1324", {"start": v(145.24, -291.55) * mm, "end": v(145.72, -291.55) * mm});
            skArc(sketch, "E1325", {"start": v(146.23, -292.05) * mm, "mid": v(146.08, -291.7) * mm, "end": v(145.72, -291.55) * mm});
            skLineSegment(sketch, "E1326", {"start": v(146.23, -294.4) * mm, "end": v(146.23, -292.05) * mm});
            skArc(sketch, "E1327", {"start": v(146.23, -294.4) * mm, "mid": v(146.38, -294.76) * mm, "end": v(146.74, -294.91) * mm});
            skLineSegment(sketch, "E1328", {"start": v(147.47, -294.91) * mm, "end": v(146.74, -294.91) * mm});
            skArc(sketch, "E1329", {"start": v(147.47, -294.91) * mm, "mid": v(147.66, -294.87) * mm, "end": v(147.82, -294.76) * mm});
            skLineSegment(sketch, "E1330", {"start": v(150.93, -291.66) * mm, "end": v(147.82, -294.76) * mm});
            skArc(sketch, "E1331", {"start": v(150.93, -291.66) * mm, "mid": v(151.04, -291.5) * mm, "end": v(151.08, -291.3) * mm});
            skLineSegment(sketch, "E1332", {"start": v(151.08, -286.53) * mm, "end": v(151.08, -291.3) * mm});
            skArc(sketch, "E1333", {"start": v(151.08, -286.53) * mm, "mid": v(151.04, -286.34) * mm, "end": v(150.93, -286.17) * mm});
            skLineSegment(sketch, "E1334", {"start": v(150.93, -286.17) * mm, "end": v(147.82, -283.07) * mm});
            skArc(sketch, "E1335", {"start": v(147.82, -283.07) * mm, "mid": v(147.66, -282.96) * mm, "end": v(147.47, -282.92) * mm});
            skLineSegment(sketch, "E1336", {"start": v(147.47, -282.92) * mm, "end": v(146.74, -282.92) * mm});
            skArc(sketch, "E1337", {"start": v(146.74, -282.92) * mm, "mid": v(146.38, -283.07) * mm, "end": v(146.23, -283.43) * mm});
            skLineSegment(sketch, "E1338", {"start": v(146.23, -283.43) * mm, "end": v(146.23, -285.78) * mm});
            skArc(sketch, "E1339", {"start": v(145.72, -286.29) * mm, "mid": v(146.08, -286.14) * mm, "end": v(146.23, -285.78) * mm});
            skLineSegment(sketch, "E1340", {"start": v(145.72, -286.29) * mm, "end": v(145.24, -286.29) * mm});
            skArc(sketch, "E1341", {"start": v(144.73, -285.78) * mm, "mid": v(144.88, -286.14) * mm, "end": v(145.24, -286.29) * mm});
            skLineSegment(sketch, "E1342", {"start": v(144.73, -285.78) * mm, "end": v(144.73, -280.42) * mm});
            skArc(sketch, "E1343", {"start": v(146.23, -278.92) * mm, "mid": v(145.17, -279.35) * mm, "end": v(144.73, -280.42) * mm});
            skLineSegment(sketch, "E1344", {"start": v(146.23, -278.92) * mm, "end": v(151.6, -278.92) * mm});
            skArc(sketch, "E1345", {"start": v(152.1, -279.42) * mm, "mid": v(151.95, -279.06) * mm, "end": v(151.6, -278.92) * mm});
            skLineSegment(sketch, "E1346", {"start": v(152.1, -279.42) * mm, "end": v(152.1, -279.9) * mm});
            skArc(sketch, "E1347", {"start": v(151.6, -280.42) * mm, "mid": v(151.95, -280.27) * mm, "end": v(152.1, -279.9) * mm});
            skLineSegment(sketch, "E1348", {"start": v(151.6, -280.42) * mm, "end": v(149.24, -280.42) * mm});
            skArc(sketch, "E1349", {"start": v(149.24, -280.42) * mm, "mid": v(148.88, -280.56) * mm, "end": v(148.74, -280.92) * mm});
            skLineSegment(sketch, "E1350", {"start": v(148.74, -280.92) * mm, "end": v(148.74, -281.65) * mm});
            skArc(sketch, "E1351", {"start": v(148.74, -281.65) * mm, "mid": v(148.77, -281.84) * mm, "end": v(148.88, -282) * mm});
            skLineSegment(sketch, "E1352", {"start": v(148.88, -282) * mm, "end": v(151.99, -285.11) * mm});
            skArc(sketch, "E1353", {"start": v(151.99, -285.11) * mm, "mid": v(152.15, -285.22) * mm, "end": v(152.35, -285.26) * mm});
            skLineSegment(sketch, "E1354", {"start": v(152.35, -285.26) * mm, "end": v(157.12, -285.26) * mm});
            skArc(sketch, "E1355", {"start": v(157.12, -285.26) * mm, "mid": v(157.3, -285.22) * mm, "end": v(157.47, -285.11) * mm});
            skLineSegment(sketch, "E1356", {"start": v(157.47, -285.11) * mm, "end": v(160.58, -282) * mm});
            skArc(sketch, "E1357", {"start": v(160.58, -282) * mm, "mid": v(160.69, -281.84) * mm, "end": v(160.73, -281.65) * mm});
            skLineSegment(sketch, "E1358", {"start": v(160.73, -280.92) * mm, "end": v(160.73, -281.65) * mm});
            skArc(sketch, "E1359", {"start": v(160.73, -280.92) * mm, "mid": v(160.58, -280.56) * mm, "end": v(160.22, -280.42) * mm});
            skLineSegment(sketch, "E1360", {"start": v(160.22, -280.42) * mm, "end": v(157.87, -280.42) * mm});
            skArc(sketch, "E1361", {"start": v(157.36, -279.9) * mm, "mid": v(157.5, -280.27) * mm, "end": v(157.87, -280.42) * mm});
            skLineSegment(sketch, "E1362", {"start": v(157.36, -279.9) * mm, "end": v(157.36, -279.42) * mm});
            skArc(sketch, "E1363", {"start": v(157.87, -278.92) * mm, "mid": v(157.5, -279.06) * mm, "end": v(157.36, -279.42) * mm});
            skLineSegment(sketch, "E1364", {"start": v(171.6, -278.92) * mm, "end": v(157.87, -278.92) * mm});
            skArc(sketch, "E1365", {"start": v(171.6, -278.92) * mm, "mid": v(171.95, -279.06) * mm, "end": v(172.1, -279.42) * mm});
            skLineSegment(sketch, "E1366", {"start": v(172.1, -279.9) * mm, "end": v(172.1, -279.42) * mm});
            skArc(sketch, "E1367", {"start": v(172.1, -279.9) * mm, "mid": v(171.95, -280.27) * mm, "end": v(171.6, -280.42) * mm});
            skLineSegment(sketch, "E1368", {"start": v(169.24, -280.42) * mm, "end": v(171.6, -280.42) * mm});
            skArc(sketch, "E1369", {"start": v(168.74, -280.92) * mm, "mid": v(168.88, -280.56) * mm, "end": v(169.24, -280.42) * mm});
            skLineSegment(sketch, "E1370", {"start": v(168.74, -280.92) * mm, "end": v(168.74, -281.65) * mm});
            skArc(sketch, "E1371", {"start": v(168.88, -282) * mm, "mid": v(168.77, -281.84) * mm, "end": v(168.74, -281.65) * mm});
            skLineSegment(sketch, "E1372", {"start": v(171.99, -285.11) * mm, "end": v(168.88, -282) * mm});
            skArc(sketch, "E1373", {"start": v(172.35, -285.26) * mm, "mid": v(172.15, -285.22) * mm, "end": v(171.99, -285.11) * mm});
            skLineSegment(sketch, "E1374", {"start": v(174.73, -285.26) * mm, "end": v(172.35, -285.26) * mm});
            skArc(sketch, "E1375", {"start": v(171.08, -286.53) * mm, "mid": v(171.04, -286.34) * mm, "end": v(170.93, -286.17) * mm});
            skLineSegment(sketch, "E1376", {"start": v(170.93, -286.17) * mm, "end": v(167.38, -282.63) * mm});
            skArc(sketch, "E1377", {"start": v(167.38, -282.63) * mm, "mid": v(167.27, -282.47) * mm, "end": v(167.24, -282.27) * mm});
            skLineSegment(sketch, "E1378", {"start": v(167.24, -280.92) * mm, "end": v(167.24, -282.27) * mm});
            skArc(sketch, "E1379", {"start": v(166.73, -280.42) * mm, "mid": v(167.09, -280.56) * mm, "end": v(167.24, -280.92) * mm});
            skLineSegment(sketch, "E1380", {"start": v(162.73, -280.42) * mm, "end": v(166.73, -280.42) * mm});
            skArc(sketch, "E1381", {"start": v(162.73, -280.42) * mm, "mid": v(162.37, -280.56) * mm, "end": v(162.23, -280.92) * mm});
            skLineSegment(sketch, "E1382", {"start": v(162.23, -280.92) * mm, "end": v(162.23, -282.27) * mm});
            skArc(sketch, "E1383", {"start": v(162.08, -282.63) * mm, "mid": v(162.19, -282.47) * mm, "end": v(162.23, -282.27) * mm});
            skLineSegment(sketch, "E1384", {"start": v(158.53, -286.17) * mm, "end": v(162.08, -282.63) * mm});
            skArc(sketch, "E1385", {"start": v(158.53, -286.17) * mm, "mid": v(158.42, -286.34) * mm, "end": v(158.39, -286.53) * mm});
            skLineSegment(sketch, "E1386", {"start": v(158.39, -286.53) * mm, "end": v(158.39, -291.3) * mm});
            skArc(sketch, "E1387", {"start": v(158.39, -291.3) * mm, "mid": v(158.42, -291.5) * mm, "end": v(158.53, -291.66) * mm});
            skLineSegment(sketch, "E1388", {"start": v(158.53, -291.66) * mm, "end": v(162.08, -295.2) * mm});
            skArc(sketch, "E1389", {"start": v(162.23, -295.56) * mm, "mid": v(162.19, -295.37) * mm, "end": v(162.08, -295.2) * mm});
            skLineSegment(sketch, "E1390", {"start": v(162.23, -295.56) * mm, "end": v(162.23, -296.9) * mm});
            skArc(sketch, "E1391", {"start": v(162.23, -296.9) * mm, "mid": v(162.37, -297.27) * mm, "end": v(162.73, -297.42) * mm});
            skLineSegment(sketch, "E1392", {"start": v(162.73, -297.42) * mm, "end": v(166.73, -297.42) * mm});
            skArc(sketch, "E1393", {"start": v(167.24, -296.9) * mm, "mid": v(167.09, -297.27) * mm, "end": v(166.73, -297.42) * mm});
            skLineSegment(sketch, "E1394", {"start": v(167.24, -295.56) * mm, "end": v(167.24, -296.9) * mm});
            skArc(sketch, "E1395", {"start": v(167.24, -295.56) * mm, "mid": v(167.27, -295.37) * mm, "end": v(167.38, -295.2) * mm});
            skLineSegment(sketch, "E1396", {"start": v(170.93, -291.66) * mm, "end": v(167.38, -295.2) * mm});
            skArc(sketch, "E1397", {"start": v(171.08, -291.3) * mm, "mid": v(171.04, -291.5) * mm, "end": v(170.93, -291.66) * mm});
            skLineSegment(sketch, "E1398", {"start": v(178.39, -286.53) * mm, "end": v(178.39, -291.3) * mm});
            skLineSegment(sketch, "E1399", {"start": v(192.6, -286.61) * mm, "end": v(192.43, -286.8) * mm});
            skArc(sketch, "E1400", {"start": v(175.54, -286.98) * mm, "mid": v(176.09, -286.4) * mm, "end": v(176.86, -286.61) * mm});
            skLineSegment(sketch, "E1401", {"start": v(176.86, -286.61) * mm, "end": v(177.04, -286.8) * mm});
            skArc(sketch, "E1402", {"start": v(177.04, -286.8) * mm, "mid": v(177.24, -287.56) * mm, "end": v(176.67, -288.11) * mm});
            skArc(sketch, "E1403", {"start": v(176.67, -288.11) * mm, "mid": v(176.83, -288.92) * mm, "end": v(176.67, -289.72) * mm});
            skArc(sketch, "E1404", {"start": v(176.67, -289.72) * mm, "mid": v(177.24, -290.27) * mm, "end": v(177.04, -291.04) * mm});
            skLineSegment(sketch, "E1405", {"start": v(177.04, -291.04) * mm, "end": v(176.86, -291.22) * mm});
            skArc(sketch, "E1406", {"start": v(176.86, -291.22) * mm, "mid": v(176.09, -291.42) * mm, "end": v(175.54, -290.85) * mm});
            skArc(sketch, "E1407", {"start": v(193.93, -286.98) * mm, "mid": v(193.37, -286.4) * mm, "end": v(192.6, -286.61) * mm});
            skArc(sketch, "E1408", {"start": v(195.54, -286.98) * mm, "mid": v(194.73, -286.82) * mm, "end": v(193.93, -286.98) * mm});
            skArc(sketch, "E1409", {"start": v(196.86, -286.61) * mm, "mid": v(196.09, -286.4) * mm, "end": v(195.54, -286.98) * mm});
            skLineSegment(sketch, "E1410", {"start": v(197.04, -286.8) * mm, "end": v(196.86, -286.61) * mm});
            skArc(sketch, "E1411", {"start": v(196.67, -288.11) * mm, "mid": v(197.24, -287.56) * mm, "end": v(197.04, -286.8) * mm});
            skArc(sketch, "E1412", {"start": v(196.67, -289.72) * mm, "mid": v(196.83, -288.92) * mm, "end": v(196.67, -288.11) * mm});
            skArc(sketch, "E1413", {"start": v(197.04, -291.04) * mm, "mid": v(197.24, -290.27) * mm, "end": v(196.67, -289.72) * mm});
            skLineSegment(sketch, "E1414", {"start": v(196.86, -291.22) * mm, "end": v(197.04, -291.04) * mm});
            skArc(sketch, "E1415", {"start": v(195.54, -290.85) * mm, "mid": v(196.09, -291.42) * mm, "end": v(196.86, -291.22) * mm});
            skArc(sketch, "E1416", {"start": v(193.93, -290.85) * mm, "mid": v(194.73, -291.01) * mm, "end": v(195.54, -290.85) * mm});
            skArc(sketch, "E1417", {"start": v(192.6, -291.22) * mm, "mid": v(193.37, -291.42) * mm, "end": v(193.93, -290.85) * mm});
            skLineSegment(sketch, "E1418", {"start": v(192.43, -291.04) * mm, "end": v(192.6, -291.22) * mm});
            skArc(sketch, "E1419", {"start": v(192.8, -289.72) * mm, "mid": v(192.23, -290.27) * mm, "end": v(192.43, -291.04) * mm});
            skArc(sketch, "E1420", {"start": v(192.8, -288.11) * mm, "mid": v(192.64, -288.92) * mm, "end": v(192.8, -289.72) * mm});
            skArc(sketch, "E1421", {"start": v(192.43, -286.8) * mm, "mid": v(192.23, -287.56) * mm, "end": v(192.8, -288.11) * mm});
            skLineSegment(sketch, "E1422", {"start": v(174.73, -292.57) * mm, "end": v(177.12, -292.57) * mm});
            skArc(sketch, "E1423", {"start": v(177.12, -292.57) * mm, "mid": v(177.3, -292.6) * mm, "end": v(177.47, -292.72) * mm});
            skLineSegment(sketch, "E1424", {"start": v(177.47, -292.72) * mm, "end": v(180.58, -295.82) * mm});
            skArc(sketch, "E1425", {"start": v(180.58, -295.82) * mm, "mid": v(180.69, -295.99) * mm, "end": v(180.73, -296.18) * mm});
            skLineSegment(sketch, "E1426", {"start": v(180.73, -296.18) * mm, "end": v(180.73, -296.9) * mm});
            skArc(sketch, "E1427", {"start": v(180.73, -296.9) * mm, "mid": v(180.58, -297.27) * mm, "end": v(180.22, -297.42) * mm});
            skLineSegment(sketch, "E1428", {"start": v(180.22, -297.42) * mm, "end": v(177.87, -297.42) * mm});
            skArc(sketch, "E1429", {"start": v(177.36, -297.92) * mm, "mid": v(177.5, -297.56) * mm, "end": v(177.87, -297.42) * mm});
            skLineSegment(sketch, "E1430", {"start": v(177.36, -298.4) * mm, "end": v(177.36, -297.92) * mm});
            skArc(sketch, "E1431", {"start": v(177.87, -298.92) * mm, "mid": v(177.5, -298.77) * mm, "end": v(177.36, -298.4) * mm});
            skLineSegment(sketch, "E1432", {"start": v(191.6, -298.92) * mm, "end": v(177.87, -298.92) * mm});
            skArc(sketch, "E1433", {"start": v(191.6, -298.92) * mm, "mid": v(191.95, -298.77) * mm, "end": v(192.1, -298.4) * mm});
            skLineSegment(sketch, "E1434", {"start": v(192.1, -298.4) * mm, "end": v(192.1, -297.92) * mm});
            skArc(sketch, "E1435", {"start": v(192.1, -297.92) * mm, "mid": v(191.95, -297.56) * mm, "end": v(191.6, -297.42) * mm});
            skLineSegment(sketch, "E1436", {"start": v(189.24, -297.42) * mm, "end": v(191.6, -297.42) * mm});
            skArc(sketch, "E1437", {"start": v(188.74, -296.9) * mm, "mid": v(188.88, -297.27) * mm, "end": v(189.24, -297.42) * mm});
            skLineSegment(sketch, "E1438", {"start": v(188.74, -296.18) * mm, "end": v(188.74, -296.9) * mm});
            skArc(sketch, "E1439", {"start": v(188.88, -295.82) * mm, "mid": v(188.77, -295.99) * mm, "end": v(188.74, -296.18) * mm});
            skLineSegment(sketch, "E1440", {"start": v(191.99, -292.72) * mm, "end": v(188.88, -295.82) * mm});
            skArc(sketch, "E1441", {"start": v(192.35, -292.57) * mm, "mid": v(192.15, -292.6) * mm, "end": v(191.99, -292.72) * mm});
            skLineSegment(sketch, "E1442", {"start": v(197.12, -292.57) * mm, "end": v(192.35, -292.57) * mm});
            skArc(sketch, "E1443", {"start": v(197.47, -292.72) * mm, "mid": v(197.3, -292.6) * mm, "end": v(197.12, -292.57) * mm});
            skLineSegment(sketch, "E1444", {"start": v(200.58, -295.82) * mm, "end": v(197.47, -292.72) * mm});
            skArc(sketch, "E1445", {"start": v(200.73, -296.18) * mm, "mid": v(200.69, -295.99) * mm, "end": v(200.58, -295.82) * mm});
            skLineSegment(sketch, "E1446", {"start": v(200.73, -296.18) * mm, "end": v(200.73, -296.9) * mm});
            skArc(sketch, "E1447", {"start": v(200.22, -297.42) * mm, "mid": v(200.58, -297.27) * mm, "end": v(200.73, -296.9) * mm});
            skLineSegment(sketch, "E1448", {"start": v(197.87, -297.42) * mm, "end": v(200.22, -297.42) * mm});
            skArc(sketch, "E1449", {"start": v(197.87, -297.42) * mm, "mid": v(197.5, -297.56) * mm, "end": v(197.36, -297.92) * mm});
            skLineSegment(sketch, "E1450", {"start": v(197.36, -297.92) * mm, "end": v(197.36, -298.4) * mm});
            skArc(sketch, "E1451", {"start": v(197.36, -298.4) * mm, "mid": v(197.5, -298.77) * mm, "end": v(197.87, -298.92) * mm});
            skLineSegment(sketch, "E1452", {"start": v(203.23, -298.92) * mm, "end": v(197.87, -298.92) * mm});
            skArc(sketch, "E1453", {"start": v(203.23, -298.92) * mm, "mid": v(204.3, -298.48) * mm, "end": v(204.73, -297.42) * mm});
            skLineSegment(sketch, "E1454", {"start": v(204.73, -297.42) * mm, "end": v(204.73, -292.05) * mm});
            skArc(sketch, "E1455", {"start": v(204.73, -292.05) * mm, "mid": v(204.58, -291.7) * mm, "end": v(204.22, -291.55) * mm});
            skLineSegment(sketch, "E1456", {"start": v(204.22, -291.55) * mm, "end": v(203.74, -291.55) * mm});
            skArc(sketch, "E1457", {"start": v(203.74, -291.55) * mm, "mid": v(203.38, -291.7) * mm, "end": v(203.23, -292.05) * mm});
            skLineSegment(sketch, "E1458", {"start": v(203.23, -294.4) * mm, "end": v(203.23, -292.05) * mm});
            skArc(sketch, "E1459", {"start": v(202.72, -294.91) * mm, "mid": v(203.08, -294.76) * mm, "end": v(203.23, -294.4) * mm});
            skLineSegment(sketch, "E1460", {"start": v(202, -294.91) * mm, "end": v(202.72, -294.91) * mm});
            skArc(sketch, "E1461", {"start": v(201.64, -294.76) * mm, "mid": v(201.8, -294.87) * mm, "end": v(202, -294.91) * mm});
            skLineSegment(sketch, "E1462", {"start": v(198.53, -291.66) * mm, "end": v(201.64, -294.76) * mm});
            skArc(sketch, "E1463", {"start": v(198.39, -291.3) * mm, "mid": v(198.42, -291.5) * mm, "end": v(198.53, -291.66) * mm});
            skLineSegment(sketch, "E1464", {"start": v(198.39, -286.53) * mm, "end": v(198.39, -291.3) * mm});
            skArc(sketch, "E1465", {"start": v(198.53, -286.17) * mm, "mid": v(198.42, -286.34) * mm, "end": v(198.39, -286.53) * mm});
            skLineSegment(sketch, "E1466", {"start": v(198.53, -286.17) * mm, "end": v(201.64, -283.07) * mm});
            skArc(sketch, "E1467", {"start": v(202, -282.92) * mm, "mid": v(201.8, -282.96) * mm, "end": v(201.64, -283.07) * mm});
            skLineSegment(sketch, "E1468", {"start": v(202, -282.92) * mm, "end": v(202.72, -282.92) * mm});
            skArc(sketch, "E1469", {"start": v(203.23, -283.43) * mm, "mid": v(203.08, -283.07) * mm, "end": v(202.72, -282.92) * mm});
            skLineSegment(sketch, "E1470", {"start": v(203.23, -283.43) * mm, "end": v(203.23, -285.78) * mm});
            skArc(sketch, "E1471", {"start": v(203.23, -285.78) * mm, "mid": v(203.38, -286.14) * mm, "end": v(203.74, -286.29) * mm});
            skLineSegment(sketch, "E1472", {"start": v(203.74, -286.29) * mm, "end": v(204.22, -286.29) * mm});
            skArc(sketch, "E1473", {"start": v(204.22, -286.29) * mm, "mid": v(204.58, -286.14) * mm, "end": v(204.73, -285.78) * mm});
            skLineSegment(sketch, "E1474", {"start": v(204.73, -285.78) * mm, "end": v(204.73, -280.42) * mm});
            skArc(sketch, "E1475", {"start": v(204.73, -280.42) * mm, "mid": v(204.3, -279.35) * mm, "end": v(203.23, -278.92) * mm});
            skLineSegment(sketch, "E1476", {"start": v(203.23, -278.92) * mm, "end": v(197.87, -278.92) * mm});
            skArc(sketch, "E1477", {"start": v(197.87, -278.92) * mm, "mid": v(197.5, -279.06) * mm, "end": v(197.36, -279.42) * mm});
            skLineSegment(sketch, "E1478", {"start": v(197.36, -279.42) * mm, "end": v(197.36, -279.9) * mm});
            skArc(sketch, "E1479", {"start": v(197.36, -279.9) * mm, "mid": v(197.5, -280.27) * mm, "end": v(197.87, -280.42) * mm});
            skLineSegment(sketch, "E1480", {"start": v(197.87, -280.42) * mm, "end": v(200.22, -280.42) * mm});
            skArc(sketch, "E1481", {"start": v(200.73, -280.92) * mm, "mid": v(200.58, -280.56) * mm, "end": v(200.22, -280.42) * mm});
            skLineSegment(sketch, "E1482", {"start": v(200.73, -280.92) * mm, "end": v(200.73, -281.65) * mm});
            skArc(sketch, "E1483", {"start": v(200.58, -282) * mm, "mid": v(200.69, -281.84) * mm, "end": v(200.73, -281.65) * mm});
            skLineSegment(sketch, "E1484", {"start": v(200.58, -282) * mm, "end": v(197.47, -285.11) * mm});
            skArc(sketch, "E1485", {"start": v(197.12, -285.26) * mm, "mid": v(197.3, -285.22) * mm, "end": v(197.47, -285.11) * mm});
            skLineSegment(sketch, "E1486", {"start": v(197.12, -285.26) * mm, "end": v(192.35, -285.26) * mm});
            skArc(sketch, "E1487", {"start": v(191.99, -285.11) * mm, "mid": v(192.15, -285.22) * mm, "end": v(192.35, -285.26) * mm});
            skLineSegment(sketch, "E1488", {"start": v(191.99, -285.11) * mm, "end": v(188.88, -282) * mm});
            skArc(sketch, "E1489", {"start": v(188.74, -281.65) * mm, "mid": v(188.77, -281.84) * mm, "end": v(188.88, -282) * mm});
            skLineSegment(sketch, "E1490", {"start": v(188.74, -280.92) * mm, "end": v(188.74, -281.65) * mm});
            skArc(sketch, "E1491", {"start": v(189.24, -280.42) * mm, "mid": v(188.88, -280.56) * mm, "end": v(188.74, -280.92) * mm});
            skLineSegment(sketch, "E1492", {"start": v(189.24, -280.42) * mm, "end": v(191.6, -280.42) * mm});
            skArc(sketch, "E1493", {"start": v(191.6, -280.42) * mm, "mid": v(191.95, -280.27) * mm, "end": v(192.1, -279.9) * mm});
            skLineSegment(sketch, "E1494", {"start": v(192.1, -279.9) * mm, "end": v(192.1, -279.42) * mm});
            skArc(sketch, "E1495", {"start": v(192.1, -279.42) * mm, "mid": v(191.95, -279.06) * mm, "end": v(191.6, -278.92) * mm});
            skLineSegment(sketch, "E1496", {"start": v(177.87, -278.92) * mm, "end": v(191.6, -278.92) * mm});
            skArc(sketch, "E1497", {"start": v(177.36, -279.42) * mm, "mid": v(177.5, -279.06) * mm, "end": v(177.87, -278.92) * mm});
            skLineSegment(sketch, "E1498", {"start": v(177.36, -279.9) * mm, "end": v(177.36, -279.42) * mm});
            skArc(sketch, "E1499", {"start": v(177.87, -280.42) * mm, "mid": v(177.5, -280.27) * mm, "end": v(177.36, -279.9) * mm});
            skLineSegment(sketch, "E1500", {"start": v(180.22, -280.42) * mm, "end": v(177.87, -280.42) * mm});
            skArc(sketch, "E1501", {"start": v(180.22, -280.42) * mm, "mid": v(180.58, -280.56) * mm, "end": v(180.73, -280.92) * mm});
            skLineSegment(sketch, "E1502", {"start": v(180.73, -280.92) * mm, "end": v(180.73, -281.65) * mm});
            skArc(sketch, "E1503", {"start": v(180.73, -281.65) * mm, "mid": v(180.69, -281.84) * mm, "end": v(180.58, -282) * mm});
            skLineSegment(sketch, "E1504", {"start": v(177.47, -285.11) * mm, "end": v(180.58, -282) * mm});
            skArc(sketch, "E1505", {"start": v(177.47, -285.11) * mm, "mid": v(177.3, -285.22) * mm, "end": v(177.12, -285.26) * mm});
            skLineSegment(sketch, "E1506", {"start": v(174.73, -285.26) * mm, "end": v(177.12, -285.26) * mm});
            skArc(sketch, "E1507", {"start": v(178.53, -286.17) * mm, "mid": v(178.42, -286.34) * mm, "end": v(178.39, -286.53) * mm});
            skLineSegment(sketch, "E1508", {"start": v(178.53, -286.17) * mm, "end": v(182.08, -282.63) * mm});
            skArc(sketch, "E1509", {"start": v(182.23, -282.27) * mm, "mid": v(182.19, -282.47) * mm, "end": v(182.08, -282.63) * mm});
            skLineSegment(sketch, "E1510", {"start": v(182.23, -280.92) * mm, "end": v(182.23, -282.27) * mm});
            skArc(sketch, "E1511", {"start": v(182.23, -280.92) * mm, "mid": v(182.37, -280.56) * mm, "end": v(182.73, -280.42) * mm});
            skLineSegment(sketch, "E1512", {"start": v(186.73, -280.42) * mm, "end": v(182.73, -280.42) * mm});
            skArc(sketch, "E1513", {"start": v(187.24, -280.92) * mm, "mid": v(187.09, -280.56) * mm, "end": v(186.73, -280.42) * mm});
            skLineSegment(sketch, "E1514", {"start": v(187.24, -280.92) * mm, "end": v(187.24, -282.27) * mm});
            skArc(sketch, "E1515", {"start": v(187.24, -282.27) * mm, "mid": v(187.27, -282.47) * mm, "end": v(187.38, -282.63) * mm});
            skLineSegment(sketch, "E1516", {"start": v(190.93, -286.17) * mm, "end": v(187.38, -282.63) * mm});
            skArc(sketch, "E1517", {"start": v(191.08, -286.53) * mm, "mid": v(191.04, -286.34) * mm, "end": v(190.93, -286.17) * mm});
            skLineSegment(sketch, "E1518", {"start": v(191.08, -286.53) * mm, "end": v(191.08, -291.3) * mm});
            skArc(sketch, "E1519", {"start": v(190.93, -291.66) * mm, "mid": v(191.04, -291.5) * mm, "end": v(191.08, -291.3) * mm});
            skLineSegment(sketch, "E1520", {"start": v(190.93, -291.66) * mm, "end": v(187.38, -295.2) * mm});
            skArc(sketch, "E1521", {"start": v(187.38, -295.2) * mm, "mid": v(187.27, -295.37) * mm, "end": v(187.24, -295.56) * mm});
            skLineSegment(sketch, "E1522", {"start": v(187.24, -295.56) * mm, "end": v(187.24, -296.9) * mm});
            skArc(sketch, "E1523", {"start": v(186.73, -297.42) * mm, "mid": v(187.09, -297.27) * mm, "end": v(187.24, -296.9) * mm});
            skLineSegment(sketch, "E1524", {"start": v(186.73, -297.42) * mm, "end": v(182.73, -297.42) * mm});
            skArc(sketch, "E1525", {"start": v(182.73, -297.42) * mm, "mid": v(182.37, -297.27) * mm, "end": v(182.23, -296.9) * mm});
            skLineSegment(sketch, "E1526", {"start": v(182.23, -295.56) * mm, "end": v(182.23, -296.9) * mm});
            skArc(sketch, "E1527", {"start": v(182.08, -295.2) * mm, "mid": v(182.19, -295.37) * mm, "end": v(182.23, -295.56) * mm});
            skLineSegment(sketch, "E1528", {"start": v(178.53, -291.66) * mm, "end": v(182.08, -295.2) * mm});
            skArc(sketch, "E1529", {"start": v(178.53, -291.66) * mm, "mid": v(178.42, -291.5) * mm, "end": v(178.39, -291.3) * mm});
            skArc(sketch, "E1530", {"start": v(174.73, -286.82) * mm, "mid": v(175.14, -286.86) * mm, "end": v(175.54, -286.98) * mm});
            skArc(sketch, "E1531", {"start": v(175.54, -290.85) * mm, "mid": v(175.14, -290.97) * mm, "end": v(174.73, -291.01) * mm});
            skSolve(sketch);
        }
        {
            var Q0;
            Q0 = qSketchRegion(id + "F10", true);
            extrude(context, id + "F11", {"entities" : qUnion([Q0]), "depth" : 400 * mm, "offsetDistance" : 25 * mm});
        }
        {
            var Q0;
            Q0=qCreatedBy(makeId("Top.planeOp"),FACE);
            var sketch = newSketch(context, id + "F12", { "sketchPlane" : qUnion([Q0])});
            skLineSegment(sketch, "E1532", {"start": v(-138.16, 2.38) * mm, "end": v(-138.16, -2.38) * mm});
            skArc(sketch, "E1533", {"start": v(-133.7, 1.94) * mm, "mid": v(-133.14, 2.5) * mm, "end": v(-132.38, 2.3) * mm});
            skLineSegment(sketch, "E1534", {"start": v(-152.38, 2.3) * mm, "end": v(-152.2, 2.12) * mm});
            skLineSegment(sketch, "E1535", {"start": v(-131.87, -9) * mm, "end": v(-131.87, -9.5) * mm});
            skArc(sketch, "E1536", {"start": v(-135.3, 1.94) * mm, "mid": v(-134.5, 2.1) * mm, "end": v(-133.7, 1.94) * mm});
            skArc(sketch, "E1537", {"start": v(-136.62, 2.3) * mm, "mid": v(-135.86, 2.5) * mm, "end": v(-135.3, 1.94) * mm});
            skLineSegment(sketch, "E1538", {"start": v(-136.62, 2.3) * mm, "end": v(-136.8, 2.12) * mm});
            skArc(sketch, "E1539", {"start": v(-136.44, 0.8) * mm, "mid": v(-137, 1.36) * mm, "end": v(-136.8, 2.12) * mm});
            skArc(sketch, "E1540", {"start": v(-136.44, -0.8) * mm, "mid": v(-136.6, 0) * mm, "end": v(-136.44, 0.8) * mm});
            skArc(sketch, "E1541", {"start": v(-136.8, -2.12) * mm, "mid": v(-137, -1.36) * mm, "end": v(-136.44, -0.8) * mm});
            skLineSegment(sketch, "E1542", {"start": v(-136.8, -2.12) * mm, "end": v(-136.62, -2.3) * mm});
            skArc(sketch, "E1543", {"start": v(-135.3, -1.94) * mm, "mid": v(-135.86, -2.5) * mm, "end": v(-136.62, -2.3) * mm});
            skArc(sketch, "E1544", {"start": v(-133.7, -1.94) * mm, "mid": v(-134.5, -2.1) * mm, "end": v(-135.3, -1.94) * mm});
            skArc(sketch, "E1545", {"start": v(-132.38, -2.3) * mm, "mid": v(-133.14, -2.5) * mm, "end": v(-133.7, -1.94) * mm});
            skLineSegment(sketch, "E1546", {"start": v(-132.38, -2.3) * mm, "end": v(-132.2, -2.12) * mm});
            skArc(sketch, "E1547", {"start": v(-132.56, -0.8) * mm, "mid": v(-132, -1.36) * mm, "end": v(-132.2, -2.12) * mm});
            skArc(sketch, "E1548", {"start": v(-132.56, 0.8) * mm, "mid": v(-132.4, 0) * mm, "end": v(-132.56, -0.8) * mm});
            skArc(sketch, "E1549", {"start": v(-132.2, 2.12) * mm, "mid": v(-132, 1.36) * mm, "end": v(-132.56, 0.8) * mm});
            skLineSegment(sketch, "E1550", {"start": v(-132.2, 2.12) * mm, "end": v(-132.38, 2.3) * mm});
            skArc(sketch, "E1551", {"start": v(-152.38, 2.3) * mm, "mid": v(-153.14, 2.5) * mm, "end": v(-153.7, 1.94) * mm});
            skArc(sketch, "E1552", {"start": v(-153.7, 1.94) * mm, "mid": v(-154.5, 2.1) * mm, "end": v(-155.3, 1.94) * mm});
            skArc(sketch, "E1553", {"start": v(-155.3, 1.94) * mm, "mid": v(-155.86, 2.5) * mm, "end": v(-156.62, 2.3) * mm});
            skLineSegment(sketch, "E1554", {"start": v(-156.8, 2.12) * mm, "end": v(-156.62, 2.3) * mm});
            skArc(sketch, "E1555", {"start": v(-156.8, 2.12) * mm, "mid": v(-157, 1.36) * mm, "end": v(-156.44, 0.8) * mm});
            skArc(sketch, "E1556", {"start": v(-156.44, 0.8) * mm, "mid": v(-156.6, 0) * mm, "end": v(-156.44, -0.8) * mm});
            skArc(sketch, "E1557", {"start": v(-156.44, -0.8) * mm, "mid": v(-157, -1.36) * mm, "end": v(-156.8, -2.12) * mm});
            skLineSegment(sketch, "E1558", {"start": v(-156.62, -2.3) * mm, "end": v(-156.8, -2.12) * mm});
            skArc(sketch, "E1559", {"start": v(-156.62, -2.3) * mm, "mid": v(-155.86, -2.5) * mm, "end": v(-155.3, -1.94) * mm});
            skArc(sketch, "E1560", {"start": v(-155.3, -1.94) * mm, "mid": v(-154.5, -2.1) * mm, "end": v(-153.7, -1.94) * mm});
            skArc(sketch, "E1561", {"start": v(-153.7, -1.94) * mm, "mid": v(-153.14, -2.5) * mm, "end": v(-152.38, -2.3) * mm});
            skLineSegment(sketch, "E1562", {"start": v(-152.2, -2.12) * mm, "end": v(-152.38, -2.3) * mm});
            skArc(sketch, "E1563", {"start": v(-152.2, -2.12) * mm, "mid": v(-152, -1.36) * mm, "end": v(-152.56, -0.8) * mm});
            skArc(sketch, "E1564", {"start": v(-152.56, -0.8) * mm, "mid": v(-152.4, 0) * mm, "end": v(-152.56, 0.8) * mm});
            skArc(sketch, "E1565", {"start": v(-152.56, 0.8) * mm, "mid": v(-152, 1.36) * mm, "end": v(-152.2, 2.12) * mm});
            skArc(sketch, "E1566", {"start": v(-131.87, -9) * mm, "mid": v(-131.72, -8.65) * mm, "end": v(-131.36, -8.5) * mm});
            skLineSegment(sketch, "E1567", {"start": v(-131.36, -8.5) * mm, "end": v(-129.01, -8.5) * mm});
            skArc(sketch, "E1568", {"start": v(-128.5, -8) * mm, "mid": v(-128.65, -8.35) * mm, "end": v(-129.01, -8.5) * mm});
            skLineSegment(sketch, "E1569", {"start": v(-128.5, -7.27) * mm, "end": v(-128.5, -8) * mm});
            skArc(sketch, "E1570", {"start": v(-128.65, -6.9) * mm, "mid": v(-128.54, -7.07) * mm, "end": v(-128.5, -7.27) * mm});
            skLineSegment(sketch, "E1571", {"start": v(-128.65, -6.9) * mm, "end": v(-131.76, -3.8) * mm});
            skArc(sketch, "E1572", {"start": v(-132.12, -3.66) * mm, "mid": v(-131.92, -3.7) * mm, "end": v(-131.76, -3.8) * mm});
            skLineSegment(sketch, "E1573", {"start": v(-132.12, -3.65) * mm, "end": v(-136.88, -3.65) * mm});
            skArc(sketch, "E1574", {"start": v(-137.24, -3.8) * mm, "mid": v(-137.08, -3.7) * mm, "end": v(-136.88, -3.66) * mm});
            skLineSegment(sketch, "E1575", {"start": v(-137.24, -3.8) * mm, "end": v(-140.35, -6.9) * mm});
            skArc(sketch, "E1576", {"start": v(-140.5, -7.27) * mm, "mid": v(-140.46, -7.07) * mm, "end": v(-140.35, -6.9) * mm});
            skLineSegment(sketch, "E1577", {"start": v(-140.5, -7.27) * mm, "end": v(-140.5, -8) * mm});
            skArc(sketch, "E1578", {"start": v(-139.99, -8.5) * mm, "mid": v(-140.35, -8.35) * mm, "end": v(-140.5, -8) * mm});
            skLineSegment(sketch, "E1579", {"start": v(-139.99, -8.5) * mm, "end": v(-137.64, -8.5) * mm});
            skArc(sketch, "E1580", {"start": v(-137.64, -8.5) * mm, "mid": v(-137.28, -8.65) * mm, "end": v(-137.13, -9) * mm});
            skLineSegment(sketch, "E1581", {"start": v(-137.13, -9.5) * mm, "end": v(-137.13, -9) * mm});
            skArc(sketch, "E1582", {"start": v(-137.13, -9.5) * mm, "mid": v(-137.28, -9.85) * mm, "end": v(-137.64, -10) * mm});
            skLineSegment(sketch, "E1583", {"start": v(-151.36, -10) * mm, "end": v(-137.64, -10) * mm});
            skArc(sketch, "E1584", {"start": v(-151.87, -9.5) * mm, "mid": v(-151.72, -9.85) * mm, "end": v(-151.36, -10) * mm});
            skLineSegment(sketch, "E1585", {"start": v(-151.87, -9.5) * mm, "end": v(-151.87, -9) * mm});
            skArc(sketch, "E1586", {"start": v(-151.36, -8.5) * mm, "mid": v(-151.72, -8.65) * mm, "end": v(-151.87, -9) * mm});
            skLineSegment(sketch, "E1587", {"start": v(-149.01, -8.5) * mm, "end": v(-151.36, -8.5) * mm});
            skArc(sketch, "E1588", {"start": v(-149.01, -8.5) * mm, "mid": v(-148.65, -8.35) * mm, "end": v(-148.5, -8) * mm});
            skLineSegment(sketch, "E1589", {"start": v(-148.5, -7.27) * mm, "end": v(-148.5, -8) * mm});
            skArc(sketch, "E1590", {"start": v(-148.5, -7.27) * mm, "mid": v(-148.54, -7.07) * mm, "end": v(-148.65, -6.9) * mm});
            skLineSegment(sketch, "E1591", {"start": v(-151.76, -3.8) * mm, "end": v(-148.65, -6.9) * mm});
            skArc(sketch, "E1592", {"start": v(-151.76, -3.8) * mm, "mid": v(-151.92, -3.7) * mm, "end": v(-152.12, -3.66) * mm});
            skLineSegment(sketch, "E1593", {"start": v(-156.88, -3.65) * mm, "end": v(-152.12, -3.65) * mm});
            skArc(sketch, "E1594", {"start": v(-156.88, -3.66) * mm, "mid": v(-157.08, -3.7) * mm, "end": v(-157.24, -3.8) * mm});
            skLineSegment(sketch, "E1595", {"start": v(-160.35, -6.9) * mm, "end": v(-157.24, -3.8) * mm});
            skArc(sketch, "E1596", {"start": v(-160.35, -6.9) * mm, "mid": v(-160.46, -7.07) * mm, "end": v(-160.5, -7.27) * mm});
            skLineSegment(sketch, "E1597", {"start": v(-160.5, -7.27) * mm, "end": v(-160.5, -8) * mm});
            skArc(sketch, "E1598", {"start": v(-160.5, -8) * mm, "mid": v(-160.35, -8.35) * mm, "end": v(-159.99, -8.5) * mm});
            skLineSegment(sketch, "E1599", {"start": v(-157.64, -8.5) * mm, "end": v(-159.99, -8.5) * mm});
            skArc(sketch, "E1600", {"start": v(-157.13, -9) * mm, "mid": v(-157.28, -8.65) * mm, "end": v(-157.64, -8.5) * mm});
            skLineSegment(sketch, "E1601", {"start": v(-157.13, -9) * mm, "end": v(-157.13, -9.5) * mm});
            skArc(sketch, "E1602", {"start": v(-157.64, -10) * mm, "mid": v(-157.28, -9.85) * mm, "end": v(-157.13, -9.5) * mm});
            skLineSegment(sketch, "E1603", {"start": v(-163, -10) * mm, "end": v(-157.64, -10) * mm});
            skArc(sketch, "E1604", {"start": v(-164.5, -8.5) * mm, "mid": v(-164.06, -9.56) * mm, "end": v(-163, -10) * mm});
            skLineSegment(sketch, "E1605", {"start": v(-164.5, -8.5) * mm, "end": v(-164.5, -3.14) * mm});
            skArc(sketch, "E1606", {"start": v(-164, -2.63) * mm, "mid": v(-164.35, -2.78) * mm, "end": v(-164.5, -3.14) * mm});
            skLineSegment(sketch, "E1607", {"start": v(-164, -2.63) * mm, "end": v(-163.5, -2.63) * mm});
            skArc(sketch, "E1608", {"start": v(-163, -3.14) * mm, "mid": v(-163.15, -2.78) * mm, "end": v(-163.5, -2.63) * mm});
            skLineSegment(sketch, "E1609", {"start": v(-163, -5.49) * mm, "end": v(-163, -3.14) * mm});
            skArc(sketch, "E1610", {"start": v(-163, -5.49) * mm, "mid": v(-162.85, -5.85) * mm, "end": v(-162.5, -6) * mm});
            skLineSegment(sketch, "E1611", {"start": v(-161.77, -6) * mm, "end": v(-162.5, -6) * mm});
            skArc(sketch, "E1612", {"start": v(-161.77, -6) * mm, "mid": v(-161.57, -5.96) * mm, "end": v(-161.4, -5.85) * mm});
            skLineSegment(sketch, "E1613", {"start": v(-158.3, -2.74) * mm, "end": v(-161.4, -5.85) * mm});
            skArc(sketch, "E1614", {"start": v(-158.3, -2.74) * mm, "mid": v(-158.2, -2.58) * mm, "end": v(-158.16, -2.38) * mm});
            skLineSegment(sketch, "E1615", {"start": v(-158.16, 2.38) * mm, "end": v(-158.16, -2.38) * mm});
            skArc(sketch, "E1616", {"start": v(-158.16, 2.38) * mm, "mid": v(-158.2, 2.58) * mm, "end": v(-158.3, 2.74) * mm});
            skLineSegment(sketch, "E1617", {"start": v(-158.3, 2.74) * mm, "end": v(-161.4, 5.85) * mm});
            skArc(sketch, "E1618", {"start": v(-161.4, 5.85) * mm, "mid": v(-161.57, 5.96) * mm, "end": v(-161.77, 6) * mm});
            skLineSegment(sketch, "E1619", {"start": v(-161.77, 6) * mm, "end": v(-162.5, 6) * mm});
            skArc(sketch, "E1620", {"start": v(-162.5, 6) * mm, "mid": v(-162.85, 5.85) * mm, "end": v(-163, 5.49) * mm});
            skLineSegment(sketch, "E1621", {"start": v(-163, 5.49) * mm, "end": v(-163, 3.14) * mm});
            skArc(sketch, "E1622", {"start": v(-163.5, 2.63) * mm, "mid": v(-163.15, 2.78) * mm, "end": v(-163, 3.14) * mm});
            skLineSegment(sketch, "E1623", {"start": v(-163.5, 2.63) * mm, "end": v(-164, 2.63) * mm});
            skArc(sketch, "E1624", {"start": v(-164.5, 3.14) * mm, "mid": v(-164.35, 2.78) * mm, "end": v(-164, 2.63) * mm});
            skLineSegment(sketch, "E1625", {"start": v(-164.5, 3.14) * mm, "end": v(-164.5, 8.5) * mm});
            skArc(sketch, "E1626", {"start": v(-163, 10) * mm, "mid": v(-164.06, 9.56) * mm, "end": v(-164.5, 8.5) * mm});
            skLineSegment(sketch, "E1627", {"start": v(-163, 10) * mm, "end": v(-157.64, 10) * mm});
            skArc(sketch, "E1628", {"start": v(-157.13, 9.5) * mm, "mid": v(-157.28, 9.85) * mm, "end": v(-157.64, 10) * mm});
            skLineSegment(sketch, "E1629", {"start": v(-157.13, 9.5) * mm, "end": v(-157.13, 9) * mm});
            skArc(sketch, "E1630", {"start": v(-157.64, 8.5) * mm, "mid": v(-157.28, 8.65) * mm, "end": v(-157.13, 9) * mm});
            skLineSegment(sketch, "E1631", {"start": v(-157.64, 8.5) * mm, "end": v(-159.99, 8.5) * mm});
            skArc(sketch, "E1632", {"start": v(-159.99, 8.5) * mm, "mid": v(-160.35, 8.35) * mm, "end": v(-160.5, 8) * mm});
            skLineSegment(sketch, "E1633", {"start": v(-160.5, 8) * mm, "end": v(-160.5, 7.27) * mm});
            skArc(sketch, "E1634", {"start": v(-160.5, 7.27) * mm, "mid": v(-160.46, 7.07) * mm, "end": v(-160.35, 6.9) * mm});
            skLineSegment(sketch, "E1635", {"start": v(-160.35, 6.9) * mm, "end": v(-157.24, 3.8) * mm});
            skArc(sketch, "E1636", {"start": v(-157.24, 3.8) * mm, "mid": v(-157.08, 3.7) * mm, "end": v(-156.88, 3.66) * mm});
            skLineSegment(sketch, "E1637", {"start": v(-156.88, 3.65) * mm, "end": v(-152.12, 3.65) * mm});
            skArc(sketch, "E1638", {"start": v(-152.12, 3.66) * mm, "mid": v(-151.92, 3.7) * mm, "end": v(-151.76, 3.8) * mm});
            skLineSegment(sketch, "E1639", {"start": v(-151.76, 3.8) * mm, "end": v(-148.65, 6.9) * mm});
            skArc(sketch, "E1640", {"start": v(-148.65, 6.9) * mm, "mid": v(-148.54, 7.07) * mm, "end": v(-148.5, 7.27) * mm});
            skLineSegment(sketch, "E1641", {"start": v(-148.5, 8) * mm, "end": v(-148.5, 7.27) * mm});
            skArc(sketch, "E1642", {"start": v(-148.5, 8) * mm, "mid": v(-148.65, 8.35) * mm, "end": v(-149.01, 8.5) * mm});
            skLineSegment(sketch, "E1643", {"start": v(-149.01, 8.5) * mm, "end": v(-151.36, 8.5) * mm});
            skArc(sketch, "E1644", {"start": v(-151.87, 9) * mm, "mid": v(-151.72, 8.65) * mm, "end": v(-151.36, 8.5) * mm});
            skLineSegment(sketch, "E1645", {"start": v(-151.87, 9) * mm, "end": v(-151.87, 9.5) * mm});
            skArc(sketch, "E1646", {"start": v(-151.36, 10) * mm, "mid": v(-151.72, 9.85) * mm, "end": v(-151.87, 9.5) * mm});
            skLineSegment(sketch, "E1647", {"start": v(-137.64, 10) * mm, "end": v(-151.36, 10) * mm});
            skArc(sketch, "E1648", {"start": v(-137.64, 10) * mm, "mid": v(-137.28, 9.85) * mm, "end": v(-137.13, 9.5) * mm});
            skLineSegment(sketch, "E1649", {"start": v(-137.13, 9) * mm, "end": v(-137.13, 9.5) * mm});
            skArc(sketch, "E1650", {"start": v(-137.13, 9) * mm, "mid": v(-137.28, 8.65) * mm, "end": v(-137.64, 8.5) * mm});
            skLineSegment(sketch, "E1651", {"start": v(-139.99, 8.5) * mm, "end": v(-137.64, 8.5) * mm});
            skArc(sketch, "E1652", {"start": v(-140.5, 8) * mm, "mid": v(-140.35, 8.35) * mm, "end": v(-139.99, 8.5) * mm});
            skLineSegment(sketch, "E1653", {"start": v(-140.5, 8) * mm, "end": v(-140.5, 7.27) * mm});
            skArc(sketch, "E1654", {"start": v(-140.35, 6.9) * mm, "mid": v(-140.46, 7.07) * mm, "end": v(-140.5, 7.27) * mm});
            skLineSegment(sketch, "E1655", {"start": v(-137.24, 3.8) * mm, "end": v(-140.35, 6.9) * mm});
            skArc(sketch, "E1656", {"start": v(-136.88, 3.66) * mm, "mid": v(-137.08, 3.7) * mm, "end": v(-137.24, 3.8) * mm});
            skLineSegment(sketch, "E1657", {"start": v(-132.12, 3.65) * mm, "end": v(-136.88, 3.65) * mm});
            skArc(sketch, "E1658", {"start": v(-131.76, 3.8) * mm, "mid": v(-131.92, 3.7) * mm, "end": v(-132.12, 3.66) * mm});
            skLineSegment(sketch, "E1659", {"start": v(-128.65, 6.9) * mm, "end": v(-131.76, 3.8) * mm});
            skArc(sketch, "E1660", {"start": v(-128.5, 7.27) * mm, "mid": v(-128.54, 7.07) * mm, "end": v(-128.65, 6.9) * mm});
            skLineSegment(sketch, "E1661", {"start": v(-128.5, 8) * mm, "end": v(-128.5, 7.27) * mm});
            skArc(sketch, "E1662", {"start": v(-129.01, 8.5) * mm, "mid": v(-128.65, 8.35) * mm, "end": v(-128.5, 8) * mm});
            skLineSegment(sketch, "E1663", {"start": v(-131.36, 8.5) * mm, "end": v(-129.01, 8.5) * mm});
            skArc(sketch, "E1664", {"start": v(-131.36, 8.5) * mm, "mid": v(-131.72, 8.65) * mm, "end": v(-131.87, 9) * mm});
            skLineSegment(sketch, "E1665", {"start": v(-131.87, 9.5) * mm, "end": v(-131.87, 9) * mm});
            skArc(sketch, "E1666", {"start": v(-131.87, 9.5) * mm, "mid": v(-131.72, 9.85) * mm, "end": v(-131.36, 10) * mm});
            skLineSegment(sketch, "E1667", {"start": v(-126, 10) * mm, "end": v(-131.36, 10) * mm});
            skArc(sketch, "E1668", {"start": v(-126, 10) * mm, "mid": v(-124.94, 9.56) * mm, "end": v(-124.5, 8.5) * mm});
            skLineSegment(sketch, "E1669", {"start": v(-124.5, 3.14) * mm, "end": v(-124.5, 8.5) * mm});
            skArc(sketch, "E1670", {"start": v(-124.5, 3.14) * mm, "mid": v(-124.65, 2.78) * mm, "end": v(-125, 2.63) * mm});
            skLineSegment(sketch, "E1671", {"start": v(-125.5, 2.63) * mm, "end": v(-125, 2.63) * mm});
            skArc(sketch, "E1672", {"start": v(-125.5, 2.63) * mm, "mid": v(-125.85, 2.78) * mm, "end": v(-126, 3.14) * mm});
            skLineSegment(sketch, "E1673", {"start": v(-126, 5.49) * mm, "end": v(-126, 3.14) * mm});
            skArc(sketch, "E1674", {"start": v(-126.5, 6) * mm, "mid": v(-126.15, 5.85) * mm, "end": v(-126, 5.49) * mm});
            skLineSegment(sketch, "E1675", {"start": v(-127.23, 6) * mm, "end": v(-126.5, 6) * mm});
            skArc(sketch, "E1676", {"start": v(-127.6, 5.85) * mm, "mid": v(-127.43, 5.96) * mm, "end": v(-127.23, 6) * mm});
            skLineSegment(sketch, "E1677", {"start": v(-130.7, 2.74) * mm, "end": v(-127.6, 5.85) * mm});
            skArc(sketch, "E1678", {"start": v(-130.85, 2.38) * mm, "mid": v(-130.8, 2.58) * mm, "end": v(-130.7, 2.74) * mm});
            skLineSegment(sketch, "E1679", {"start": v(-130.85, 2.38) * mm, "end": v(-130.85, -2.38) * mm});
            skArc(sketch, "E1680", {"start": v(-130.7, -2.74) * mm, "mid": v(-130.8, -2.58) * mm, "end": v(-130.85, -2.38) * mm});
            skLineSegment(sketch, "E1681", {"start": v(-130.7, -2.74) * mm, "end": v(-127.6, -5.85) * mm});
            skArc(sketch, "E1682", {"start": v(-127.23, -6) * mm, "mid": v(-127.43, -5.96) * mm, "end": v(-127.6, -5.85) * mm});
            skLineSegment(sketch, "E1683", {"start": v(-127.23, -6) * mm, "end": v(-126.5, -6) * mm});
            skArc(sketch, "E1684", {"start": v(-126, -5.49) * mm, "mid": v(-126.15, -5.85) * mm, "end": v(-126.5, -6) * mm});
            skLineSegment(sketch, "E1685", {"start": v(-126, -5.49) * mm, "end": v(-126, -3.14) * mm});
            skArc(sketch, "E1686", {"start": v(-126, -3.14) * mm, "mid": v(-125.85, -2.78) * mm, "end": v(-125.5, -2.63) * mm});
            skLineSegment(sketch, "E1687", {"start": v(-125, -2.63) * mm, "end": v(-125.5, -2.63) * mm});
            skArc(sketch, "E1688", {"start": v(-125, -2.63) * mm, "mid": v(-124.65, -2.78) * mm, "end": v(-124.5, -3.14) * mm});
            skLineSegment(sketch, "E1689", {"start": v(-124.5, -8.5) * mm, "end": v(-124.5, -3.14) * mm});
            skArc(sketch, "E1690", {"start": v(-124.5, -8.5) * mm, "mid": v(-124.94, -9.56) * mm, "end": v(-126, -10) * mm});
            skLineSegment(sketch, "E1691", {"start": v(-126, -10) * mm, "end": v(-131.36, -10) * mm});
            skArc(sketch, "E1692", {"start": v(-131.36, -10) * mm, "mid": v(-131.72, -9.85) * mm, "end": v(-131.87, -9.5) * mm});
            skArc(sketch, "E1693", {"start": v(-138.16, 2.38) * mm, "mid": v(-138.2, 2.58) * mm, "end": v(-138.3, 2.74) * mm});
            skLineSegment(sketch, "E1694", {"start": v(-138.3, 2.74) * mm, "end": v(-141.85, 6.29) * mm});
            skArc(sketch, "E1695", {"start": v(-141.85, 6.29) * mm, "mid": v(-141.96, 6.45) * mm, "end": v(-142, 6.64) * mm});
            skLineSegment(sketch, "E1696", {"start": v(-142, 8) * mm, "end": v(-142, 6.64) * mm});
            skArc(sketch, "E1697", {"start": v(-142.5, 8.5) * mm, "mid": v(-142.14, 8.35) * mm, "end": v(-142, 8) * mm});
            skLineSegment(sketch, "E1698", {"start": v(-146.5, 8.5) * mm, "end": v(-142.5, 8.5) * mm});
            skArc(sketch, "E1699", {"start": v(-146.5, 8.5) * mm, "mid": v(-146.86, 8.35) * mm, "end": v(-147, 8) * mm});
            skLineSegment(sketch, "E1700", {"start": v(-147, 8) * mm, "end": v(-147, 6.64) * mm});
            skArc(sketch, "E1701", {"start": v(-147.15, 6.29) * mm, "mid": v(-147.04, 6.45) * mm, "end": v(-147, 6.64) * mm});
            skLineSegment(sketch, "E1702", {"start": v(-150.7, 2.74) * mm, "end": v(-147.15, 6.29) * mm});
            skArc(sketch, "E1703", {"start": v(-150.7, 2.74) * mm, "mid": v(-150.8, 2.58) * mm, "end": v(-150.85, 2.38) * mm});
            skLineSegment(sketch, "E1704", {"start": v(-150.85, 2.38) * mm, "end": v(-150.85, -2.38) * mm});
            skArc(sketch, "E1705", {"start": v(-150.85, -2.38) * mm, "mid": v(-150.8, -2.58) * mm, "end": v(-150.7, -2.74) * mm});
            skLineSegment(sketch, "E1706", {"start": v(-150.7, -2.74) * mm, "end": v(-147.15, -6.29) * mm});
            skArc(sketch, "E1707", {"start": v(-147, -6.64) * mm, "mid": v(-147.04, -6.45) * mm, "end": v(-147.15, -6.29) * mm});
            skLineSegment(sketch, "E1708", {"start": v(-147, -6.64) * mm, "end": v(-147, -8) * mm});
            skArc(sketch, "E1709", {"start": v(-147, -8) * mm, "mid": v(-146.86, -8.35) * mm, "end": v(-146.5, -8.5) * mm});
            skLineSegment(sketch, "E1710", {"start": v(-146.5, -8.5) * mm, "end": v(-142.5, -8.5) * mm});
            skArc(sketch, "E1711", {"start": v(-142, -8) * mm, "mid": v(-142.14, -8.35) * mm, "end": v(-142.5, -8.5) * mm});
            skLineSegment(sketch, "E1712", {"start": v(-142, -6.64) * mm, "end": v(-142, -8) * mm});
            skArc(sketch, "E1713", {"start": v(-142, -6.64) * mm, "mid": v(-141.96, -6.45) * mm, "end": v(-141.85, -6.29) * mm});
            skLineSegment(sketch, "E1714", {"start": v(-138.3, -2.74) * mm, "end": v(-141.85, -6.29) * mm});
            skArc(sketch, "E1715", {"start": v(-138.16, -2.38) * mm, "mid": v(-138.2, -2.58) * mm, "end": v(-138.3, -2.74) * mm});
            skSolve(sketch);
        }
        {
            var Q0;
            Q0 = qSketchRegion(id + "F12", true);
            extrude(context, id + "F13", {"entities" : qUnion([Q0]), "depth" : 996 * mm, "offsetDistance" : 25 * mm});
        }
        {
            var Q0;
            Q0=qCreatedBy(makeId("Top.planeOp"),FACE);
            var sketch = newSketch(context, id + "F14", { "sketchPlane" : qUnion([Q0])});
            skLineSegment(sketch, "E1716", {"start": v(-647.7, -163.35) * mm, "end": v(-650.2, -163.35) * mm});
            skLineSegment(sketch, "E1717", {"start": v(-653.48, -166.62) * mm, "end": v(-653.48, -167.35) * mm});
            skLineSegment(sketch, "E1718", {"start": v(-653.48, -167.35) * mm, "end": v(-649.7, -167.35) * mm});
            skLineSegment(sketch, "E1719", {"start": v(-649.7, -167.35) * mm, "end": v(-649.7, -168.35) * mm});
            skLineSegment(sketch, "E1720", {"start": v(-652.27, -168.85) * mm, "end": v(-655.2, -168.85) * mm});
            skLineSegment(sketch, "E1721", {"start": v(-647.7, -163.35) * mm, "end": v(-646.7, -162.85) * mm});
            skLineSegment(sketch, "E1722", {"start": v(-649.7, -168.35) * mm, "end": v(-650.2, -168.35) * mm});
            skLineSegment(sketch, "E1723", {"start": v(-650.2, -168.35) * mm, "end": v(-650.2, -168.85) * mm, "construction": true});
            skArc(sketch, "E1724.filletArc", {"start": v(-656.27, -168.4) * mm, "mid": v(-655.78, -168.73) * mm, "end": v(-655.2, -168.85) * mm});
            skLineSegment(sketch, "E1725", {"start": v(-650.2, -168.85) * mm, "end": v(-652.27, -168.85) * mm});
            skPoint(sketch, "E1726.orphan", {"position": v(-646.7, -168.85) * mm});
            skLineSegment(sketch, "E1727.trimOffspring", {"start": v(-655.2, -167.35) * mm, "end": v(-648.65, -160.8) * mm});
            skPoint(sketch, "E1728", {"position": v(-646.7, -163.35) * mm});
            skLineSegment(sketch, "E1729", {"start": v(-650.2, -163.35) * mm, "end": v(-653.48, -166.62) * mm});
            skArc(sketch, "E1730", {"start": v(-648.65, -160.8) * mm, "mid": v(-647.76, -161.39) * mm, "end": v(-646.7, -161.6) * mm});
            skPoint(sketch, "E1731", {"position": v(-648.65, -160.8) * mm});
            skLineSegment(sketch, "E1732", {"start": v(-646.7, -162.85) * mm, "end": v(-646.7, -161.6) * mm});
            skLineSegment(sketch, "E1733", {"start": v(-656.27, -168.4) * mm, "end": v(-655.2, -167.35) * mm});
            skPoint(sketch, "E1734", {"position": v(-652.27, -168.85) * mm});
            skLineSegment(sketch, "E1735", {"start": v(-650.2, -168.35) * mm, "end": v(-650.2, -168.85) * mm});
            skPoint(sketch, "E1736.0.MirrorP", {"position": v(-656.7, -164.41) * mm});
            skPoint(sketch, "E1736.1.MirrorP", {"position": v(-656.7, -164.41) * mm});
            skPoint(sketch, "E1736.2.MirrorP", {"position": v(-656.7, -164.41) * mm});
            skPoint(sketch, "E1736.3.MirrorP", {"position": v(-656.7, -164.41) * mm});
            skPoint(sketch, "E1736.4.MirrorP", {"position": v(-656.7, -164.41) * mm});
            skPoint(sketch, "E1736.5.MirrorP", {"position": v(-656.7, -164.41) * mm});
            skPoint(sketch, "E1736.6.MirrorP", {"position": v(-656.7, -164.41) * mm});
            skPoint(sketch, "E1736.7.MirrorP", {"position": v(-656.7, -164.41) * mm});
            skPoint(sketch, "E1736.8.MirrorP", {"position": v(-656.7, -164.41) * mm});
            skPoint(sketch, "E1736.9.MirrorP", {"position": v(-656.7, -164.41) * mm});
            skPoint(sketch, "E1736.10.MirrorP", {"position": v(-656.7, -164.41) * mm});
            skLineSegment(sketch, "E1736.11.MirrorCS", {"start": v(-656.2, -162.35) * mm, "end": v(-656.7, -162.35) * mm, "construction": true});
            skPoint(sketch, "E1736.12.MirrorP", {"position": v(-656.7, -164.41) * mm});
            skLineSegment(sketch, "E1736.13.MirrorCS", {"start": v(-656.2, -162.35) * mm, "end": v(-656.7, -162.35) * mm});
            skLineSegment(sketch, "E1736.14.MirrorCS", {"start": v(-654.48, -165.62) * mm, "end": v(-655.2, -165.62) * mm});
            skPoint(sketch, "E1736.15.MirrorP", {"position": v(-656.7, -164.41) * mm});
            skLineSegment(sketch, "E1736.16.MirrorCS", {"start": v(-656.2, -161.85) * mm, "end": v(-656.2, -162.35) * mm});
            skPoint(sketch, "E1736.17.MirrorP", {"position": v(-656.7, -158.85) * mm});
            skLineSegment(sketch, "E1736.18.MirrorCS", {"start": v(-656.7, -164.41) * mm, "end": v(-656.7, -167.35) * mm});
            skArc(sketch, "E1736.19.MirrorCS", {"start": v(-648.65, -160.8) * mm, "mid": v(-649.25, -159.9) * mm, "end": v(-649.46, -158.85) * mm});
            skPoint(sketch, "E1736.20.MirrorP", {"position": v(-651.2, -158.85) * mm});
            skLineSegment(sketch, "E1736.21.MirrorCS", {"start": v(-651.2, -162.35) * mm, "end": v(-654.48, -165.62) * mm});
            skLineSegment(sketch, "E1736.23.MirrorCS", {"start": v(-651.2, -159.85) * mm, "end": v(-651.2, -162.35) * mm});
            skLineSegment(sketch, "E1736.24.MirrorCS", {"start": v(-655.2, -165.62) * mm, "end": v(-655.2, -161.85) * mm});
            skLineSegment(sketch, "E1736.25.MirrorCS", {"start": v(-656.7, -162.35) * mm, "end": v(-656.7, -164.41) * mm});
            skLineSegment(sketch, "E1736.26.MirrorCS", {"start": v(-650.7, -158.85) * mm, "end": v(-649.46, -158.85) * mm});
            skArc(sketch, "E1736.28.MirrorCS", {"start": v(-656.27, -168.4) * mm, "mid": v(-656.6, -167.92) * mm, "end": v(-656.7, -167.35) * mm});
            skLineSegment(sketch, "E1736.29.MirrorCS", {"start": v(-651.2, -159.85) * mm, "end": v(-650.7, -158.85) * mm});
            skLineSegment(sketch, "E1736.30.MirrorCS", {"start": v(-656.7, -164.41) * mm, "end": v(-656.7, -167.35) * mm});
            skPoint(sketch, "E1736.31.MirrorP", {"position": v(-656.7, -164.41) * mm});
            skLineSegment(sketch, "E1736.32.MirrorCS", {"start": v(-655.2, -161.85) * mm, "end": v(-656.2, -161.85) * mm});
            skPoint(sketch, "E1737.0.MirrorP", {"position": v(-652.27, -148.85) * mm});
            skPoint(sketch, "E1737.1.MirrorP", {"position": v(-656.7, -153.28) * mm});
            skPoint(sketch, "E1737.2.MirrorP", {"position": v(-652.27, -148.85) * mm});
            skPoint(sketch, "E1737.3.MirrorP", {"position": v(-656.7, -153.28) * mm});
            skPoint(sketch, "E1737.4.MirrorP", {"position": v(-652.27, -148.85) * mm});
            skPoint(sketch, "E1737.5.MirrorP", {"position": v(-656.7, -153.28) * mm});
            skPoint(sketch, "E1737.6.MirrorP", {"position": v(-656.7, -153.28) * mm});
            skPoint(sketch, "E1737.7.MirrorP", {"position": v(-652.27, -148.85) * mm});
            skPoint(sketch, "E1737.8.MirrorP", {"position": v(-652.27, -148.85) * mm});
            skPoint(sketch, "E1737.9.MirrorP", {"position": v(-656.7, -153.28) * mm});
            skPoint(sketch, "E1737.10.MirrorP", {"position": v(-652.27, -148.85) * mm});
            skPoint(sketch, "E1737.11.MirrorP", {"position": v(-656.7, -153.28) * mm});
            skPoint(sketch, "E1737.12.MirrorP", {"position": v(-652.27, -148.85) * mm});
            skPoint(sketch, "E1737.13.MirrorP", {"position": v(-656.7, -153.28) * mm});
            skPoint(sketch, "E1737.14.MirrorP", {"position": v(-652.27, -148.85) * mm});
            skPoint(sketch, "E1737.15.MirrorP", {"position": v(-656.7, -153.28) * mm});
            skPoint(sketch, "E1737.16.MirrorP", {"position": v(-652.27, -148.85) * mm});
            skPoint(sketch, "E1737.17.MirrorP", {"position": v(-656.7, -153.28) * mm});
            skLineSegment(sketch, "E1737.18.MirrorCS", {"start": v(-656.2, -155.35) * mm, "end": v(-656.7, -155.35) * mm, "construction": true});
            skPoint(sketch, "E1737.19.MirrorP", {"position": v(-652.27, -148.85) * mm});
            skPoint(sketch, "E1737.20.MirrorP", {"position": v(-656.7, -153.28) * mm});
            skLineSegment(sketch, "E1737.21.MirrorCS", {"start": v(-650.2, -149.35) * mm, "end": v(-650.2, -148.85) * mm, "construction": true});
            skLineSegment(sketch, "E1737.22.MirrorCS", {"start": v(-650.2, -149.35) * mm, "end": v(-650.2, -148.85) * mm});
            skPoint(sketch, "E1737.23.MirrorP", {"position": v(-652.27, -148.85) * mm});
            skLineSegment(sketch, "E1737.24.MirrorCS", {"start": v(-656.2, -155.35) * mm, "end": v(-656.7, -155.35) * mm});
            skPoint(sketch, "E1737.25.MirrorP", {"position": v(-656.7, -153.28) * mm});
            skPoint(sketch, "E1737.26.MirrorP", {"position": v(-652.27, -148.85) * mm});
            skPoint(sketch, "E1737.27.MirrorP", {"position": v(-656.7, -153.28) * mm});
            skLineSegment(sketch, "E1737.28.MirrorCS", {"start": v(-649.7, -149.35) * mm, "end": v(-650.2, -149.35) * mm});
            skLineSegment(sketch, "E1737.29.MirrorCS", {"start": v(-656.2, -155.85) * mm, "end": v(-656.2, -155.35) * mm});
            skLineSegment(sketch, "E1737.30.MirrorCS", {"start": v(-655.2, -155.85) * mm, "end": v(-656.2, -155.85) * mm});
            skPoint(sketch, "E1737.31.MirrorP", {"position": v(-652.27, -148.85) * mm});
            skPoint(sketch, "E1737.32.MirrorP", {"position": v(-656.7, -153.28) * mm});
            skLineSegment(sketch, "E1737.34.MirrorCS", {"start": v(-656.7, -155.35) * mm, "end": v(-656.7, -153.28) * mm});
            skArc(sketch, "E1737.35.MirrorCS", {"start": v(-656.27, -149.29) * mm, "mid": v(-656.6, -149.77) * mm, "end": v(-656.7, -150.35) * mm});
            skLineSegment(sketch, "E1737.36.MirrorCS", {"start": v(-655.2, -152.08) * mm, "end": v(-655.2, -155.85) * mm});
            skLineSegment(sketch, "E1737.37.MirrorCS", {"start": v(-651.2, -157.85) * mm, "end": v(-650.7, -158.85) * mm});
            skLineSegment(sketch, "E1737.38.MirrorCS", {"start": v(-656.7, -153.28) * mm, "end": v(-656.7, -150.35) * mm});
            skLineSegment(sketch, "E1737.40.MirrorCS", {"start": v(-651.2, -155.35) * mm, "end": v(-654.48, -152.08) * mm});
            skLineSegment(sketch, "E1737.41.MirrorCS", {"start": v(-651.2, -157.85) * mm, "end": v(-651.2, -155.35) * mm});
            skLineSegment(sketch, "E1737.42.MirrorCS", {"start": v(-647.7, -154.35) * mm, "end": v(-650.2, -154.35) * mm});
            skLineSegment(sketch, "E1737.43.MirrorCS", {"start": v(-653.48, -150.35) * mm, "end": v(-649.7, -150.35) * mm});
            skLineSegment(sketch, "E1737.44.MirrorCS", {"start": v(-653.48, -151.08) * mm, "end": v(-653.48, -150.35) * mm});
            skLineSegment(sketch, "E1737.45.MirrorCS", {"start": v(-652.27, -148.85) * mm, "end": v(-655.2, -148.85) * mm});
            skLineSegment(sketch, "E1737.46.MirrorCS", {"start": v(-649.7, -150.35) * mm, "end": v(-649.7, -149.35) * mm});
            skLineSegment(sketch, "E1737.47.MirrorCS", {"start": v(-647.7, -154.35) * mm, "end": v(-646.7, -154.85) * mm});
            skLineSegment(sketch, "E1737.48.MirrorCS", {"start": v(-652.27, -148.85) * mm, "end": v(-655.2, -148.85) * mm});
            skLineSegment(sketch, "E1737.49.MirrorCS", {"start": v(-650.2, -148.85) * mm, "end": v(-652.27, -148.85) * mm});
            skArc(sketch, "E1737.50.MirrorCS", {"start": v(-656.27, -149.29) * mm, "mid": v(-655.78, -148.96) * mm, "end": v(-655.2, -148.85) * mm});
            skLineSegment(sketch, "E1737.51.MirrorCS", {"start": v(-650.2, -154.35) * mm, "end": v(-653.48, -151.08) * mm});
            skLineSegment(sketch, "E1737.52.MirrorCS", {"start": v(-655.2, -150.35) * mm, "end": v(-648.65, -156.9) * mm});
            skLineSegment(sketch, "E1737.53.MirrorCS", {"start": v(-656.27, -149.29) * mm, "end": v(-655.2, -150.35) * mm});
            skLineSegment(sketch, "E1737.54.MirrorCS", {"start": v(-656.27, -149.29) * mm, "end": v(-655.2, -150.35) * mm});
            skLineSegment(sketch, "E1737.55.MirrorCS", {"start": v(-646.7, -154.85) * mm, "end": v(-646.7, -156.1) * mm});
            skArc(sketch, "E1737.56.MirrorCS", {"start": v(-648.65, -156.9) * mm, "mid": v(-647.76, -156.3) * mm, "end": v(-646.7, -156.1) * mm});
            skPoint(sketch, "E1737.58.MirrorP", {"position": v(-646.7, -154.35) * mm});
            skLineSegment(sketch, "E1737.59.MirrorCS", {"start": v(-654.48, -152.08) * mm, "end": v(-655.2, -152.08) * mm});
            skPoint(sketch, "E1737.60.MirrorP", {"position": v(-652.27, -148.85) * mm});
            skArc(sketch, "E1737.61.MirrorCS", {"start": v(-648.65, -156.9) * mm, "mid": v(-649.25, -157.8) * mm, "end": v(-649.46, -158.85) * mm});
            skPoint(sketch, "E1737.62.MirrorP", {"position": v(-646.7, -148.85) * mm});
            skPoint(sketch, "E1737.63.MirrorP", {"position": v(-648.65, -156.9) * mm});
            skPoint(sketch, "E1737.64.MirrorP", {"position": v(-648.65, -156.9) * mm});
            skLineSegment(sketch, "E1737.65.MirrorCS", {"start": v(-656.7, -153.28) * mm, "end": v(-656.7, -150.35) * mm});
            skPoint(sketch, "E1737.66.MirrorP", {"position": v(-656.7, -153.28) * mm});
            skPoint(sketch, "E1738.0.MirrorP", {"position": v(-636.7, -153.28) * mm});
            skPoint(sketch, "E1738.1.MirrorP", {"position": v(-641.15, -168.85) * mm});
            skPoint(sketch, "E1738.2.MirrorP", {"position": v(-641.15, -148.85) * mm});
            skPoint(sketch, "E1738.3.MirrorP", {"position": v(-636.7, -153.28) * mm});
            skPoint(sketch, "E1738.4.MirrorP", {"position": v(-636.7, -164.41) * mm});
            skPoint(sketch, "E1738.5.MirrorP", {"position": v(-641.15, -168.85) * mm});
            skPoint(sketch, "E1738.6.MirrorP", {"position": v(-641.15, -168.85) * mm});
            skPoint(sketch, "E1738.7.MirrorP", {"position": v(-636.7, -153.28) * mm});
            skPoint(sketch, "E1738.8.MirrorP", {"position": v(-641.15, -148.85) * mm});
            skPoint(sketch, "E1738.9.MirrorP", {"position": v(-636.7, -164.41) * mm});
            skPoint(sketch, "E1738.10.MirrorP", {"position": v(-636.7, -153.28) * mm});
            skPoint(sketch, "E1738.11.MirrorP", {"position": v(-641.15, -168.85) * mm});
            skPoint(sketch, "E1738.12.MirrorP", {"position": v(-641.15, -148.85) * mm});
            skPoint(sketch, "E1738.13.MirrorP", {"position": v(-636.7, -164.41) * mm});
            skPoint(sketch, "E1738.14.MirrorP", {"position": v(-636.7, -153.28) * mm});
            skPoint(sketch, "E1738.15.MirrorP", {"position": v(-641.15, -168.85) * mm});
            skPoint(sketch, "E1738.16.MirrorP", {"position": v(-636.7, -164.41) * mm});
            skPoint(sketch, "E1738.17.MirrorP", {"position": v(-641.15, -148.85) * mm});
            skPoint(sketch, "E1738.18.MirrorP", {"position": v(-641.15, -168.85) * mm});
            skPoint(sketch, "E1738.19.MirrorP", {"position": v(-641.15, -148.85) * mm});
            skPoint(sketch, "E1738.20.MirrorP", {"position": v(-636.7, -153.28) * mm});
            skPoint(sketch, "E1738.21.MirrorP", {"position": v(-636.7, -164.41) * mm});
            skPoint(sketch, "E1738.22.MirrorP", {"position": v(-636.7, -164.41) * mm});
            skPoint(sketch, "E1738.23.MirrorP", {"position": v(-641.15, -168.85) * mm});
            skPoint(sketch, "E1738.24.MirrorP", {"position": v(-636.7, -153.28) * mm});
            skPoint(sketch, "E1738.25.MirrorP", {"position": v(-641.15, -148.85) * mm});
            skPoint(sketch, "E1738.26.MirrorP", {"position": v(-636.7, -164.41) * mm});
            skPoint(sketch, "E1738.27.MirrorP", {"position": v(-636.7, -153.28) * mm});
            skPoint(sketch, "E1738.28.MirrorP", {"position": v(-641.15, -168.85) * mm});
            skPoint(sketch, "E1738.29.MirrorP", {"position": v(-641.15, -148.85) * mm});
            skPoint(sketch, "E1738.30.MirrorP", {"position": v(-636.7, -164.41) * mm});
            skPoint(sketch, "E1738.31.MirrorP", {"position": v(-641.15, -148.85) * mm});
            skPoint(sketch, "E1738.32.MirrorP", {"position": v(-641.15, -168.85) * mm});
            skPoint(sketch, "E1738.33.MirrorP", {"position": v(-636.7, -153.28) * mm});
            skPoint(sketch, "E1738.34.MirrorP", {"position": v(-636.7, -153.28) * mm});
            skPoint(sketch, "E1738.35.MirrorP", {"position": v(-641.15, -148.85) * mm});
            skPoint(sketch, "E1738.36.MirrorP", {"position": v(-636.7, -164.41) * mm});
            skPoint(sketch, "E1738.37.MirrorP", {"position": v(-641.15, -168.85) * mm});
            skLineSegment(sketch, "E1738.38.MirrorCS", {"start": v(-643.2, -149.35) * mm, "end": v(-643.2, -148.85) * mm, "construction": true});
            skLineSegment(sketch, "E1738.39.MirrorCS", {"start": v(-637.2, -155.35) * mm, "end": v(-636.7, -155.35) * mm, "construction": true});
            skLineSegment(sketch, "E1738.40.MirrorCS", {"start": v(-637.2, -162.35) * mm, "end": v(-636.7, -162.35) * mm, "construction": true});
            skLineSegment(sketch, "E1738.41.MirrorCS", {"start": v(-643.2, -168.35) * mm, "end": v(-643.2, -168.85) * mm, "construction": true});
            skPoint(sketch, "E1738.42.MirrorP", {"position": v(-636.7, -153.28) * mm});
            skPoint(sketch, "E1738.43.MirrorP", {"position": v(-636.7, -164.41) * mm});
            skPoint(sketch, "E1738.44.MirrorP", {"position": v(-641.15, -168.85) * mm});
            skPoint(sketch, "E1738.45.MirrorP", {"position": v(-641.15, -148.85) * mm});
            skLineSegment(sketch, "E1738.46.MirrorCS", {"start": v(-637.2, -155.35) * mm, "end": v(-636.7, -155.35) * mm});
            skLineSegment(sketch, "E1738.47.MirrorCS", {"start": v(-637.2, -161.85) * mm, "end": v(-637.2, -162.35) * mm});
            skLineSegment(sketch, "E1738.48.MirrorCS", {"start": v(-637.2, -162.35) * mm, "end": v(-636.7, -162.35) * mm});
            skLineSegment(sketch, "E1738.49.MirrorCS", {"start": v(-637.15, -168.4) * mm, "end": v(-638.2, -167.35) * mm});
            skLineSegment(sketch, "E1738.50.MirrorCS", {"start": v(-643.7, -168.35) * mm, "end": v(-643.2, -168.35) * mm});
            skPoint(sketch, "E1738.51.MirrorP", {"position": v(-636.7, -164.41) * mm});
            skPoint(sketch, "E1738.52.MirrorP", {"position": v(-636.7, -153.28) * mm});
            skPoint(sketch, "E1738.53.MirrorP", {"position": v(-641.15, -148.85) * mm});
            skPoint(sketch, "E1738.54.MirrorP", {"position": v(-641.15, -168.85) * mm});
            skLineSegment(sketch, "E1738.55.MirrorCS", {"start": v(-643.7, -149.35) * mm, "end": v(-643.2, -149.35) * mm});
            skLineSegment(sketch, "E1738.56.MirrorCS", {"start": v(-637.2, -155.85) * mm, "end": v(-637.2, -155.35) * mm});
            skLineSegment(sketch, "E1738.57.MirrorCS", {"start": v(-643.2, -168.35) * mm, "end": v(-643.2, -168.85) * mm});
            skLineSegment(sketch, "E1738.58.MirrorCS", {"start": v(-643.2, -149.35) * mm, "end": v(-643.2, -148.85) * mm});
            skLineSegment(sketch, "E1738.59.MirrorCS", {"start": v(-643.7, -150.35) * mm, "end": v(-643.7, -149.35) * mm});
            skLineSegment(sketch, "E1738.60.MirrorCS", {"start": v(-639.94, -151.08) * mm, "end": v(-639.94, -150.35) * mm});
            skPoint(sketch, "E1738.61.MirrorP", {"position": v(-641.15, -148.85) * mm});
            skLineSegment(sketch, "E1738.62.MirrorCS", {"start": v(-639.94, -166.62) * mm, "end": v(-639.94, -167.35) * mm});
            skPoint(sketch, "E1738.63.MirrorP", {"position": v(-641.15, -168.85) * mm});
            skPoint(sketch, "E1738.64.MirrorP", {"position": v(-636.7, -164.41) * mm});
            skLineSegment(sketch, "E1738.65.MirrorCS", {"start": v(-637.15, -168.4) * mm, "end": v(-638.2, -167.35) * mm});
            skLineSegment(sketch, "E1738.66.MirrorCS", {"start": v(-638.94, -152.08) * mm, "end": v(-638.2, -152.08) * mm});
            skLineSegment(sketch, "E1738.67.MirrorCS", {"start": v(-645.7, -154.35) * mm, "end": v(-646.7, -154.85) * mm});
            skLineSegment(sketch, "E1738.68.MirrorCS", {"start": v(-642.2, -159.85) * mm, "end": v(-642.7, -158.85) * mm});
            skLineSegment(sketch, "E1738.69.MirrorCS", {"start": v(-642.7, -158.85) * mm, "end": v(-643.96, -158.85) * mm});
            skLineSegment(sketch, "E1738.70.MirrorCS", {"start": v(-645.7, -163.35) * mm, "end": v(-646.7, -162.85) * mm});
            skLineSegment(sketch, "E1738.71.MirrorCS", {"start": v(-636.7, -153.28) * mm, "end": v(-636.7, -150.35) * mm});
            skPoint(sketch, "E1738.72.MirrorP", {"position": v(-636.7, -153.28) * mm});
            skPoint(sketch, "E1738.73.MirrorP", {"position": v(-636.7, -158.85) * mm});
            skLineSegment(sketch, "E1738.74.MirrorCS", {"start": v(-637.15, -149.29) * mm, "end": v(-638.2, -150.35) * mm});
            skLineSegment(sketch, "E1738.75.MirrorCS", {"start": v(-642.2, -157.85) * mm, "end": v(-642.7, -158.85) * mm});
            skLineSegment(sketch, "E1738.76.MirrorCS", {"start": v(-638.94, -165.62) * mm, "end": v(-638.2, -165.62) * mm});
            skLineSegment(sketch, "E1738.78.MirrorCS", {"start": v(-636.7, -153.28) * mm, "end": v(-636.7, -150.35) * mm});
            skLineSegment(sketch, "E1738.79.MirrorCS", {"start": v(-643.2, -168.85) * mm, "end": v(-641.15, -168.85) * mm});
            skLineSegment(sketch, "E1738.80.MirrorCS", {"start": v(-643.7, -167.35) * mm, "end": v(-643.7, -168.35) * mm});
            skLineSegment(sketch, "E1738.81.MirrorCS", {"start": v(-641.15, -168.85) * mm, "end": v(-638.2, -168.85) * mm});
            skPoint(sketch, "E1738.83.MirrorP", {"position": v(-641.15, -168.85) * mm});
            skLineSegment(sketch, "E1738.84.MirrorCS", {"start": v(-638.2, -155.85) * mm, "end": v(-637.2, -155.85) * mm});
            skLineSegment(sketch, "E1738.85.MirrorCS", {"start": v(-643.2, -148.85) * mm, "end": v(-641.15, -148.85) * mm});
            skArc(sketch, "E1738.86.MirrorCS", {"start": v(-644.77, -160.8) * mm, "mid": v(-645.66, -161.39) * mm, "end": v(-646.7, -161.6) * mm});
            skPoint(sketch, "E1738.87.MirrorP", {"position": v(-644.77, -160.8) * mm});
            skPoint(sketch, "E1738.88.MirrorP", {"position": v(-642.2, -158.85) * mm});
            skArc(sketch, "E1738.89.MirrorCS", {"start": v(-637.15, -149.29) * mm, "mid": v(-637.64, -148.96) * mm, "end": v(-638.2, -148.85) * mm});
            skLineSegment(sketch, "E1738.90.MirrorCS", {"start": v(-636.7, -155.35) * mm, "end": v(-636.7, -153.28) * mm});
            skLineSegment(sketch, "E1738.91.MirrorCS", {"start": v(-638.2, -167.35) * mm, "end": v(-644.77, -160.8) * mm});
            skLineSegment(sketch, "E1738.92.MirrorCS", {"start": v(-643.2, -163.35) * mm, "end": v(-639.94, -166.62) * mm});
            skArc(sketch, "E1738.93.MirrorCS", {"start": v(-637.15, -168.4) * mm, "mid": v(-637.64, -168.73) * mm, "end": v(-638.2, -168.85) * mm});
            skLineSegment(sketch, "E1738.94.MirrorCS", {"start": v(-639.94, -150.35) * mm, "end": v(-643.7, -150.35) * mm});
            skLineSegment(sketch, "E1738.95.MirrorCS", {"start": v(-642.2, -157.85) * mm, "end": v(-642.2, -155.35) * mm});
            skLineSegment(sketch, "E1738.96.MirrorCS", {"start": v(-636.7, -164.41) * mm, "end": v(-636.7, -167.35) * mm});
            skLineSegment(sketch, "E1738.97.MirrorCS", {"start": v(-641.15, -168.85) * mm, "end": v(-638.2, -168.85) * mm});
            skPoint(sketch, "E1738.99.MirrorP", {"position": v(-641.15, -148.85) * mm});
            skLineSegment(sketch, "E1738.101.MirrorCS", {"start": v(-636.7, -164.41) * mm, "end": v(-636.7, -167.35) * mm});
            skPoint(sketch, "E1738.103.MirrorP", {"position": v(-642.2, -158.85) * mm});
            skArc(sketch, "E1738.104.MirrorCS", {"start": v(-644.77, -156.9) * mm, "mid": v(-645.66, -156.3) * mm, "end": v(-646.7, -156.1) * mm});
            skArc(sketch, "E1738.105.MirrorCS", {"start": v(-644.77, -160.8) * mm, "mid": v(-644.17, -159.9) * mm, "end": v(-643.96, -158.85) * mm});
            skLineSegment(sketch, "E1738.106.MirrorCS", {"start": v(-642.2, -155.35) * mm, "end": v(-638.94, -152.08) * mm});
            skLineSegment(sketch, "E1738.107.MirrorCS", {"start": v(-638.2, -150.35) * mm, "end": v(-644.77, -156.9) * mm});
            skLineSegment(sketch, "E1738.108.MirrorCS", {"start": v(-638.2, -165.62) * mm, "end": v(-638.2, -161.85) * mm});
            skArc(sketch, "E1738.109.MirrorCS", {"start": v(-637.15, -168.4) * mm, "mid": v(-636.82, -167.92) * mm, "end": v(-636.7, -167.35) * mm});
            skPoint(sketch, "E1738.110.MirrorP", {"position": v(-644.77, -156.9) * mm});
            skLineSegment(sketch, "E1738.111.MirrorCS", {"start": v(-639.94, -167.35) * mm, "end": v(-643.7, -167.35) * mm});
            skLineSegment(sketch, "E1738.112.MirrorCS", {"start": v(-645.7, -163.35) * mm, "end": v(-643.2, -163.35) * mm});
            skLineSegment(sketch, "E1738.113.MirrorCS", {"start": v(-642.2, -159.85) * mm, "end": v(-642.2, -162.35) * mm});
            skLineSegment(sketch, "E1738.114.MirrorCS", {"start": v(-643.2, -154.35) * mm, "end": v(-639.94, -151.08) * mm});
            skPoint(sketch, "E1738.115.MirrorP", {"position": v(-636.7, -164.41) * mm});
            skLineSegment(sketch, "E1738.116.MirrorCS", {"start": v(-637.15, -149.29) * mm, "end": v(-638.2, -150.35) * mm});
            skLineSegment(sketch, "E1738.117.MirrorCS", {"start": v(-642.7, -158.85) * mm, "end": v(-643.96, -158.85) * mm});
            skArc(sketch, "E1738.118.MirrorCS", {"start": v(-637.15, -149.29) * mm, "mid": v(-636.82, -149.77) * mm, "end": v(-636.7, -150.35) * mm});
            skPoint(sketch, "E1738.119.MirrorP", {"position": v(-641.15, -148.85) * mm});
            skLineSegment(sketch, "E1738.120.MirrorCS", {"start": v(-638.2, -161.85) * mm, "end": v(-637.2, -161.85) * mm});
            skLineSegment(sketch, "E1738.121.MirrorCS", {"start": v(-645.7, -154.35) * mm, "end": v(-643.2, -154.35) * mm});
            skArc(sketch, "E1738.122.MirrorCS", {"start": v(-644.77, -156.9) * mm, "mid": v(-644.17, -157.8) * mm, "end": v(-643.96, -158.85) * mm});
            skLineSegment(sketch, "E1738.123.MirrorCS", {"start": v(-641.15, -148.85) * mm, "end": v(-638.2, -148.85) * mm});
            skPoint(sketch, "E1738.124.MirrorP", {"position": v(-636.7, -158.85) * mm});
            skLineSegment(sketch, "E1738.125.MirrorCS", {"start": v(-636.7, -162.35) * mm, "end": v(-636.7, -164.41) * mm});
            skLineSegment(sketch, "E1738.126.MirrorCS", {"start": v(-641.15, -148.85) * mm, "end": v(-638.2, -148.85) * mm});
            skLineSegment(sketch, "E1738.127.MirrorCS", {"start": v(-642.2, -162.35) * mm, "end": v(-638.94, -165.62) * mm});
            skPoint(sketch, "E1738.128.MirrorP", {"position": v(-636.7, -164.41) * mm});
            skPoint(sketch, "E1738.129.MirrorP", {"position": v(-644.77, -160.8) * mm});
            skPoint(sketch, "E1738.131.MirrorP", {"position": v(-644.77, -156.9) * mm});
            skLineSegment(sketch, "E1738.132.MirrorCS", {"start": v(-638.2, -152.08) * mm, "end": v(-638.2, -155.85) * mm});
            skPoint(sketch, "E1738.133.MirrorP", {"position": v(-636.7, -153.28) * mm});
            skSolve(sketch);
        }
        {
            var Q0;
            Q0 = qSketchRegion(id + "F14", true);
            extrude(context, id + "F15", {"entities" : qUnion([Q0]), "depth" : 350 * mm, "offsetDistance" : 25 * mm});
        }
        {
            var Q0;
            Q0=qCreatedBy(makeId("Top.planeOp"),FACE);
            var sketch = newSketch(context, id + "F16", { "sketchPlane" : qUnion([Q0])});
            skLineSegment(sketch, "E1739", {"start": v(-606.65, -156.51) * mm, "end": v(-609.15, -156.51) * mm});
            skLineSegment(sketch, "E1740", {"start": v(-612.42, -159.78) * mm, "end": v(-612.42, -160.51) * mm});
            skLineSegment(sketch, "E1741", {"start": v(-612.42, -160.51) * mm, "end": v(-608.65, -160.51) * mm});
            skLineSegment(sketch, "E1742", {"start": v(-608.65, -160.51) * mm, "end": v(-608.65, -161.51) * mm});
            skLineSegment(sketch, "E1743", {"start": v(-611.21, -162.01) * mm, "end": v(-614.15, -162.01) * mm});
            skLineSegment(sketch, "E1744", {"start": v(-606.65, -156.51) * mm, "end": v(-605.65, -156.01) * mm});
            skLineSegment(sketch, "E1745", {"start": v(-608.65, -161.51) * mm, "end": v(-609.15, -161.51) * mm});
            skLineSegment(sketch, "E1746", {"start": v(-609.15, -161.51) * mm, "end": v(-609.15, -162.01) * mm, "construction": true});
            skArc(sketch, "E1747.filletArc", {"start": v(-615.2, -161.57) * mm, "mid": v(-614.72, -161.9) * mm, "end": v(-614.15, -162.01) * mm});
            skLineSegment(sketch, "E1748", {"start": v(-609.15, -162.01) * mm, "end": v(-611.21, -162.01) * mm});
            skPoint(sketch, "E1749.orphan", {"position": v(-605.65, -162.01) * mm});
            skLineSegment(sketch, "E1750.trimOffspring", {"start": v(-614.15, -160.51) * mm, "end": v(-607.6, -153.96) * mm});
            skPoint(sketch, "E1751", {"position": v(-605.65, -156.51) * mm});
            skLineSegment(sketch, "E1752", {"start": v(-609.15, -156.51) * mm, "end": v(-612.42, -159.78) * mm});
            skArc(sketch, "E1753", {"start": v(-607.6, -153.96) * mm, "mid": v(-606.7, -154.55) * mm, "end": v(-605.65, -154.76) * mm});
            skPoint(sketch, "E1754", {"position": v(-607.6, -153.96) * mm});
            skLineSegment(sketch, "E1755", {"start": v(-605.65, -156.01) * mm, "end": v(-605.65, -154.76) * mm});
            skLineSegment(sketch, "E1756", {"start": v(-615.2, -161.57) * mm, "end": v(-614.15, -160.51) * mm});
            skPoint(sketch, "E1757", {"position": v(-611.21, -162.01) * mm});
            skLineSegment(sketch, "E1758", {"start": v(-609.15, -161.51) * mm, "end": v(-609.15, -162.01) * mm});
            skPoint(sketch, "E1759.0.MirrorP", {"position": v(-615.65, -157.58) * mm});
            skPoint(sketch, "E1759.1.MirrorP", {"position": v(-615.65, -157.58) * mm});
            skPoint(sketch, "E1759.2.MirrorP", {"position": v(-615.65, -157.58) * mm});
            skPoint(sketch, "E1759.3.MirrorP", {"position": v(-615.65, -157.58) * mm});
            skPoint(sketch, "E1759.4.MirrorP", {"position": v(-615.65, -157.58) * mm});
            skPoint(sketch, "E1759.5.MirrorP", {"position": v(-615.65, -157.58) * mm});
            skPoint(sketch, "E1759.6.MirrorP", {"position": v(-615.65, -157.58) * mm});
            skPoint(sketch, "E1759.7.MirrorP", {"position": v(-615.65, -157.58) * mm});
            skPoint(sketch, "E1759.8.MirrorP", {"position": v(-615.65, -157.58) * mm});
            skPoint(sketch, "E1759.9.MirrorP", {"position": v(-615.65, -157.58) * mm});
            skPoint(sketch, "E1759.10.MirrorP", {"position": v(-615.65, -157.58) * mm});
            skLineSegment(sketch, "E1759.11.MirrorCS", {"start": v(-615.15, -155.51) * mm, "end": v(-615.65, -155.51) * mm, "construction": true});
            skPoint(sketch, "E1759.12.MirrorP", {"position": v(-615.65, -157.58) * mm});
            skLineSegment(sketch, "E1759.13.MirrorCS", {"start": v(-615.15, -155.51) * mm, "end": v(-615.65, -155.51) * mm});
            skLineSegment(sketch, "E1759.14.MirrorCS", {"start": v(-613.42, -158.78) * mm, "end": v(-614.15, -158.78) * mm});
            skPoint(sketch, "E1759.15.MirrorP", {"position": v(-615.65, -157.58) * mm});
            skLineSegment(sketch, "E1759.16.MirrorCS", {"start": v(-615.15, -155.01) * mm, "end": v(-615.15, -155.51) * mm});
            skPoint(sketch, "E1759.17.MirrorP", {"position": v(-615.65, -152.01) * mm});
            skLineSegment(sketch, "E1759.18.MirrorCS", {"start": v(-615.65, -157.58) * mm, "end": v(-615.65, -160.51) * mm});
            skArc(sketch, "E1759.19.MirrorCS", {"start": v(-607.6, -153.96) * mm, "mid": v(-608.19, -153.06) * mm, "end": v(-608.4, -152.01) * mm});
            skPoint(sketch, "E1759.20.MirrorP", {"position": v(-610.15, -152.01) * mm});
            skLineSegment(sketch, "E1759.21.MirrorCS", {"start": v(-610.15, -155.51) * mm, "end": v(-613.42, -158.78) * mm});
            skLineSegment(sketch, "E1759.23.MirrorCS", {"start": v(-610.15, -153.01) * mm, "end": v(-610.15, -155.51) * mm});
            skLineSegment(sketch, "E1759.24.MirrorCS", {"start": v(-614.15, -158.78) * mm, "end": v(-614.15, -155.01) * mm});
            skLineSegment(sketch, "E1759.25.MirrorCS", {"start": v(-615.65, -155.51) * mm, "end": v(-615.65, -157.58) * mm});
            skLineSegment(sketch, "E1759.26.MirrorCS", {"start": v(-609.65, -152.01) * mm, "end": v(-608.4, -152.01) * mm});
            skArc(sketch, "E1759.28.MirrorCS", {"start": v(-615.2, -161.57) * mm, "mid": v(-615.54, -161.09) * mm, "end": v(-615.65, -160.51) * mm});
            skLineSegment(sketch, "E1759.29.MirrorCS", {"start": v(-610.15, -153.01) * mm, "end": v(-609.65, -152.01) * mm});
            skLineSegment(sketch, "E1759.30.MirrorCS", {"start": v(-615.65, -157.58) * mm, "end": v(-615.65, -160.51) * mm});
            skPoint(sketch, "E1759.31.MirrorP", {"position": v(-615.65, -157.58) * mm});
            skLineSegment(sketch, "E1759.32.MirrorCS", {"start": v(-614.15, -155.01) * mm, "end": v(-615.15, -155.01) * mm});
            skPoint(sketch, "E1760.0.MirrorP", {"position": v(-611.21, -142.01) * mm});
            skPoint(sketch, "E1760.1.MirrorP", {"position": v(-615.65, -146.45) * mm});
            skPoint(sketch, "E1760.2.MirrorP", {"position": v(-611.21, -142.01) * mm});
            skPoint(sketch, "E1760.3.MirrorP", {"position": v(-615.65, -146.45) * mm});
            skPoint(sketch, "E1760.4.MirrorP", {"position": v(-611.21, -142.01) * mm});
            skPoint(sketch, "E1760.5.MirrorP", {"position": v(-615.65, -146.45) * mm});
            skPoint(sketch, "E1760.6.MirrorP", {"position": v(-615.65, -146.45) * mm});
            skPoint(sketch, "E1760.7.MirrorP", {"position": v(-611.21, -142.01) * mm});
            skPoint(sketch, "E1760.8.MirrorP", {"position": v(-611.21, -142.01) * mm});
            skPoint(sketch, "E1760.9.MirrorP", {"position": v(-615.65, -146.45) * mm});
            skPoint(sketch, "E1760.10.MirrorP", {"position": v(-611.21, -142.01) * mm});
            skPoint(sketch, "E1760.11.MirrorP", {"position": v(-615.65, -146.45) * mm});
            skPoint(sketch, "E1760.12.MirrorP", {"position": v(-611.21, -142.01) * mm});
            skPoint(sketch, "E1760.13.MirrorP", {"position": v(-615.65, -146.45) * mm});
            skPoint(sketch, "E1760.14.MirrorP", {"position": v(-611.21, -142.01) * mm});
            skPoint(sketch, "E1760.15.MirrorP", {"position": v(-615.65, -146.45) * mm});
            skPoint(sketch, "E1760.16.MirrorP", {"position": v(-611.21, -142.01) * mm});
            skPoint(sketch, "E1760.17.MirrorP", {"position": v(-615.65, -146.45) * mm});
            skLineSegment(sketch, "E1760.18.MirrorCS", {"start": v(-615.15, -148.51) * mm, "end": v(-615.65, -148.51) * mm, "construction": true});
            skPoint(sketch, "E1760.19.MirrorP", {"position": v(-611.21, -142.01) * mm});
            skPoint(sketch, "E1760.20.MirrorP", {"position": v(-615.65, -146.45) * mm});
            skLineSegment(sketch, "E1760.21.MirrorCS", {"start": v(-609.15, -142.51) * mm, "end": v(-609.15, -142.01) * mm, "construction": true});
            skLineSegment(sketch, "E1760.22.MirrorCS", {"start": v(-609.15, -142.51) * mm, "end": v(-609.15, -142.01) * mm});
            skPoint(sketch, "E1760.23.MirrorP", {"position": v(-611.21, -142.01) * mm});
            skLineSegment(sketch, "E1760.24.MirrorCS", {"start": v(-615.15, -148.51) * mm, "end": v(-615.65, -148.51) * mm});
            skPoint(sketch, "E1760.25.MirrorP", {"position": v(-615.65, -146.45) * mm});
            skPoint(sketch, "E1760.26.MirrorP", {"position": v(-611.21, -142.01) * mm});
            skPoint(sketch, "E1760.27.MirrorP", {"position": v(-615.65, -146.45) * mm});
            skLineSegment(sketch, "E1760.28.MirrorCS", {"start": v(-608.65, -142.51) * mm, "end": v(-609.15, -142.51) * mm});
            skLineSegment(sketch, "E1760.29.MirrorCS", {"start": v(-615.15, -149.01) * mm, "end": v(-615.15, -148.51) * mm});
            skLineSegment(sketch, "E1760.30.MirrorCS", {"start": v(-614.15, -149.01) * mm, "end": v(-615.15, -149.01) * mm});
            skPoint(sketch, "E1760.31.MirrorP", {"position": v(-611.21, -142.01) * mm});
            skPoint(sketch, "E1760.32.MirrorP", {"position": v(-615.65, -146.45) * mm});
            skLineSegment(sketch, "E1760.34.MirrorCS", {"start": v(-615.65, -148.51) * mm, "end": v(-615.65, -146.45) * mm});
            skArc(sketch, "E1760.35.MirrorCS", {"start": v(-615.2, -142.45) * mm, "mid": v(-615.54, -142.94) * mm, "end": v(-615.65, -143.51) * mm});
            skLineSegment(sketch, "E1760.36.MirrorCS", {"start": v(-614.15, -145.24) * mm, "end": v(-614.15, -149.01) * mm});
            skLineSegment(sketch, "E1760.37.MirrorCS", {"start": v(-610.15, -151.01) * mm, "end": v(-609.65, -152.01) * mm});
            skLineSegment(sketch, "E1760.38.MirrorCS", {"start": v(-615.65, -146.45) * mm, "end": v(-615.65, -143.51) * mm});
            skLineSegment(sketch, "E1760.40.MirrorCS", {"start": v(-610.15, -148.51) * mm, "end": v(-613.42, -145.24) * mm});
            skLineSegment(sketch, "E1760.41.MirrorCS", {"start": v(-610.15, -151.01) * mm, "end": v(-610.15, -148.51) * mm});
            skLineSegment(sketch, "E1760.42.MirrorCS", {"start": v(-606.65, -147.51) * mm, "end": v(-609.15, -147.51) * mm});
            skLineSegment(sketch, "E1760.43.MirrorCS", {"start": v(-612.42, -143.51) * mm, "end": v(-608.65, -143.51) * mm});
            skLineSegment(sketch, "E1760.44.MirrorCS", {"start": v(-612.42, -144.24) * mm, "end": v(-612.42, -143.51) * mm});
            skLineSegment(sketch, "E1760.45.MirrorCS", {"start": v(-611.21, -142.01) * mm, "end": v(-614.15, -142.01) * mm});
            skLineSegment(sketch, "E1760.46.MirrorCS", {"start": v(-608.65, -143.51) * mm, "end": v(-608.65, -142.51) * mm});
            skLineSegment(sketch, "E1760.47.MirrorCS", {"start": v(-606.65, -147.51) * mm, "end": v(-605.65, -148.01) * mm});
            skLineSegment(sketch, "E1760.48.MirrorCS", {"start": v(-611.21, -142.01) * mm, "end": v(-614.15, -142.01) * mm});
            skLineSegment(sketch, "E1760.49.MirrorCS", {"start": v(-609.15, -142.01) * mm, "end": v(-611.21, -142.01) * mm});
            skArc(sketch, "E1760.50.MirrorCS", {"start": v(-615.2, -142.45) * mm, "mid": v(-614.72, -142.13) * mm, "end": v(-614.15, -142.01) * mm});
            skLineSegment(sketch, "E1760.51.MirrorCS", {"start": v(-609.15, -147.51) * mm, "end": v(-612.42, -144.24) * mm});
            skLineSegment(sketch, "E1760.52.MirrorCS", {"start": v(-614.15, -143.51) * mm, "end": v(-607.6, -150.07) * mm});
            skLineSegment(sketch, "E1760.53.MirrorCS", {"start": v(-615.2, -142.45) * mm, "end": v(-614.15, -143.51) * mm});
            skLineSegment(sketch, "E1760.54.MirrorCS", {"start": v(-615.2, -142.45) * mm, "end": v(-614.15, -143.51) * mm});
            skLineSegment(sketch, "E1760.55.MirrorCS", {"start": v(-605.65, -148.01) * mm, "end": v(-605.65, -149.26) * mm});
            skArc(sketch, "E1760.56.MirrorCS", {"start": v(-607.6, -150.07) * mm, "mid": v(-606.7, -149.47) * mm, "end": v(-605.65, -149.26) * mm});
            skPoint(sketch, "E1760.58.MirrorP", {"position": v(-605.65, -147.51) * mm});
            skLineSegment(sketch, "E1760.59.MirrorCS", {"start": v(-613.42, -145.24) * mm, "end": v(-614.15, -145.24) * mm});
            skPoint(sketch, "E1760.60.MirrorP", {"position": v(-611.21, -142.01) * mm});
            skArc(sketch, "E1760.61.MirrorCS", {"start": v(-607.6, -150.07) * mm, "mid": v(-608.19, -150.96) * mm, "end": v(-608.4, -152.01) * mm});
            skPoint(sketch, "E1760.62.MirrorP", {"position": v(-605.65, -142.01) * mm});
            skPoint(sketch, "E1760.63.MirrorP", {"position": v(-607.6, -150.07) * mm});
            skPoint(sketch, "E1760.64.MirrorP", {"position": v(-607.6, -150.07) * mm});
            skLineSegment(sketch, "E1760.65.MirrorCS", {"start": v(-615.65, -146.45) * mm, "end": v(-615.65, -143.51) * mm});
            skPoint(sketch, "E1760.66.MirrorP", {"position": v(-615.65, -146.45) * mm});
            skPoint(sketch, "E1761.0.MirrorP", {"position": v(-595.65, -146.45) * mm});
            skPoint(sketch, "E1761.1.MirrorP", {"position": v(-600.09, -162.01) * mm});
            skPoint(sketch, "E1761.2.MirrorP", {"position": v(-600.09, -142.01) * mm});
            skPoint(sketch, "E1761.3.MirrorP", {"position": v(-595.65, -146.45) * mm});
            skPoint(sketch, "E1761.4.MirrorP", {"position": v(-595.65, -157.58) * mm});
            skPoint(sketch, "E1761.5.MirrorP", {"position": v(-600.09, -162.01) * mm});
            skPoint(sketch, "E1761.6.MirrorP", {"position": v(-600.09, -162.01) * mm});
            skPoint(sketch, "E1761.7.MirrorP", {"position": v(-595.65, -146.45) * mm});
            skPoint(sketch, "E1761.8.MirrorP", {"position": v(-600.09, -142.01) * mm});
            skPoint(sketch, "E1761.9.MirrorP", {"position": v(-595.65, -157.58) * mm});
            skPoint(sketch, "E1761.10.MirrorP", {"position": v(-595.65, -146.45) * mm});
            skPoint(sketch, "E1761.11.MirrorP", {"position": v(-600.09, -162.01) * mm});
            skPoint(sketch, "E1761.12.MirrorP", {"position": v(-600.09, -142.01) * mm});
            skPoint(sketch, "E1761.13.MirrorP", {"position": v(-595.65, -157.58) * mm});
            skPoint(sketch, "E1761.14.MirrorP", {"position": v(-595.65, -146.45) * mm});
            skPoint(sketch, "E1761.15.MirrorP", {"position": v(-600.09, -162.01) * mm});
            skPoint(sketch, "E1761.16.MirrorP", {"position": v(-595.65, -157.58) * mm});
            skPoint(sketch, "E1761.17.MirrorP", {"position": v(-600.09, -142.01) * mm});
            skPoint(sketch, "E1761.18.MirrorP", {"position": v(-600.09, -162.01) * mm});
            skPoint(sketch, "E1761.19.MirrorP", {"position": v(-600.09, -142.01) * mm});
            skPoint(sketch, "E1761.20.MirrorP", {"position": v(-595.65, -146.45) * mm});
            skPoint(sketch, "E1761.21.MirrorP", {"position": v(-595.65, -157.58) * mm});
            skPoint(sketch, "E1761.22.MirrorP", {"position": v(-595.65, -157.58) * mm});
            skPoint(sketch, "E1761.23.MirrorP", {"position": v(-600.09, -162.01) * mm});
            skPoint(sketch, "E1761.24.MirrorP", {"position": v(-595.65, -146.45) * mm});
            skPoint(sketch, "E1761.25.MirrorP", {"position": v(-600.09, -142.01) * mm});
            skPoint(sketch, "E1761.26.MirrorP", {"position": v(-595.65, -157.58) * mm});
            skPoint(sketch, "E1761.27.MirrorP", {"position": v(-595.65, -146.45) * mm});
            skPoint(sketch, "E1761.28.MirrorP", {"position": v(-600.09, -162.01) * mm});
            skPoint(sketch, "E1761.29.MirrorP", {"position": v(-600.09, -142.01) * mm});
            skPoint(sketch, "E1761.30.MirrorP", {"position": v(-595.65, -157.58) * mm});
            skPoint(sketch, "E1761.31.MirrorP", {"position": v(-600.09, -142.01) * mm});
            skPoint(sketch, "E1761.32.MirrorP", {"position": v(-600.09, -162.01) * mm});
            skPoint(sketch, "E1761.33.MirrorP", {"position": v(-595.65, -146.45) * mm});
            skPoint(sketch, "E1761.34.MirrorP", {"position": v(-595.65, -146.45) * mm});
            skPoint(sketch, "E1761.35.MirrorP", {"position": v(-600.09, -142.01) * mm});
            skPoint(sketch, "E1761.36.MirrorP", {"position": v(-595.65, -157.58) * mm});
            skPoint(sketch, "E1761.37.MirrorP", {"position": v(-600.09, -162.01) * mm});
            skLineSegment(sketch, "E1761.38.MirrorCS", {"start": v(-602.15, -142.51) * mm, "end": v(-602.15, -142.01) * mm, "construction": true});
            skLineSegment(sketch, "E1761.39.MirrorCS", {"start": v(-596.15, -148.51) * mm, "end": v(-595.65, -148.51) * mm, "construction": true});
            skLineSegment(sketch, "E1761.40.MirrorCS", {"start": v(-596.15, -155.51) * mm, "end": v(-595.65, -155.51) * mm, "construction": true});
            skLineSegment(sketch, "E1761.41.MirrorCS", {"start": v(-602.15, -161.51) * mm, "end": v(-602.15, -162.01) * mm, "construction": true});
            skPoint(sketch, "E1761.42.MirrorP", {"position": v(-595.65, -146.45) * mm});
            skPoint(sketch, "E1761.43.MirrorP", {"position": v(-595.65, -157.58) * mm});
            skPoint(sketch, "E1761.44.MirrorP", {"position": v(-600.09, -162.01) * mm});
            skPoint(sketch, "E1761.45.MirrorP", {"position": v(-600.09, -142.01) * mm});
            skLineSegment(sketch, "E1761.46.MirrorCS", {"start": v(-596.15, -148.51) * mm, "end": v(-595.65, -148.51) * mm});
            skLineSegment(sketch, "E1761.47.MirrorCS", {"start": v(-596.15, -155.01) * mm, "end": v(-596.15, -155.51) * mm});
            skLineSegment(sketch, "E1761.48.MirrorCS", {"start": v(-596.15, -155.51) * mm, "end": v(-595.65, -155.51) * mm});
            skLineSegment(sketch, "E1761.49.MirrorCS", {"start": v(-596.09, -161.57) * mm, "end": v(-597.15, -160.51) * mm});
            skLineSegment(sketch, "E1761.50.MirrorCS", {"start": v(-602.65, -161.51) * mm, "end": v(-602.15, -161.51) * mm});
            skPoint(sketch, "E1761.51.MirrorP", {"position": v(-595.65, -157.58) * mm});
            skPoint(sketch, "E1761.52.MirrorP", {"position": v(-595.65, -146.45) * mm});
            skPoint(sketch, "E1761.53.MirrorP", {"position": v(-600.09, -142.01) * mm});
            skPoint(sketch, "E1761.54.MirrorP", {"position": v(-600.09, -162.01) * mm});
            skLineSegment(sketch, "E1761.55.MirrorCS", {"start": v(-602.65, -142.51) * mm, "end": v(-602.15, -142.51) * mm});
            skLineSegment(sketch, "E1761.56.MirrorCS", {"start": v(-596.15, -149.01) * mm, "end": v(-596.15, -148.51) * mm});
            skLineSegment(sketch, "E1761.57.MirrorCS", {"start": v(-602.15, -161.51) * mm, "end": v(-602.15, -162.01) * mm});
            skLineSegment(sketch, "E1761.58.MirrorCS", {"start": v(-602.15, -142.51) * mm, "end": v(-602.15, -142.01) * mm});
            skLineSegment(sketch, "E1761.59.MirrorCS", {"start": v(-602.65, -143.51) * mm, "end": v(-602.65, -142.51) * mm});
            skLineSegment(sketch, "E1761.60.MirrorCS", {"start": v(-598.88, -144.24) * mm, "end": v(-598.88, -143.51) * mm});
            skPoint(sketch, "E1761.61.MirrorP", {"position": v(-600.09, -142.01) * mm});
            skLineSegment(sketch, "E1761.62.MirrorCS", {"start": v(-598.88, -159.78) * mm, "end": v(-598.88, -160.51) * mm});
            skPoint(sketch, "E1761.63.MirrorP", {"position": v(-600.09, -162.01) * mm});
            skPoint(sketch, "E1761.64.MirrorP", {"position": v(-595.65, -157.58) * mm});
            skLineSegment(sketch, "E1761.65.MirrorCS", {"start": v(-596.09, -161.57) * mm, "end": v(-597.15, -160.51) * mm});
            skLineSegment(sketch, "E1761.66.MirrorCS", {"start": v(-597.88, -145.24) * mm, "end": v(-597.15, -145.24) * mm});
            skLineSegment(sketch, "E1761.67.MirrorCS", {"start": v(-604.65, -147.51) * mm, "end": v(-605.65, -148.01) * mm});
            skLineSegment(sketch, "E1761.68.MirrorCS", {"start": v(-601.15, -153.01) * mm, "end": v(-601.65, -152.01) * mm});
            skLineSegment(sketch, "E1761.69.MirrorCS", {"start": v(-601.65, -152.01) * mm, "end": v(-602.9, -152.01) * mm});
            skLineSegment(sketch, "E1761.70.MirrorCS", {"start": v(-604.65, -156.51) * mm, "end": v(-605.65, -156.01) * mm});
            skLineSegment(sketch, "E1761.71.MirrorCS", {"start": v(-595.65, -146.45) * mm, "end": v(-595.65, -143.51) * mm});
            skPoint(sketch, "E1761.72.MirrorP", {"position": v(-595.65, -146.45) * mm});
            skPoint(sketch, "E1761.73.MirrorP", {"position": v(-595.65, -152.01) * mm});
            skLineSegment(sketch, "E1761.74.MirrorCS", {"start": v(-596.09, -142.45) * mm, "end": v(-597.15, -143.51) * mm});
            skLineSegment(sketch, "E1761.75.MirrorCS", {"start": v(-601.15, -151.01) * mm, "end": v(-601.65, -152.01) * mm});
            skLineSegment(sketch, "E1761.76.MirrorCS", {"start": v(-597.88, -158.78) * mm, "end": v(-597.15, -158.78) * mm});
            skLineSegment(sketch, "E1761.78.MirrorCS", {"start": v(-595.65, -146.45) * mm, "end": v(-595.65, -143.51) * mm});
            skLineSegment(sketch, "E1761.79.MirrorCS", {"start": v(-602.15, -162.01) * mm, "end": v(-600.09, -162.01) * mm});
            skLineSegment(sketch, "E1761.80.MirrorCS", {"start": v(-602.65, -160.51) * mm, "end": v(-602.65, -161.51) * mm});
            skLineSegment(sketch, "E1761.81.MirrorCS", {"start": v(-600.09, -162.01) * mm, "end": v(-597.15, -162.01) * mm});
            skPoint(sketch, "E1761.83.MirrorP", {"position": v(-600.09, -162.01) * mm});
            skLineSegment(sketch, "E1761.84.MirrorCS", {"start": v(-597.15, -149.01) * mm, "end": v(-596.15, -149.01) * mm});
            skLineSegment(sketch, "E1761.85.MirrorCS", {"start": v(-602.15, -142.01) * mm, "end": v(-600.09, -142.01) * mm});
            skArc(sketch, "E1761.86.MirrorCS", {"start": v(-603.7, -153.96) * mm, "mid": v(-604.6, -154.55) * mm, "end": v(-605.65, -154.76) * mm});
            skPoint(sketch, "E1761.87.MirrorP", {"position": v(-603.7, -153.96) * mm});
            skPoint(sketch, "E1761.88.MirrorP", {"position": v(-601.15, -152.01) * mm});
            skArc(sketch, "E1761.89.MirrorCS", {"start": v(-596.09, -142.45) * mm, "mid": v(-596.58, -142.13) * mm, "end": v(-597.15, -142.01) * mm});
            skLineSegment(sketch, "E1761.90.MirrorCS", {"start": v(-595.65, -148.51) * mm, "end": v(-595.65, -146.45) * mm});
            skLineSegment(sketch, "E1761.91.MirrorCS", {"start": v(-597.15, -160.51) * mm, "end": v(-603.7, -153.96) * mm});
            skLineSegment(sketch, "E1761.92.MirrorCS", {"start": v(-602.15, -156.51) * mm, "end": v(-598.88, -159.78) * mm});
            skArc(sketch, "E1761.93.MirrorCS", {"start": v(-596.09, -161.57) * mm, "mid": v(-596.58, -161.9) * mm, "end": v(-597.15, -162.01) * mm});
            skLineSegment(sketch, "E1761.94.MirrorCS", {"start": v(-598.88, -143.51) * mm, "end": v(-602.65, -143.51) * mm});
            skLineSegment(sketch, "E1761.95.MirrorCS", {"start": v(-601.15, -151.01) * mm, "end": v(-601.15, -148.51) * mm});
            skLineSegment(sketch, "E1761.96.MirrorCS", {"start": v(-595.65, -157.58) * mm, "end": v(-595.65, -160.51) * mm});
            skLineSegment(sketch, "E1761.97.MirrorCS", {"start": v(-600.09, -162.01) * mm, "end": v(-597.15, -162.01) * mm});
            skPoint(sketch, "E1761.99.MirrorP", {"position": v(-600.09, -142.01) * mm});
            skLineSegment(sketch, "E1761.101.MirrorCS", {"start": v(-595.65, -157.58) * mm, "end": v(-595.65, -160.51) * mm});
            skPoint(sketch, "E1761.103.MirrorP", {"position": v(-601.15, -152.01) * mm});
            skArc(sketch, "E1761.104.MirrorCS", {"start": v(-603.7, -150.07) * mm, "mid": v(-604.6, -149.47) * mm, "end": v(-605.65, -149.26) * mm});
            skArc(sketch, "E1761.105.MirrorCS", {"start": v(-603.7, -153.96) * mm, "mid": v(-603.1, -153.06) * mm, "end": v(-602.9, -152.01) * mm});
            skLineSegment(sketch, "E1761.106.MirrorCS", {"start": v(-601.15, -148.51) * mm, "end": v(-597.88, -145.24) * mm});
            skLineSegment(sketch, "E1761.107.MirrorCS", {"start": v(-597.15, -143.51) * mm, "end": v(-603.7, -150.07) * mm});
            skLineSegment(sketch, "E1761.108.MirrorCS", {"start": v(-597.15, -158.78) * mm, "end": v(-597.15, -155.01) * mm});
            skArc(sketch, "E1761.109.MirrorCS", {"start": v(-596.09, -161.57) * mm, "mid": v(-595.76, -161.09) * mm, "end": v(-595.65, -160.51) * mm});
            skPoint(sketch, "E1761.110.MirrorP", {"position": v(-603.7, -150.07) * mm});
            skLineSegment(sketch, "E1761.111.MirrorCS", {"start": v(-598.88, -160.51) * mm, "end": v(-602.65, -160.51) * mm});
            skLineSegment(sketch, "E1761.112.MirrorCS", {"start": v(-604.65, -156.51) * mm, "end": v(-602.15, -156.51) * mm});
            skLineSegment(sketch, "E1761.113.MirrorCS", {"start": v(-601.15, -153.01) * mm, "end": v(-601.15, -155.51) * mm});
            skLineSegment(sketch, "E1761.114.MirrorCS", {"start": v(-602.15, -147.51) * mm, "end": v(-598.88, -144.24) * mm});
            skPoint(sketch, "E1761.115.MirrorP", {"position": v(-595.65, -157.58) * mm});
            skLineSegment(sketch, "E1761.116.MirrorCS", {"start": v(-596.09, -142.45) * mm, "end": v(-597.15, -143.51) * mm});
            skLineSegment(sketch, "E1761.117.MirrorCS", {"start": v(-601.65, -152.01) * mm, "end": v(-602.9, -152.01) * mm});
            skArc(sketch, "E1761.118.MirrorCS", {"start": v(-596.09, -142.45) * mm, "mid": v(-595.76, -142.94) * mm, "end": v(-595.65, -143.51) * mm});
            skPoint(sketch, "E1761.119.MirrorP", {"position": v(-600.09, -142.01) * mm});
            skLineSegment(sketch, "E1761.120.MirrorCS", {"start": v(-597.15, -155.01) * mm, "end": v(-596.15, -155.01) * mm});
            skLineSegment(sketch, "E1761.121.MirrorCS", {"start": v(-604.65, -147.51) * mm, "end": v(-602.15, -147.51) * mm});
            skArc(sketch, "E1761.122.MirrorCS", {"start": v(-603.7, -150.07) * mm, "mid": v(-603.1, -150.96) * mm, "end": v(-602.9, -152.01) * mm});
            skLineSegment(sketch, "E1761.123.MirrorCS", {"start": v(-600.09, -142.01) * mm, "end": v(-597.15, -142.01) * mm});
            skPoint(sketch, "E1761.124.MirrorP", {"position": v(-595.65, -152.01) * mm});
            skLineSegment(sketch, "E1761.125.MirrorCS", {"start": v(-595.65, -155.51) * mm, "end": v(-595.65, -157.58) * mm});
            skLineSegment(sketch, "E1761.126.MirrorCS", {"start": v(-600.09, -142.01) * mm, "end": v(-597.15, -142.01) * mm});
            skLineSegment(sketch, "E1761.127.MirrorCS", {"start": v(-601.15, -155.51) * mm, "end": v(-597.88, -158.78) * mm});
            skPoint(sketch, "E1761.128.MirrorP", {"position": v(-595.65, -157.58) * mm});
            skPoint(sketch, "E1761.129.MirrorP", {"position": v(-603.7, -153.96) * mm});
            skPoint(sketch, "E1761.131.MirrorP", {"position": v(-603.7, -150.07) * mm});
            skLineSegment(sketch, "E1761.132.MirrorCS", {"start": v(-597.15, -145.24) * mm, "end": v(-597.15, -149.01) * mm});
            skPoint(sketch, "E1761.133.MirrorP", {"position": v(-595.65, -146.45) * mm});
            skSolve(sketch);
        }
        {
            var Q0;
            Q0 = qSketchRegion(id + "F16", true);
            extrude(context, id + "F17", {"entities" : qUnion([Q0]), "depth" : 1460 * mm, "offsetDistance" : 25 * mm});
        }
    });
